FCSTD DOCUMENT  (FreeCAD 0.18R4 (GitTag))
Label: plate
License: All rights reserved
LicenseURL: http://en.wikipedia.org/wiki/All_rights_reserved
objects: Part::Part2DObjectPython×671, App::DocumentObjectGroup×94
note: 671 computed .brp shape members not serialized (recipe doc carries the construction recipe); baked Part::Feature solids carry a one-line shape summary decoded from their .brp

FEATURE [Part::Part2DObjectPython] Arc  # Draft 2D object (typed FeaturePython)
  FirstAngle = 90
  LastAngle = 180
  MakeFace = true
  Placement = pos=(3.275,-3.275,0) rot=(0,0,1;0rad)
  Radius = 0.75
FEATURE [Part::Part2DObjectPython] Arc001  # Draft 2D object (typed FeaturePython)
  FirstAngle = 90
  LastAngle = 180
  MakeFace = true
  Placement = pos=(15.775,-3.275,0) rot=(0,0,-1;1.5708rad)
  Radius = 0.75
FEATURE [Part::Part2DObjectPython] Arc002  # Draft 2D object (typed FeaturePython)
  FirstAngle = 90
  LastAngle = 180
  MakeFace = true
  Placement = pos=(3.275,-15.775,0) rot=(0,0,1;1.5708rad)
  Radius = 0.75
FEATURE [Part::Part2DObjectPython] Arc003  # Draft 2D object (typed FeaturePython)
  FirstAngle = 90
  LastAngle = 180
  MakeFace = true
  Placement = pos=(15.775,-15.775,0) rot=(0,0,1;3.14159rad)
  Radius = 0.75
FEATURE [Part::Part2DObjectPython] Line004  # Draft 2D object (typed FeaturePython)
  ChamferSize = 0
  Closed = false
  End = (16.525,-3.275,0)
  FilletRadius = 0
  Length = 12.5
  MakeFace = true
  Placement = pos=(16.525,-15.775,0) rot=(0,0,1;0rad)
  Points = (2) [(0,0,0),(0,12.5,0)]
  Start = (16.525,-15.775,0)
  Subdivisions = 0
FEATURE [Part::Part2DObjectPython] Line005  # Draft 2D object (typed FeaturePython)
  ChamferSize = 0
  Closed = false
  End = (3.275,-2.525,0)
  FilletRadius = 0
  Length = 12.5
  MakeFace = true
  Placement = pos=(15.775,-2.525,0) rot=(0,0,1;0rad)
  Points = (2) [(0,0,0),(-12.5,2.22045e-15,0)]
  Start = (15.775,-2.525,0)
  Subdivisions = 0
FEATURE [Part::Part2DObjectPython] Line006  # Draft 2D object (typed FeaturePython)
  ChamferSize = 0
  Closed = false
  End = (2.525,-15.775,0)
  FilletRadius = 0
  Length = 12.5
  MakeFace = true
  Placement = pos=(2.525,-3.275,0) rot=(0,0,1;0rad)
  Points = (2) [(0,0,0),(0,-12.5,0)]
  Start = (2.525,-3.275,0)
  Subdivisions = 0
FEATURE [Part::Part2DObjectPython] Line007  # Draft 2D object (typed FeaturePython)
  ChamferSize = 0
  Closed = false
  End = (15.775,-16.525,0)
  FilletRadius = 0
  Length = 12.5
  MakeFace = true
  Placement = pos=(3.275,-16.525,0) rot=(0,0,1;0rad)
  Points = (2) [(0,0,0),(12.5,-3.55271e-15,0)]
  Start = (3.275,-16.525,0)
  Subdivisions = 0
FEATURE [App::DocumentObjectGroup] Group
  Group = -> [Arc,Arc001,Arc002,Arc003,Line004,Line005,Line006,Line007]
FEATURE [Part::Part2DObjectPython] Arc004  # Draft 2D object (typed FeaturePython)
  FirstAngle = 90
  LastAngle = 180
  MakeFace = true
  Placement = pos=(34.7869,-3.275,0) rot=(0,0,-1;1.5708rad)
  Radius = 0.75
FEATURE [Part::Part2DObjectPython] Arc005  # Draft 2D object (typed FeaturePython)
  FirstAngle = 90
  LastAngle = 180
  MakeFace = true
  Placement = pos=(34.7869,-15.775,0) rot=(0,0,1;3.14159rad)
  Radius = 0.75
FEATURE [Part::Part2DObjectPython] Line010  # Draft 2D object (typed FeaturePython)
  ChamferSize = 0
  Closed = false
  End = (22.2869,-2.525,0)
  FilletRadius = 0
  Length = 12.5
  MakeFace = true
  Placement = pos=(34.7869,-2.525,0) rot=(0,0,1;0rad)
  Points = (2) [(0,0,0),(-12.5,2.22045e-15,0)]
  Start = (34.7869,-2.525,0)
  Subdivisions = 0
FEATURE [Part::Part2DObjectPython] Arc006  # Draft 2D object (typed FeaturePython)
  FirstAngle = 90
  LastAngle = 180
  MakeFace = true
  Placement = pos=(22.2869,-15.775,0) rot=(0,0,1;1.5708rad)
  Radius = 0.75
FEATURE [Part::Part2DObjectPython] Arc007  # Draft 2D object (typed FeaturePython)
  FirstAngle = 90
  LastAngle = 180
  MakeFace = true
  Placement = pos=(22.2869,-3.275,0) rot=(0,0,1;0rad)
  Radius = 0.75
FEATURE [Part::Part2DObjectPython] Line014  # Draft 2D object (typed FeaturePython)
  ChamferSize = 0
  Closed = false
  End = (35.5369,-3.275,0)
  FilletRadius = 0
  Length = 12.5
  MakeFace = true
  Placement = pos=(35.5369,-15.775,0) rot=(0,0,1;0rad)
  Points = (2) [(0,0,0),(0,12.5,0)]
  Start = (35.5369,-15.775,0)
  Subdivisions = 0
FEATURE [Part::Part2DObjectPython] Line015  # Draft 2D object (typed FeaturePython)
  ChamferSize = 0
  Closed = false
  End = (34.7869,-16.525,0)
  FilletRadius = 0
  Length = 12.5
  MakeFace = true
  Placement = pos=(22.2869,-16.525,0) rot=(0,0,1;0rad)
  Points = (2) [(0,0,0),(12.5,-3.55271e-15,0)]
  Start = (22.2869,-16.525,0)
  Subdivisions = 0
FEATURE [Part::Part2DObjectPython] Line016  # Draft 2D object (typed FeaturePython)
  ChamferSize = 0
  Closed = false
  End = (21.5369,-15.775,0)
  FilletRadius = 0
  Length = 12.5
  MakeFace = true
  Placement = pos=(21.5369,-3.275,0) rot=(0,0,1;0rad)
  Points = (2) [(0,0,0),(0,-12.5,0)]
  Start = (21.5369,-3.275,0)
  Subdivisions = 0
FEATURE [App::DocumentObjectGroup] Group001
  Group = -> [Arc007,Arc004,Arc006,Arc005,Line014,Line010,Line016,Line015]
FEATURE [Part::Part2DObjectPython] Arc008  # Draft 2D object (typed FeaturePython)
  FirstAngle = 90
  LastAngle = 180
  MakeFace = true
  Placement = pos=(53.7962,-15.775,0) rot=(0,0,1;3.14159rad)
  Radius = 0.75
FEATURE [Part::Part2DObjectPython] Line018  # Draft 2D object (typed FeaturePython)
  ChamferSize = 0
  Closed = false
  End = (40.5462,-15.775,0)
  FilletRadius = 0
  Length = 12.5
  MakeFace = true
  Placement = pos=(40.5462,-3.275,0) rot=(0,0,1;0rad)
  Points = (2) [(0,0,0),(0,-12.5,0)]
  Start = (40.5462,-3.275,0)
  Subdivisions = 0
FEATURE [Part::Part2DObjectPython] Arc009  # Draft 2D object (typed FeaturePython)
  FirstAngle = 90
  LastAngle = 180
  MakeFace = true
  Placement = pos=(41.2962,-15.775,0) rot=(0,0,1;1.5708rad)
  Radius = 0.75
FEATURE [Part::Part2DObjectPython] Line021  # Draft 2D object (typed FeaturePython)
  ChamferSize = 0
  Closed = false
  End = (53.7962,-16.525,0)
  FilletRadius = 0
  Length = 12.5
  MakeFace = true
  Placement = pos=(41.2962,-16.525,0) rot=(0,0,1;0rad)
  Points = (2) [(0,0,0),(12.5,-3.55271e-15,0)]
  Start = (41.2962,-16.525,0)
  Subdivisions = 0
FEATURE [Part::Part2DObjectPython] Arc010  # Draft 2D object (typed FeaturePython)
  FirstAngle = 90
  LastAngle = 180
  MakeFace = true
  Placement = pos=(53.7962,-3.275,0) rot=(0,0,-1;1.5708rad)
  Radius = 0.75
FEATURE [Part::Part2DObjectPython] Arc011  # Draft 2D object (typed FeaturePython)
  FirstAngle = 90
  LastAngle = 180
  MakeFace = true
  Placement = pos=(41.2962,-3.275,0) rot=(0,0,1;0rad)
  Radius = 0.75
FEATURE [Part::Part2DObjectPython] Line022  # Draft 2D object (typed FeaturePython)
  ChamferSize = 0
  Closed = false
  End = (54.5462,-3.275,0)
  FilletRadius = 0
  Length = 12.5
  MakeFace = true
  Placement = pos=(54.5462,-15.775,0) rot=(0,0,1;0rad)
  Points = (2) [(0,0,0),(0,12.5,0)]
  Start = (54.5462,-15.775,0)
  Subdivisions = 0
FEATURE [Part::Part2DObjectPython] Line023  # Draft 2D object (typed FeaturePython)
  ChamferSize = 0
  Closed = false
  End = (41.2962,-2.525,0)
  FilletRadius = 0
  Length = 12.5
  MakeFace = true
  Placement = pos=(53.7962,-2.525,0) rot=(0,0,1;0rad)
  Points = (2) [(0,0,0),(-12.5,2.22045e-15,0)]
  Start = (53.7962,-2.525,0)
  Subdivisions = 0
FEATURE [App::DocumentObjectGroup] Group002
  Group = -> [Arc011,Arc010,Arc009,Arc008,Line022,Line023,Line018,Line021]
FEATURE [Part::Part2DObjectPython] Line026  # Draft 2D object (typed FeaturePython)
  ChamferSize = 0
  Closed = false
  End = (59.5555,-15.775,0)
  FilletRadius = 0
  Length = 12.5
  MakeFace = true
  Placement = pos=(59.5555,-3.275,0) rot=(0,0,1;0rad)
  Points = (2) [(0,0,0),(0,-12.5,0)]
  Start = (59.5555,-3.275,0)
  Subdivisions = 0
FEATURE [Part::Part2DObjectPython] Arc012  # Draft 2D object (typed FeaturePython)
  FirstAngle = 90
  LastAngle = 180
  MakeFace = true
  Placement = pos=(72.8055,-3.275,0) rot=(0,0,-1;1.5708rad)
  Radius = 0.75
FEATURE [Part::Part2DObjectPython] Line027  # Draft 2D object (typed FeaturePython)
  ChamferSize = 0
  Closed = false
  End = (60.3055,-2.525,0)
  FilletRadius = 0
  Length = 12.5
  MakeFace = true
  Placement = pos=(72.8055,-2.525,0) rot=(0,0,1;0rad)
  Points = (2) [(0,0,0),(-12.5,2.22045e-15,0)]
  Start = (72.8055,-2.525,0)
  Subdivisions = 0
FEATURE [Part::Part2DObjectPython] Line029  # Draft 2D object (typed FeaturePython)
  ChamferSize = 0
  Closed = false
  End = (73.5555,-3.275,0)
  FilletRadius = 0
  Length = 12.5
  MakeFace = true
  Placement = pos=(73.5555,-15.775,0) rot=(0,0,1;0rad)
  Points = (2) [(0,0,0),(0,12.5,0)]
  Start = (73.5555,-15.775,0)
  Subdivisions = 0
FEATURE [Part::Part2DObjectPython] Arc013  # Draft 2D object (typed FeaturePython)
  FirstAngle = 90
  LastAngle = 180
  MakeFace = true
  Placement = pos=(60.3055,-15.775,0) rot=(0,0,1;1.5708rad)
  Radius = 0.75
FEATURE [Part::Part2DObjectPython] Line032  # Draft 2D object (typed FeaturePython)
  ChamferSize = 0
  Closed = false
  End = (72.8055,-16.525,0)
  FilletRadius = 0
  Length = 12.5
  MakeFace = true
  Placement = pos=(60.3055,-16.525,0) rot=(0,0,1;0rad)
  Points = (2) [(0,0,0),(12.5,-3.55271e-15,0)]
  Start = (60.3055,-16.525,0)
  Subdivisions = 0
FEATURE [Part::Part2DObjectPython] Arc014  # Draft 2D object (typed FeaturePython)
  FirstAngle = 90
  LastAngle = 180
  MakeFace = true
  Placement = pos=(72.8055,-15.775,0) rot=(0,0,1;3.14159rad)
  Radius = 0.75
FEATURE [Part::Part2DObjectPython] Arc015  # Draft 2D object (typed FeaturePython)
  FirstAngle = 90
  LastAngle = 180
  MakeFace = true
  Placement = pos=(60.3055,-3.275,0) rot=(0,0,1;0rad)
  Radius = 0.75
FEATURE [App::DocumentObjectGroup] Group003
  Group = -> [Arc015,Arc012,Arc013,Arc014,Line029,Line027,Line026,Line032]
FEATURE [Part::Part2DObjectPython] Line033  # Draft 2D object (typed FeaturePython)
  ChamferSize = 0
  Closed = false
  End = (92.5649,-3.275,0)
  FilletRadius = 0
  Length = 12.5
  MakeFace = true
  Placement = pos=(92.5649,-15.775,0) rot=(0,0,1;0rad)
  Points = (2) [(0,0,0),(0,12.5,0)]
  Start = (92.5649,-15.775,0)
  Subdivisions = 0
FEATURE [Part::Part2DObjectPython] Line035  # Draft 2D object (typed FeaturePython)
  ChamferSize = 0
  Closed = false
  End = (78.5649,-15.775,0)
  FilletRadius = 0
  Length = 12.5
  MakeFace = true
  Placement = pos=(78.5649,-3.275,0) rot=(0,0,1;0rad)
  Points = (2) [(0,0,0),(0,-12.5,0)]
  Start = (78.5649,-3.275,0)
  Subdivisions = 0
FEATURE [Part::Part2DObjectPython] Arc016  # Draft 2D object (typed FeaturePython)
  FirstAngle = 90
  LastAngle = 180
  MakeFace = true
  Placement = pos=(91.8149,-3.275,0) rot=(0,0,-1;1.5708rad)
  Radius = 0.75
FEATURE [Part::Part2DObjectPython] Line036  # Draft 2D object (typed FeaturePython)
  ChamferSize = 0
  Closed = false
  End = (79.3149,-2.525,0)
  FilletRadius = 0
  Length = 12.5
  MakeFace = true
  Placement = pos=(91.8149,-2.525,0) rot=(0,0,1;0rad)
  Points = (2) [(0,0,0),(-12.5,2.22045e-15,0)]
  Start = (91.8149,-2.525,0)
  Subdivisions = 0
FEATURE [Part::Part2DObjectPython] Arc017  # Draft 2D object (typed FeaturePython)
  FirstAngle = 90
  LastAngle = 180
  MakeFace = true
  Placement = pos=(79.3149,-15.775,0) rot=(0,0,1;1.5708rad)
  Radius = 0.75
FEATURE [Part::Part2DObjectPython] Line039  # Draft 2D object (typed FeaturePython)
  ChamferSize = 0
  Closed = false
  End = (91.8149,-16.525,0)
  FilletRadius = 0
  Length = 12.5
  MakeFace = true
  Placement = pos=(79.3149,-16.525,0) rot=(0,0,1;0rad)
  Points = (2) [(0,0,0),(12.5,-3.55271e-15,0)]
  Start = (79.3149,-16.525,0)
  Subdivisions = 0
FEATURE [Part::Part2DObjectPython] Arc018  # Draft 2D object (typed FeaturePython)
  FirstAngle = 90
  LastAngle = 180
  MakeFace = true
  Placement = pos=(91.8149,-15.775,0) rot=(0,0,1;3.14159rad)
  Radius = 0.75
FEATURE [Part::Part2DObjectPython] Arc019  # Draft 2D object (typed FeaturePython)
  FirstAngle = 90
  LastAngle = 180
  MakeFace = true
  Placement = pos=(79.3149,-3.275,0) rot=(0,0,1;0rad)
  Radius = 0.75
FEATURE [App::DocumentObjectGroup] Group004
  Group = -> [Arc019,Arc016,Arc017,Arc018,Line033,Line036,Line035,Line039]
FEATURE [Part::Part2DObjectPython] Arc020  # Draft 2D object (typed FeaturePython)
  FirstAngle = 90
  LastAngle = 180
  MakeFace = true
  Placement = pos=(110.827,-3.275,0) rot=(0,0,-1;1.5708rad)
  Radius = 0.75
FEATURE [Part::Part2DObjectPython] Arc021  # Draft 2D object (typed FeaturePython)
  FirstAngle = 90
  LastAngle = 180
  MakeFace = true
  Placement = pos=(98.3268,-3.275,0) rot=(0,0,1;0rad)
  Radius = 0.75
FEATURE [Part::Part2DObjectPython] Line043  # Draft 2D object (typed FeaturePython)
  ChamferSize = 0
  Closed = false
  End = (110.827,-16.525,0)
  FilletRadius = 0
  Length = 12.5
  MakeFace = true
  Placement = pos=(98.3268,-16.525,0) rot=(0,0,1;0rad)
  Points = (2) [(0,0,0),(12.5,-3.55271e-15,0)]
  Start = (98.3268,-16.525,0)
  Subdivisions = 0
FEATURE [Part::Part2DObjectPython] Line045  # Draft 2D object (typed FeaturePython)
  ChamferSize = 0
  Closed = false
  End = (97.5768,-15.775,0)
  FilletRadius = 0
  Length = 12.5
  MakeFace = true
  Placement = pos=(97.5768,-3.275,0) rot=(0,0,1;0rad)
  Points = (2) [(0,0,0),(0,-12.5,0)]
  Start = (97.5768,-3.275,0)
  Subdivisions = 0
FEATURE [Part::Part2DObjectPython] Arc022  # Draft 2D object (typed FeaturePython)
  FirstAngle = 90
  LastAngle = 180
  MakeFace = true
  Placement = pos=(110.827,-15.775,0) rot=(0,0,1;3.14159rad)
  Radius = 0.75
FEATURE [Part::Part2DObjectPython] Line047  # Draft 2D object (typed FeaturePython)
  ChamferSize = 0
  Closed = false
  End = (98.3268,-2.525,0)
  FilletRadius = 0
  Length = 12.5
  MakeFace = true
  Placement = pos=(110.827,-2.525,0) rot=(0,0,1;0rad)
  Points = (2) [(0,0,0),(-12.5,2.22045e-15,0)]
  Start = (110.827,-2.525,0)
  Subdivisions = 0
FEATURE [Part::Part2DObjectPython] Arc023  # Draft 2D object (typed FeaturePython)
  FirstAngle = 90
  LastAngle = 180
  MakeFace = true
  Placement = pos=(98.3268,-15.775,0) rot=(0,0,1;1.5708rad)
  Radius = 0.75
FEATURE [Part::Part2DObjectPython] Line048  # Draft 2D object (typed FeaturePython)
  ChamferSize = 0
  Closed = false
  End = (111.577,-3.275,0)
  FilletRadius = 0
  Length = 12.5
  MakeFace = true
  Placement = pos=(111.577,-15.775,0) rot=(0,0,1;0rad)
  Points = (2) [(0,0,0),(0,12.5,0)]
  Start = (111.577,-15.775,0)
  Subdivisions = 0
FEATURE [App::DocumentObjectGroup] Group005
  Group = -> [Arc021,Arc020,Arc023,Arc022,Line048,Line047,Line045,Line043]
FEATURE [Part::Part2DObjectPython] Line049  # Draft 2D object (typed FeaturePython)
  ChamferSize = 0
  Closed = false
  End = (129.836,-16.525,0)
  FilletRadius = 0
  Length = 12.5
  MakeFace = true
  Placement = pos=(117.336,-16.525,0) rot=(0,0,1;0rad)
  Points = (2) [(0,0,0),(12.5,-3.55271e-15,0)]
  Start = (117.336,-16.525,0)
  Subdivisions = 0
FEATURE [Part::Part2DObjectPython] Arc024  # Draft 2D object (typed FeaturePython)
  FirstAngle = 90
  LastAngle = 180
  MakeFace = true
  Placement = pos=(129.836,-15.775,0) rot=(0,0,1;3.14159rad)
  Radius = 0.75
FEATURE [Part::Part2DObjectPython] Line050  # Draft 2D object (typed FeaturePython)
  ChamferSize = 0
  Closed = false
  End = (116.586,-15.775,0)
  FilletRadius = 0
  Length = 12.5
  MakeFace = true
  Placement = pos=(116.586,-3.275,0) rot=(0,0,1;0rad)
  Points = (2) [(0,0,0),(0,-12.5,0)]
  Start = (116.586,-3.275,0)
  Subdivisions = 0
FEATURE [Part::Part2DObjectPython] Line052  # Draft 2D object (typed FeaturePython)
  ChamferSize = 0
  Closed = false
  End = (117.336,-2.525,0)
  FilletRadius = 0
  Length = 12.5
  MakeFace = true
  Placement = pos=(129.836,-2.525,0) rot=(0,0,1;0rad)
  Points = (2) [(0,0,0),(-12.5,2.22045e-15,0)]
  Start = (129.836,-2.525,0)
  Subdivisions = 0
FEATURE [Part::Part2DObjectPython] Line054  # Draft 2D object (typed FeaturePython)
  ChamferSize = 0
  Closed = false
  End = (130.586,-3.275,0)
  FilletRadius = 0
  Length = 12.5
  MakeFace = true
  Placement = pos=(130.586,-15.775,0) rot=(0,0,1;0rad)
  Points = (2) [(0,0,0),(0,12.5,0)]
  Start = (130.586,-15.775,0)
  Subdivisions = 0
FEATURE [Part::Part2DObjectPython] Arc025  # Draft 2D object (typed FeaturePython)
  FirstAngle = 90
  LastAngle = 180
  MakeFace = true
  Placement = pos=(129.836,-3.275,0) rot=(0,0,-1;1.5708rad)
  Radius = 0.75
FEATURE [Part::Part2DObjectPython] Arc026  # Draft 2D object (typed FeaturePython)
  FirstAngle = 90
  LastAngle = 180
  MakeFace = true
  Placement = pos=(117.336,-3.275,0) rot=(0,0,1;0rad)
  Radius = 0.75
FEATURE [Part::Part2DObjectPython] Arc027  # Draft 2D object (typed FeaturePython)
  FirstAngle = 90
  LastAngle = 180
  MakeFace = true
  Placement = pos=(117.336,-15.775,0) rot=(0,0,1;1.5708rad)
  Radius = 0.75
FEATURE [App::DocumentObjectGroup] Group006
  Group = -> [Arc026,Arc025,Arc027,Arc024,Line054,Line052,Line050,Line049]
FEATURE [Part::Part2DObjectPython] Line057  # Draft 2D object (typed FeaturePython)
  ChamferSize = 0
  Closed = false
  End = (148.845,-16.525,0)
  FilletRadius = 0
  Length = 12.5
  MakeFace = true
  Placement = pos=(136.345,-16.525,0) rot=(0,0,1;0rad)
  Points = (2) [(0,0,0),(12.5,-3.55271e-15,0)]
  Start = (136.345,-16.525,0)
  Subdivisions = 0
FEATURE [Part::Part2DObjectPython] Arc028  # Draft 2D object (typed FeaturePython)
  FirstAngle = 90
  LastAngle = 180
  MakeFace = true
  Placement = pos=(136.345,-15.775,0) rot=(0,0,1;1.5708rad)
  Radius = 0.75
FEATURE [Part::Part2DObjectPython] Line059  # Draft 2D object (typed FeaturePython)
  ChamferSize = 0
  Closed = false
  End = (149.595,-3.275,0)
  FilletRadius = 0
  Length = 12.5
  MakeFace = true
  Placement = pos=(149.595,-15.775,0) rot=(0,0,1;0rad)
  Points = (2) [(0,0,0),(0,12.5,0)]
  Start = (149.595,-15.775,0)
  Subdivisions = 0
FEATURE [Part::Part2DObjectPython] Arc029  # Draft 2D object (typed FeaturePython)
  FirstAngle = 90
  LastAngle = 180
  MakeFace = true
  Placement = pos=(148.845,-15.775,0) rot=(0,0,1;3.14159rad)
  Radius = 0.75
FEATURE [Part::Part2DObjectPython] Line061  # Draft 2D object (typed FeaturePython)
  ChamferSize = 0
  Closed = false
  End = (136.345,-2.525,0)
  FilletRadius = 0
  Length = 12.5
  MakeFace = true
  Placement = pos=(148.845,-2.525,0) rot=(0,0,1;0rad)
  Points = (2) [(0,0,0),(-12.5,2.22045e-15,0)]
  Start = (148.845,-2.525,0)
  Subdivisions = 0
FEATURE [Part::Part2DObjectPython] Arc030  # Draft 2D object (typed FeaturePython)
  FirstAngle = 90
  LastAngle = 180
  MakeFace = true
  Placement = pos=(148.845,-3.275,0) rot=(0,0,-1;1.5708rad)
  Radius = 0.75
FEATURE [Part::Part2DObjectPython] Line064  # Draft 2D object (typed FeaturePython)
  ChamferSize = 0
  Closed = false
  End = (135.595,-15.775,0)
  FilletRadius = 0
  Length = 12.5
  MakeFace = true
  Placement = pos=(135.595,-3.275,0) rot=(0,0,1;0rad)
  Points = (2) [(0,0,0),(0,-12.5,0)]
  Start = (135.595,-3.275,0)
  Subdivisions = 0
FEATURE [Part::Part2DObjectPython] Arc031  # Draft 2D object (typed FeaturePython)
  FirstAngle = 90
  LastAngle = 180
  MakeFace = true
  Placement = pos=(136.345,-3.275,0) rot=(0,0,1;0rad)
  Radius = 0.75
FEATURE [App::DocumentObjectGroup] Group007
  Group = -> [Arc031,Arc030,Arc028,Arc029,Line059,Line061,Line064,Line057]
FEATURE [Part::Part2DObjectPython] Line065  # Draft 2D object (typed FeaturePython)
  ChamferSize = 0
  Closed = false
  End = (168.605,-3.275,0)
  FilletRadius = 0
  Length = 12.5
  MakeFace = true
  Placement = pos=(168.605,-15.775,0) rot=(0,0,1;0rad)
  Points = (2) [(0,0,0),(0,12.5,0)]
  Start = (168.605,-15.775,0)
  Subdivisions = 0
FEATURE [Part::Part2DObjectPython] Arc032  # Draft 2D object (typed FeaturePython)
  FirstAngle = 90
  LastAngle = 180
  MakeFace = true
  Placement = pos=(155.355,-15.775,0) rot=(0,0,1;1.5708rad)
  Radius = 0.75
FEATURE [Part::Part2DObjectPython] Line066  # Draft 2D object (typed FeaturePython)
  ChamferSize = 0
  Closed = false
  End = (167.855,-16.525,0)
  FilletRadius = 0
  Length = 12.5
  MakeFace = true
  Placement = pos=(155.355,-16.525,0) rot=(0,0,1;0rad)
  Points = (2) [(0,0,0),(12.5,-3.55271e-15,0)]
  Start = (155.355,-16.525,0)
  Subdivisions = 0
FEATURE [Part::Part2DObjectPython] Arc033  # Draft 2D object (typed FeaturePython)
  FirstAngle = 90
  LastAngle = 180
  MakeFace = true
  Placement = pos=(167.855,-15.775,0) rot=(0,0,1;3.14159rad)
  Radius = 0.75
FEATURE [Part::Part2DObjectPython] Arc034  # Draft 2D object (typed FeaturePython)
  FirstAngle = 90
  LastAngle = 180
  MakeFace = true
  Placement = pos=(167.855,-3.275,0) rot=(0,0,-1;1.5708rad)
  Radius = 0.75
FEATURE [Part::Part2DObjectPython] Line069  # Draft 2D object (typed FeaturePython)
  ChamferSize = 0
  Closed = false
  End = (155.355,-2.525,0)
  FilletRadius = 0
  Length = 12.5
  MakeFace = true
  Placement = pos=(167.855,-2.525,0) rot=(0,0,1;0rad)
  Points = (2) [(0,0,0),(-12.5,2.22045e-15,0)]
  Start = (167.855,-2.525,0)
  Subdivisions = 0
FEATURE [Part::Part2DObjectPython] Line072  # Draft 2D object (typed FeaturePython)
  ChamferSize = 0
  Closed = false
  End = (154.605,-15.775,0)
  FilletRadius = 0
  Length = 12.5
  MakeFace = true
  Placement = pos=(154.605,-3.275,0) rot=(0,0,1;0rad)
  Points = (2) [(0,0,0),(0,-12.5,0)]
  Start = (154.605,-3.275,0)
  Subdivisions = 0
FEATURE [Part::Part2DObjectPython] Arc035  # Draft 2D object (typed FeaturePython)
  FirstAngle = 90
  LastAngle = 180
  MakeFace = true
  Placement = pos=(155.355,-3.275,0) rot=(0,0,1;0rad)
  Radius = 0.75
FEATURE [App::DocumentObjectGroup] Group008
  Group = -> [Arc035,Arc034,Arc032,Arc033,Line065,Line069,Line072,Line066]
FEATURE [Part::Part2DObjectPython] Line073  # Draft 2D object (typed FeaturePython)
  ChamferSize = 0
  Closed = false
  End = (174.367,-2.525,0)
  FilletRadius = 0
  Length = 12.5
  MakeFace = true
  Placement = pos=(186.867,-2.525,0) rot=(0,0,1;0rad)
  Points = (2) [(0,0,0),(-12.5,2.22045e-15,0)]
  Start = (186.867,-2.525,0)
  Subdivisions = 0
FEATURE [Part::Part2DObjectPython] Line076  # Draft 2D object (typed FeaturePython)
  ChamferSize = 0
  Closed = false
  End = (186.867,-16.525,0)
  FilletRadius = 0
  Length = 12.5
  MakeFace = true
  Placement = pos=(174.367,-16.525,0) rot=(0,0,1;0rad)
  Points = (2) [(0,0,0),(12.5,-3.55271e-15,0)]
  Start = (174.367,-16.525,0)
  Subdivisions = 0
FEATURE [Part::Part2DObjectPython] Arc036  # Draft 2D object (typed FeaturePython)
  FirstAngle = 90
  LastAngle = 180
  MakeFace = true
  Placement = pos=(186.867,-15.775,0) rot=(0,0,1;3.14159rad)
  Radius = 0.75
FEATURE [Part::Part2DObjectPython] Arc037  # Draft 2D object (typed FeaturePython)
  FirstAngle = 90
  LastAngle = 180
  MakeFace = true
  Placement = pos=(186.867,-3.275,0) rot=(0,0,-1;1.5708rad)
  Radius = 0.75
FEATURE [Part::Part2DObjectPython] Arc038  # Draft 2D object (typed FeaturePython)
  FirstAngle = 90
  LastAngle = 180
  MakeFace = true
  Placement = pos=(174.367,-15.775,0) rot=(0,0,1;1.5708rad)
  Radius = 0.75
FEATURE [Part::Part2DObjectPython] Arc039  # Draft 2D object (typed FeaturePython)
  FirstAngle = 90
  LastAngle = 180
  MakeFace = true
  Placement = pos=(174.367,-3.275,0) rot=(0,0,1;0rad)
  Radius = 0.75
FEATURE [Part::Part2DObjectPython] Line078  # Draft 2D object (typed FeaturePython)
  ChamferSize = 0
  Closed = false
  End = (187.617,-3.275,0)
  FilletRadius = 0
  Length = 12.5
  MakeFace = true
  Placement = pos=(187.617,-15.775,0) rot=(0,0,1;0rad)
  Points = (2) [(0,0,0),(0,12.5,0)]
  Start = (187.617,-15.775,0)
  Subdivisions = 0
FEATURE [Part::Part2DObjectPython] Line079  # Draft 2D object (typed FeaturePython)
  ChamferSize = 0
  Closed = false
  End = (173.617,-15.775,0)
  FilletRadius = 0
  Length = 12.5
  MakeFace = true
  Placement = pos=(173.617,-3.275,0) rot=(0,0,1;0rad)
  Points = (2) [(0,0,0),(0,-12.5,0)]
  Start = (173.617,-3.275,0)
  Subdivisions = 0
FEATURE [App::DocumentObjectGroup] Group009
  Group = -> [Arc039,Arc037,Arc038,Arc036,Line078,Line073,Line079,Line076]
FEATURE [Part::Part2DObjectPython] Line081  # Draft 2D object (typed FeaturePython)
  ChamferSize = 0
  Closed = false
  End = (193.376,-2.525,0)
  FilletRadius = 0
  Length = 12.5
  MakeFace = true
  Placement = pos=(205.876,-2.525,0) rot=(0,0,1;0rad)
  Points = (2) [(0,0,0),(-12.5,2.22045e-15,0)]
  Start = (205.876,-2.525,0)
  Subdivisions = 0
FEATURE [Part::Part2DObjectPython] Line083  # Draft 2D object (typed FeaturePython)
  ChamferSize = 0
  Closed = false
  End = (205.876,-16.525,0)
  FilletRadius = 0
  Length = 12.5
  MakeFace = true
  Placement = pos=(193.376,-16.525,0) rot=(0,0,1;0rad)
  Points = (2) [(0,0,0),(12.5,-3.55271e-15,0)]
  Start = (193.376,-16.525,0)
  Subdivisions = 0
FEATURE [Part::Part2DObjectPython] Arc040  # Draft 2D object (typed FeaturePython)
  FirstAngle = 90
  LastAngle = 180
  MakeFace = true
  Placement = pos=(205.876,-3.275,0) rot=(0,0,-1;1.5708rad)
  Radius = 0.75
FEATURE [Part::Part2DObjectPython] Arc041  # Draft 2D object (typed FeaturePython)
  FirstAngle = 90
  LastAngle = 180
  MakeFace = true
  Placement = pos=(205.876,-15.775,0) rot=(0,0,1;3.14159rad)
  Radius = 0.75
FEATURE [Part::Part2DObjectPython] Arc042  # Draft 2D object (typed FeaturePython)
  FirstAngle = 90
  LastAngle = 180
  MakeFace = true
  Placement = pos=(193.376,-15.775,0) rot=(0,0,1;1.5708rad)
  Radius = 0.75
FEATURE [Part::Part2DObjectPython] Arc043  # Draft 2D object (typed FeaturePython)
  FirstAngle = 90
  LastAngle = 180
  MakeFace = true
  Placement = pos=(193.376,-3.275,0) rot=(0,0,1;0rad)
  Radius = 0.75
FEATURE [Part::Part2DObjectPython] Line087  # Draft 2D object (typed FeaturePython)
  ChamferSize = 0
  Closed = false
  End = (206.626,-3.275,0)
  FilletRadius = 0
  Length = 12.5
  MakeFace = true
  Placement = pos=(206.626,-15.775,0) rot=(0,0,1;0rad)
  Points = (2) [(0,0,0),(0,12.5,0)]
  Start = (206.626,-15.775,0)
  Subdivisions = 0
FEATURE [Part::Part2DObjectPython] Line088  # Draft 2D object (typed FeaturePython)
  ChamferSize = 0
  Closed = false
  End = (192.626,-15.775,0)
  FilletRadius = 0
  Length = 12.5
  MakeFace = true
  Placement = pos=(192.626,-3.275,0) rot=(0,0,1;0rad)
  Points = (2) [(0,0,0),(0,-12.5,0)]
  Start = (192.626,-3.275,0)
  Subdivisions = 0
FEATURE [App::DocumentObjectGroup] Group010
  Group = -> [Arc043,Arc040,Arc042,Arc041,Line087,Line081,Line088,Line083]
FEATURE [Part::Part2DObjectPython] Arc044  # Draft 2D object (typed FeaturePython)
  FirstAngle = 90
  LastAngle = 180
  MakeFace = true
  Placement = pos=(212.385,-3.275,0) rot=(0,0,1;0rad)
  Radius = 0.75
FEATURE [Part::Part2DObjectPython] Line090  # Draft 2D object (typed FeaturePython)
  ChamferSize = 0
  Closed = false
  End = (211.635,-15.775,0)
  FilletRadius = 0
  Length = 12.5
  MakeFace = true
  Placement = pos=(211.635,-3.275,0) rot=(0,0,1;0rad)
  Points = (2) [(0,0,0),(0,-12.5,0)]
  Start = (211.635,-3.275,0)
  Subdivisions = 0
FEATURE [Part::Part2DObjectPython] Line091  # Draft 2D object (typed FeaturePython)
  ChamferSize = 0
  Closed = false
  End = (212.385,-2.525,0)
  FilletRadius = 0
  Length = 12.5
  MakeFace = true
  Placement = pos=(224.885,-2.525,0) rot=(0,0,1;0rad)
  Points = (2) [(0,0,0),(-12.5,2.22045e-15,0)]
  Start = (224.885,-2.525,0)
  Subdivisions = 0
FEATURE [Part::Part2DObjectPython] Line093  # Draft 2D object (typed FeaturePython)
  ChamferSize = 0
  Closed = false
  End = (224.885,-16.525,0)
  FilletRadius = 0
  Length = 12.5
  MakeFace = true
  Placement = pos=(212.385,-16.525,0) rot=(0,0,1;0rad)
  Points = (2) [(0,0,0),(12.5,-3.55271e-15,0)]
  Start = (212.385,-16.525,0)
  Subdivisions = 0
FEATURE [Part::Part2DObjectPython] Arc045  # Draft 2D object (typed FeaturePython)
  FirstAngle = 90
  LastAngle = 180
  MakeFace = true
  Placement = pos=(224.885,-15.775,0) rot=(0,0,1;3.14159rad)
  Radius = 0.75
FEATURE [Part::Part2DObjectPython] Arc046  # Draft 2D object (typed FeaturePython)
  FirstAngle = 90
  LastAngle = 180
  MakeFace = true
  Placement = pos=(212.385,-15.775,0) rot=(0,0,1;1.5708rad)
  Radius = 0.75
FEATURE [Part::Part2DObjectPython] Line095  # Draft 2D object (typed FeaturePython)
  ChamferSize = 0
  Closed = false
  End = (225.635,-3.275,0)
  FilletRadius = 0
  Length = 12.5
  MakeFace = true
  Placement = pos=(225.635,-15.775,0) rot=(0,0,1;0rad)
  Points = (2) [(0,0,0),(0,12.5,0)]
  Start = (225.635,-15.775,0)
  Subdivisions = 0
FEATURE [Part::Part2DObjectPython] Arc047  # Draft 2D object (typed FeaturePython)
  FirstAngle = 90
  LastAngle = 180
  MakeFace = true
  Placement = pos=(224.885,-3.275,0) rot=(0,0,-1;1.5708rad)
  Radius = 0.75
FEATURE [App::DocumentObjectGroup] Group011
  Group = -> [Arc044,Arc047,Arc046,Arc045,Line095,Line091,Line090,Line093]
FEATURE [Part::Part2DObjectPython] Line098  # Draft 2D object (typed FeaturePython)
  ChamferSize = 0
  Closed = false
  End = (231.395,-2.525,0)
  FilletRadius = 0
  Length = 12.5
  MakeFace = true
  Placement = pos=(243.895,-2.525,0) rot=(0,0,1;0rad)
  Points = (2) [(0,0,0),(-12.5,2.22045e-15,0)]
  Start = (243.895,-2.525,0)
  Subdivisions = 0
FEATURE [Part::Part2DObjectPython] Arc048  # Draft 2D object (typed FeaturePython)
  FirstAngle = 90
  LastAngle = 180
  MakeFace = true
  Placement = pos=(231.395,-3.275,0) rot=(0,0,1;0rad)
  Radius = 0.75
FEATURE [Part::Part2DObjectPython] Line100  # Draft 2D object (typed FeaturePython)
  ChamferSize = 0
  Closed = false
  End = (243.895,-16.525,0)
  FilletRadius = 0
  Length = 12.5
  MakeFace = true
  Placement = pos=(231.395,-16.525,0) rot=(0,0,1;0rad)
  Points = (2) [(0,0,0),(12.5,-3.55271e-15,0)]
  Start = (231.395,-16.525,0)
  Subdivisions = 0
FEATURE [Part::Part2DObjectPython] Arc049  # Draft 2D object (typed FeaturePython)
  FirstAngle = 90
  LastAngle = 180
  MakeFace = true
  Placement = pos=(231.395,-15.775,0) rot=(0,0,1;1.5708rad)
  Radius = 0.75
FEATURE [Part::Part2DObjectPython] Line102  # Draft 2D object (typed FeaturePython)
  ChamferSize = 0
  Closed = false
  End = (230.645,-15.775,0)
  FilletRadius = 0
  Length = 12.5
  MakeFace = true
  Placement = pos=(230.645,-3.275,0) rot=(0,0,1;0rad)
  Points = (2) [(0,0,0),(0,-12.5,0)]
  Start = (230.645,-3.275,0)
  Subdivisions = 0
FEATURE [Part::Part2DObjectPython] Line103  # Draft 2D object (typed FeaturePython)
  ChamferSize = 0
  Closed = false
  End = (244.645,-3.275,0)
  FilletRadius = 0
  Length = 12.5
  MakeFace = true
  Placement = pos=(244.645,-15.775,0) rot=(0,0,1;0rad)
  Points = (2) [(0,0,0),(0,12.5,0)]
  Start = (244.645,-15.775,0)
  Subdivisions = 0
FEATURE [Part::Part2DObjectPython] Arc050  # Draft 2D object (typed FeaturePython)
  FirstAngle = 90
  LastAngle = 180
  MakeFace = true
  Placement = pos=(243.895,-15.775,0) rot=(0,0,1;3.14159rad)
  Radius = 0.75
FEATURE [Part::Part2DObjectPython] Arc051  # Draft 2D object (typed FeaturePython)
  FirstAngle = 90
  LastAngle = 180
  MakeFace = true
  Placement = pos=(243.895,-3.275,0) rot=(0,0,-1;1.5708rad)
  Radius = 0.75
FEATURE [App::DocumentObjectGroup] Group012
  Group = -> [Arc048,Arc051,Arc049,Arc050,Line103,Line098,Line102,Line100]
FEATURE [Part::Part2DObjectPython] Arc052  # Draft 2D object (typed FeaturePython)
  FirstAngle = 90
  LastAngle = 180
  MakeFace = true
  Placement = pos=(272.411,-3.275,0) rot=(0,0,-1;1.5708rad)
  Radius = 0.75
FEATURE [Part::Part2DObjectPython] Arc053  # Draft 2D object (typed FeaturePython)
  FirstAngle = 90
  LastAngle = 180
  MakeFace = true
  Placement = pos=(272.411,-15.775,0) rot=(0,0,1;3.14159rad)
  Radius = 0.75
FEATURE [Part::Part2DObjectPython] Line105  # Draft 2D object (typed FeaturePython)
  ChamferSize = 0
  Closed = false
  End = (273.161,-3.275,0)
  FilletRadius = 0
  Length = 12.5
  MakeFace = true
  Placement = pos=(273.161,-15.775,0) rot=(0,0,1;0rad)
  Points = (2) [(0,0,0),(0,12.5,0)]
  Start = (273.161,-15.775,0)
  Subdivisions = 0
FEATURE [Part::Part2DObjectPython] Line107  # Draft 2D object (typed FeaturePython)
  ChamferSize = 0
  Closed = false
  End = (259.161,-15.775,0)
  FilletRadius = 0
  Length = 12.5
  MakeFace = true
  Placement = pos=(259.161,-3.275,0) rot=(0,0,1;0rad)
  Points = (2) [(0,0,0),(0,-12.5,0)]
  Start = (259.161,-3.275,0)
  Subdivisions = 0
FEATURE [Part::Part2DObjectPython] Line109  # Draft 2D object (typed FeaturePython)
  ChamferSize = 0
  Closed = false
  End = (259.911,-2.525,0)
  FilletRadius = 0
  Length = 12.5
  MakeFace = true
  Placement = pos=(272.411,-2.525,0) rot=(0,0,1;0rad)
  Points = (2) [(0,0,0),(-12.5,2.22045e-15,0)]
  Start = (272.411,-2.525,0)
  Subdivisions = 0
FEATURE [Part::Part2DObjectPython] Arc054  # Draft 2D object (typed FeaturePython)
  FirstAngle = 90
  LastAngle = 180
  MakeFace = true
  Placement = pos=(259.911,-3.275,0) rot=(0,0,1;0rad)
  Radius = 0.75
FEATURE [Part::Part2DObjectPython] Line111  # Draft 2D object (typed FeaturePython)
  ChamferSize = 0
  Closed = false
  End = (272.411,-16.525,0)
  FilletRadius = 0
  Length = 12.5
  MakeFace = true
  Placement = pos=(259.911,-16.525,0) rot=(0,0,1;0rad)
  Points = (2) [(0,0,0),(12.5,-3.55271e-15,0)]
  Start = (259.911,-16.525,0)
  Subdivisions = 0
FEATURE [Part::Part2DObjectPython] Arc055  # Draft 2D object (typed FeaturePython)
  FirstAngle = 90
  LastAngle = 180
  MakeFace = true
  Placement = pos=(259.911,-15.775,0) rot=(0,0,1;1.5708rad)
  Radius = 0.75
FEATURE [Part::Part2DObjectPython] Line113  # Draft 2D object (typed FeaturePython)
  ChamferSize = 0
  Closed = false
  End = (310.73,-16.525,0)
  FilletRadius = 0
  Length = 12.5
  MakeFace = true
  Placement = pos=(298.23,-16.525,0) rot=(0,0,1;0rad)
  Points = (2) [(0,0,0),(12.5,-3.55271e-15,0)]
  Start = (298.23,-16.525,0)
  Subdivisions = 0
FEATURE [Part::Part2DObjectPython] Line115  # Draft 2D object (typed FeaturePython)
  ChamferSize = 0
  Closed = false
  End = (298.23,-2.525,0)
  FilletRadius = 0
  Length = 12.5
  MakeFace = true
  Placement = pos=(310.73,-2.525,0) rot=(0,0,1;0rad)
  Points = (2) [(0,0,0),(-12.5,2.22045e-15,0)]
  Start = (310.73,-2.525,0)
  Subdivisions = 0
FEATURE [Part::Part2DObjectPython] Line116  # Draft 2D object (typed FeaturePython)
  ChamferSize = 0
  Closed = false
  End = (311.48,-3.275,0)
  FilletRadius = 0
  Length = 12.5
  MakeFace = true
  Placement = pos=(311.48,-15.775,0) rot=(0,0,1;0rad)
  Points = (2) [(0,0,0),(0,12.5,0)]
  Start = (311.48,-15.775,0)
  Subdivisions = 0
FEATURE [Part::Part2DObjectPython] Line118  # Draft 2D object (typed FeaturePython)
  ChamferSize = 0
  Closed = false
  End = (297.48,-15.775,0)
  FilletRadius = 0
  Length = 12.5
  MakeFace = true
  Placement = pos=(297.48,-3.275,0) rot=(0,0,1;0rad)
  Points = (2) [(0,0,0),(0,-12.5,0)]
  Start = (297.48,-3.275,0)
  Subdivisions = 0
FEATURE [Part::Part2DObjectPython] Arc056  # Draft 2D object (typed FeaturePython)
  FirstAngle = 90
  LastAngle = 180
  MakeFace = true
  Placement = pos=(310.73,-15.775,0) rot=(0,0,1;3.14159rad)
  Radius = 0.75
FEATURE [Part::Part2DObjectPython] Arc057  # Draft 2D object (typed FeaturePython)
  FirstAngle = 90
  LastAngle = 180
  MakeFace = true
  Placement = pos=(310.73,-3.275,0) rot=(0,0,-1;1.5708rad)
  Radius = 0.75
FEATURE [Part::Part2DObjectPython] Arc058  # Draft 2D object (typed FeaturePython)
  FirstAngle = 90
  LastAngle = 180
  MakeFace = true
  Placement = pos=(298.23,-3.275,0) rot=(0,0,1;0rad)
  Radius = 0.75
FEATURE [Part::Part2DObjectPython] Arc059  # Draft 2D object (typed FeaturePython)
  FirstAngle = 90
  LastAngle = 180
  MakeFace = true
  Placement = pos=(298.23,-15.775,0) rot=(0,0,1;1.5708rad)
  Radius = 0.75
FEATURE [App::DocumentObjectGroup] Group014
  Group = -> [Arc058,Arc057,Arc059,Arc056,Line116,Line115,Line118,Line113]
FEATURE [Part::Part2DObjectPython] Arc060  # Draft 2D object (typed FeaturePython)
  FirstAngle = 90
  LastAngle = 180
  MakeFace = true
  Placement = pos=(20.5299,-34.7869,0) rot=(0,0,1;3.14159rad)
  Radius = 0.75
FEATURE [Part::Part2DObjectPython] Line122  # Draft 2D object (typed FeaturePython)
  ChamferSize = 0
  Closed = false
  End = (7.27987,-34.7869,0)
  FilletRadius = 0
  Length = 12.5
  MakeFace = true
  Placement = pos=(7.27987,-22.2869,0) rot=(0,0,1;0rad)
  Points = (2) [(0,0,0),(0,-12.5,0)]
  Start = (7.27987,-22.2869,0)
  Subdivisions = 0
FEATURE [Part::Part2DObjectPython] Arc061  # Draft 2D object (typed FeaturePython)
  FirstAngle = 90
  LastAngle = 180
  MakeFace = true
  Placement = pos=(8.02987,-34.7869,0) rot=(0,0,1;1.5708rad)
  Radius = 0.75
FEATURE [Part::Part2DObjectPython] Line125  # Draft 2D object (typed FeaturePython)
  ChamferSize = 0
  Closed = false
  End = (20.5299,-35.5369,0)
  FilletRadius = 0
  Length = 12.5
  MakeFace = true
  Placement = pos=(8.02987,-35.5369,0) rot=(0,0,1;0rad)
  Points = (2) [(0,0,0),(12.5,0,0)]
  Start = (8.02987,-35.5369,0)
  Subdivisions = 0
FEATURE [Part::Part2DObjectPython] Arc062  # Draft 2D object (typed FeaturePython)
  FirstAngle = 90
  LastAngle = 180
  MakeFace = true
  Placement = pos=(20.5299,-22.2869,0) rot=(0,0,-1;1.5708rad)
  Radius = 0.75
FEATURE [Part::Part2DObjectPython] Arc063  # Draft 2D object (typed FeaturePython)
  FirstAngle = 90
  LastAngle = 180
  MakeFace = true
  Placement = pos=(8.02987,-22.2869,0) rot=(0,0,1;0rad)
  Radius = 0.75
FEATURE [Part::Part2DObjectPython] Line126  # Draft 2D object (typed FeaturePython)
  ChamferSize = 0
  Closed = false
  End = (21.2799,-22.2869,0)
  FilletRadius = 0
  Length = 12.5
  MakeFace = true
  Placement = pos=(21.2799,-34.7869,0) rot=(0,0,1;0rad)
  Points = (2) [(0,0,0),(0,12.5,0)]
  Start = (21.2799,-34.7869,0)
  Subdivisions = 0
FEATURE [Part::Part2DObjectPython] Line127  # Draft 2D object (typed FeaturePython)
  ChamferSize = 0
  Closed = false
  End = (8.02987,-21.5369,0)
  FilletRadius = 0
  Length = 12.5
  MakeFace = true
  Placement = pos=(20.5299,-21.5369,0) rot=(0,0,1;0rad)
  Points = (2) [(0,0,0),(-12.5,3.55271e-15,0)]
  Start = (20.5299,-21.5369,0)
  Subdivisions = 0
FEATURE [App::DocumentObjectGroup] Group017
  Group = -> [Arc063,Arc062,Arc061,Arc060,Line126,Line127,Line122,Line125]
FEATURE [Part::Part2DObjectPython] Arc064  # Draft 2D object (typed FeaturePython)
  FirstAngle = 90
  LastAngle = 180
  MakeFace = true
  Placement = pos=(31.7915,-34.7869,0) rot=(0,0,1;1.5708rad)
  Radius = 0.75
FEATURE [Part::Part2DObjectPython] Arc065  # Draft 2D object (typed FeaturePython)
  FirstAngle = 90
  LastAngle = 180
  MakeFace = true
  Placement = pos=(44.2915,-22.2869,0) rot=(0,0,-1;1.5708rad)
  Radius = 0.75
FEATURE [Part::Part2DObjectPython] Line129  # Draft 2D object (typed FeaturePython)
  ChamferSize = 0
  Closed = false
  End = (45.0415,-22.2869,0)
  FilletRadius = 0
  Length = 12.5
  MakeFace = true
  Placement = pos=(45.0415,-34.7869,0) rot=(0,0,1;0rad)
  Points = (2) [(0,0,0),(0,12.5,0)]
  Start = (45.0415,-34.7869,0)
  Subdivisions = 0
FEATURE [Part::Part2DObjectPython] Line130  # Draft 2D object (typed FeaturePython)
  ChamferSize = 0
  Closed = false
  End = (31.7915,-21.5369,0)
  FilletRadius = 0
  Length = 12.5
  MakeFace = true
  Placement = pos=(44.2915,-21.5369,0) rot=(0,0,1;0rad)
  Points = (2) [(0,0,0),(-12.5,3.55271e-15,0)]
  Start = (44.2915,-21.5369,0)
  Subdivisions = 0
FEATURE [Part::Part2DObjectPython] Arc066  # Draft 2D object (typed FeaturePython)
  FirstAngle = 90
  LastAngle = 180
  MakeFace = true
  Placement = pos=(44.2915,-34.7869,0) rot=(0,0,1;3.14159rad)
  Radius = 0.75
FEATURE [Part::Part2DObjectPython] Line132  # Draft 2D object (typed FeaturePython)
  ChamferSize = 0
  Closed = false
  End = (44.2915,-35.5369,0)
  FilletRadius = 0
  Length = 12.5
  MakeFace = true
  Placement = pos=(31.7915,-35.5369,0) rot=(0,0,1;0rad)
  Points = (2) [(0,0,0),(12.5,0,0)]
  Start = (31.7915,-35.5369,0)
  Subdivisions = 0
FEATURE [Part::Part2DObjectPython] Arc067  # Draft 2D object (typed FeaturePython)
  FirstAngle = 90
  LastAngle = 180
  MakeFace = true
  Placement = pos=(31.7915,-22.2869,0) rot=(0,0,1;0rad)
  Radius = 0.75
FEATURE [Part::Part2DObjectPython] Line134  # Draft 2D object (typed FeaturePython)
  ChamferSize = 0
  Closed = false
  End = (31.0415,-34.7869,0)
  FilletRadius = 0
  Length = 12.5
  MakeFace = true
  Placement = pos=(31.0415,-22.2869,0) rot=(0,0,1;0rad)
  Points = (2) [(0,0,0),(0,-12.5,0)]
  Start = (31.0415,-22.2869,0)
  Subdivisions = 0
FEATURE [App::DocumentObjectGroup] Group018
  Group = -> [Arc067,Arc065,Arc064,Arc066,Line129,Line130,Line134,Line132]
FEATURE [Part::Part2DObjectPython] Line137  # Draft 2D object (typed FeaturePython)
  ChamferSize = 0
  Closed = false
  End = (50.0509,-34.7869,0)
  FilletRadius = 0
  Length = 12.5
  MakeFace = true
  Placement = pos=(50.0509,-22.2869,0) rot=(0,0,1;0rad)
  Points = (2) [(0,0,0),(0,-12.5,0)]
  Start = (50.0509,-22.2869,0)
  Subdivisions = 0
FEATURE [Part::Part2DObjectPython] Arc068  # Draft 2D object (typed FeaturePython)
  FirstAngle = 90
  LastAngle = 180
  MakeFace = true
  Placement = pos=(50.8009,-22.2869,0) rot=(0,0,1;0rad)
  Radius = 0.75
FEATURE [Part::Part2DObjectPython] Arc069  # Draft 2D object (typed FeaturePython)
  FirstAngle = 90
  LastAngle = 180
  MakeFace = true
  Placement = pos=(50.8009,-34.7869,0) rot=(0,0,1;1.5708rad)
  Radius = 0.75
FEATURE [Part::Part2DObjectPython] Arc070  # Draft 2D object (typed FeaturePython)
  FirstAngle = 90
  LastAngle = 180
  MakeFace = true
  Placement = pos=(63.3009,-22.2869,0) rot=(0,0,-1;1.5708rad)
  Radius = 0.75
FEATURE [Part::Part2DObjectPython] Line139  # Draft 2D object (typed FeaturePython)
  ChamferSize = 0
  Closed = false
  End = (50.8009,-21.5369,0)
  FilletRadius = 0
  Length = 12.5
  MakeFace = true
  Placement = pos=(63.3009,-21.5369,0) rot=(0,0,1;0rad)
  Points = (2) [(0,0,0),(-12.5,3.55271e-15,0)]
  Start = (63.3009,-21.5369,0)
  Subdivisions = 0
FEATURE [Part::Part2DObjectPython] Line141  # Draft 2D object (typed FeaturePython)
  ChamferSize = 0
  Closed = false
  End = (63.3009,-35.5369,0)
  FilletRadius = 0
  Length = 12.5
  MakeFace = true
  Placement = pos=(50.8009,-35.5369,0) rot=(0,0,1;0rad)
  Points = (2) [(0,0,0),(12.5,0,0)]
  Start = (50.8009,-35.5369,0)
  Subdivisions = 0
FEATURE [Part::Part2DObjectPython] Arc071  # Draft 2D object (typed FeaturePython)
  FirstAngle = 90
  LastAngle = 180
  MakeFace = true
  Placement = pos=(63.3009,-34.7869,0) rot=(0,0,1;3.14159rad)
  Radius = 0.75
FEATURE [Part::Part2DObjectPython] Line142  # Draft 2D object (typed FeaturePython)
  ChamferSize = 0
  Closed = false
  End = (64.0509,-22.2869,0)
  FilletRadius = 0
  Length = 12.5
  MakeFace = true
  Placement = pos=(64.0509,-34.7869,0) rot=(0,0,1;0rad)
  Points = (2) [(0,0,0),(0,12.5,0)]
  Start = (64.0509,-34.7869,0)
  Subdivisions = 0
FEATURE [App::DocumentObjectGroup] Group019
  Group = -> [Arc068,Arc070,Arc069,Arc071,Line142,Line139,Line137,Line141]
FEATURE [Part::Part2DObjectPython] Arc072  # Draft 2D object (typed FeaturePython)
  FirstAngle = 90
  LastAngle = 180
  MakeFace = true
  Placement = pos=(69.8102,-34.7869,0) rot=(0,0,1;1.5708rad)
  Radius = 0.75
FEATURE [Part::Part2DObjectPython] Arc073  # Draft 2D object (typed FeaturePython)
  FirstAngle = 90
  LastAngle = 180
  MakeFace = true
  Placement = pos=(82.3102,-34.7869,0) rot=(0,0,1;3.14159rad)
  Radius = 0.75
FEATURE [Part::Part2DObjectPython] Line148  # Draft 2D object (typed FeaturePython)
  ChamferSize = 0
  Closed = false
  End = (69.0602,-34.7869,0)
  FilletRadius = 0
  Length = 12.5
  MakeFace = true
  Placement = pos=(69.0602,-22.2869,0) rot=(0,0,1;0rad)
  Points = (2) [(0,0,0),(0,-12.5,0)]
  Start = (69.0602,-22.2869,0)
  Subdivisions = 0
FEATURE [Part::Part2DObjectPython] Arc074  # Draft 2D object (typed FeaturePython)
  FirstAngle = 90
  LastAngle = 180
  MakeFace = true
  Placement = pos=(69.8102,-22.2869,0) rot=(0,0,1;0rad)
  Radius = 0.75
FEATURE [Part::Part2DObjectPython] Arc075  # Draft 2D object (typed FeaturePython)
  FirstAngle = 90
  LastAngle = 180
  MakeFace = true
  Placement = pos=(82.3102,-22.2869,0) rot=(0,0,-1;1.5708rad)
  Radius = 0.75
FEATURE [Part::Part2DObjectPython] Line149  # Draft 2D object (typed FeaturePython)
  ChamferSize = 0
  Closed = false
  End = (69.8102,-21.5369,0)
  FilletRadius = 0
  Length = 12.5
  MakeFace = true
  Placement = pos=(82.3102,-21.5369,0) rot=(0,0,1;0rad)
  Points = (2) [(0,0,0),(-12.5,3.55271e-15,0)]
  Start = (82.3102,-21.5369,0)
  Subdivisions = 0
FEATURE [Part::Part2DObjectPython] Line150  # Draft 2D object (typed FeaturePython)
  ChamferSize = 0
  Closed = false
  End = (82.3102,-35.5369,0)
  FilletRadius = 0
  Length = 12.5
  MakeFace = true
  Placement = pos=(69.8102,-35.5369,0) rot=(0,0,1;0rad)
  Points = (2) [(0,0,0),(12.5,0,0)]
  Start = (69.8102,-35.5369,0)
  Subdivisions = 0
FEATURE [Part::Part2DObjectPython] Line151  # Draft 2D object (typed FeaturePython)
  ChamferSize = 0
  Closed = false
  End = (83.0602,-22.2869,0)
  FilletRadius = 0
  Length = 12.5
  MakeFace = true
  Placement = pos=(83.0602,-34.7869,0) rot=(0,0,1;0rad)
  Points = (2) [(0,0,0),(0,12.5,0)]
  Start = (83.0602,-34.7869,0)
  Subdivisions = 0
FEATURE [App::DocumentObjectGroup] Group020
  Group = -> [Arc074,Arc075,Arc072,Arc073,Line151,Line149,Line148,Line150]
FEATURE [Part::Part2DObjectPython] Arc076  # Draft 2D object (typed FeaturePython)
  FirstAngle = 90
  LastAngle = 180
  MakeFace = true
  Placement = pos=(88.8221,-34.7869,0) rot=(0,0,1;1.5708rad)
  Radius = 0.75
FEATURE [Part::Part2DObjectPython] Line153  # Draft 2D object (typed FeaturePython)
  ChamferSize = 0
  Closed = false
  End = (88.0721,-34.7869,0)
  FilletRadius = 0
  Length = 12.5
  MakeFace = true
  Placement = pos=(88.0721,-22.2869,0) rot=(0,0,1;0rad)
  Points = (2) [(0,0,0),(0,-12.5,0)]
  Start = (88.0721,-22.2869,0)
  Subdivisions = 0
FEATURE [Part::Part2DObjectPython] Arc077  # Draft 2D object (typed FeaturePython)
  FirstAngle = 90
  LastAngle = 180
  MakeFace = true
  Placement = pos=(101.322,-34.7869,0) rot=(0,0,1;3.14159rad)
  Radius = 0.75
FEATURE [Part::Part2DObjectPython] Arc078  # Draft 2D object (typed FeaturePython)
  FirstAngle = 90
  LastAngle = 180
  MakeFace = true
  Placement = pos=(101.322,-22.2869,0) rot=(0,0,-1;1.5708rad)
  Radius = 0.75
FEATURE [Part::Part2DObjectPython] Line157  # Draft 2D object (typed FeaturePython)
  ChamferSize = 0
  Closed = false
  End = (101.322,-35.5369,0)
  FilletRadius = 0
  Length = 12.5
  MakeFace = true
  Placement = pos=(88.8221,-35.5369,0) rot=(0,0,1;0rad)
  Points = (2) [(0,0,0),(12.5,0,0)]
  Start = (88.8221,-35.5369,0)
  Subdivisions = 0
FEATURE [Part::Part2DObjectPython] Line159  # Draft 2D object (typed FeaturePython)
  ChamferSize = 0
  Closed = false
  End = (102.072,-22.2869,0)
  FilletRadius = 0
  Length = 12.5
  MakeFace = true
  Placement = pos=(102.072,-34.7869,0) rot=(0,0,1;0rad)
  Points = (2) [(0,0,0),(0,12.5,0)]
  Start = (102.072,-34.7869,0)
  Subdivisions = 0
FEATURE [Part::Part2DObjectPython] Arc079  # Draft 2D object (typed FeaturePython)
  FirstAngle = 90
  LastAngle = 180
  MakeFace = true
  Placement = pos=(88.8221,-22.2869,0) rot=(0,0,1;0rad)
  Radius = 0.75
FEATURE [Part::Part2DObjectPython] Line160  # Draft 2D object (typed FeaturePython)
  ChamferSize = 0
  Closed = false
  End = (88.8221,-21.5369,0)
  FilletRadius = 0
  Length = 12.5
  MakeFace = true
  Placement = pos=(101.322,-21.5369,0) rot=(0,0,1;0rad)
  Points = (2) [(0,0,0),(-12.5,3.55271e-15,0)]
  Start = (101.322,-21.5369,0)
  Subdivisions = 0
FEATURE [App::DocumentObjectGroup] Group021
  Group = -> [Arc079,Arc078,Arc076,Arc077,Line159,Line160,Line153,Line157]
FEATURE [Part::Part2DObjectPython] Arc080  # Draft 2D object (typed FeaturePython)
  FirstAngle = 90
  LastAngle = 180
  MakeFace = true
  Placement = pos=(107.831,-34.7869,0) rot=(0,0,1;1.5708rad)
  Radius = 0.75
FEATURE [Part::Part2DObjectPython] Line161  # Draft 2D object (typed FeaturePython)
  ChamferSize = 0
  Closed = false
  End = (107.081,-34.7869,0)
  FilletRadius = 0
  Length = 12.5
  MakeFace = true
  Placement = pos=(107.081,-22.2869,0) rot=(0,0,1;0rad)
  Points = (2) [(0,0,0),(0,-12.5,0)]
  Start = (107.081,-22.2869,0)
  Subdivisions = 0
FEATURE [Part::Part2DObjectPython] Arc081  # Draft 2D object (typed FeaturePython)
  FirstAngle = 90
  LastAngle = 180
  MakeFace = true
  Placement = pos=(120.331,-34.7869,0) rot=(0,0,1;3.14159rad)
  Radius = 0.75
FEATURE [Part::Part2DObjectPython] Arc082  # Draft 2D object (typed FeaturePython)
  FirstAngle = 90
  LastAngle = 180
  MakeFace = true
  Placement = pos=(107.831,-22.2869,0) rot=(0,0,1;0rad)
  Radius = 0.75
FEATURE [Part::Part2DObjectPython] Arc083  # Draft 2D object (typed FeaturePython)
  FirstAngle = 90
  LastAngle = 180
  MakeFace = true
  Placement = pos=(120.331,-22.2869,0) rot=(0,0,-1;1.5708rad)
  Radius = 0.75
FEATURE [Part::Part2DObjectPython] Line163  # Draft 2D object (typed FeaturePython)
  ChamferSize = 0
  Closed = false
  End = (120.331,-35.5369,0)
  FilletRadius = 0
  Length = 12.5
  MakeFace = true
  Placement = pos=(107.831,-35.5369,0) rot=(0,0,1;0rad)
  Points = (2) [(0,0,0),(12.5,0,0)]
  Start = (107.831,-35.5369,0)
  Subdivisions = 0
FEATURE [Part::Part2DObjectPython] Line164  # Draft 2D object (typed FeaturePython)
  ChamferSize = 0
  Closed = false
  End = (121.081,-22.2869,0)
  FilletRadius = 0
  Length = 12.5
  MakeFace = true
  Placement = pos=(121.081,-34.7869,0) rot=(0,0,1;0rad)
  Points = (2) [(0,0,0),(0,12.5,0)]
  Start = (121.081,-34.7869,0)
  Subdivisions = 0
FEATURE [Part::Part2DObjectPython] Line165  # Draft 2D object (typed FeaturePython)
  ChamferSize = 0
  Closed = false
  End = (107.831,-21.5369,0)
  FilletRadius = 0
  Length = 12.5
  MakeFace = true
  Placement = pos=(120.331,-21.5369,0) rot=(0,0,1;0rad)
  Points = (2) [(0,0,0),(-12.5,3.55271e-15,0)]
  Start = (120.331,-21.5369,0)
  Subdivisions = 0
FEATURE [App::DocumentObjectGroup] Group022
  Group = -> [Arc082,Arc083,Arc080,Arc081,Line164,Line165,Line161,Line163]
FEATURE [Part::Part2DObjectPython] Arc084  # Draft 2D object (typed FeaturePython)
  FirstAngle = 90
  LastAngle = 180
  MakeFace = true
  Placement = pos=(126.841,-34.7869,0) rot=(0,0,1;1.5708rad)
  Radius = 0.75
FEATURE [Part::Part2DObjectPython] Line169  # Draft 2D object (typed FeaturePython)
  ChamferSize = 0
  Closed = false
  End = (126.841,-21.5369,0)
  FilletRadius = 0
  Length = 12.5
  MakeFace = true
  Placement = pos=(139.341,-21.5369,0) rot=(0,0,1;0rad)
  Points = (2) [(0,0,0),(-12.5,3.55271e-15,0)]
  Start = (139.341,-21.5369,0)
  Subdivisions = 0
FEATURE [Part::Part2DObjectPython] Line170  # Draft 2D object (typed FeaturePython)
  ChamferSize = 0
  Closed = false
  End = (126.091,-34.7869,0)
  FilletRadius = 0
  Length = 12.5
  MakeFace = true
  Placement = pos=(126.091,-22.2869,0) rot=(0,0,1;0rad)
  Points = (2) [(0,0,0),(0,-12.5,0)]
  Start = (126.091,-22.2869,0)
  Subdivisions = 0
FEATURE [Part::Part2DObjectPython] Arc085  # Draft 2D object (typed FeaturePython)
  FirstAngle = 90
  LastAngle = 180
  MakeFace = true
  Placement = pos=(139.341,-34.7869,0) rot=(0,0,1;3.14159rad)
  Radius = 0.75
FEATURE [Part::Part2DObjectPython] Line173  # Draft 2D object (typed FeaturePython)
  ChamferSize = 0
  Closed = false
  End = (139.341,-35.5369,0)
  FilletRadius = 0
  Length = 12.5
  MakeFace = true
  Placement = pos=(126.841,-35.5369,0) rot=(0,0,1;0rad)
  Points = (2) [(0,0,0),(12.5,0,0)]
  Start = (126.841,-35.5369,0)
  Subdivisions = 0
FEATURE [Part::Part2DObjectPython] Arc086  # Draft 2D object (typed FeaturePython)
  FirstAngle = 90
  LastAngle = 180
  MakeFace = true
  Placement = pos=(139.341,-22.2869,0) rot=(0,0,-1;1.5708rad)
  Radius = 0.75
FEATURE [Part::Part2DObjectPython] Arc087  # Draft 2D object (typed FeaturePython)
  FirstAngle = 90
  LastAngle = 180
  MakeFace = true
  Placement = pos=(126.841,-22.2869,0) rot=(0,0,1;0rad)
  Radius = 0.75
FEATURE [Part::Part2DObjectPython] Line176  # Draft 2D object (typed FeaturePython)
  ChamferSize = 0
  Closed = false
  End = (140.091,-22.2869,0)
  FilletRadius = 0
  Length = 12.5
  MakeFace = true
  Placement = pos=(140.091,-34.7869,0) rot=(0,0,1;0rad)
  Points = (2) [(0,0,0),(0,12.5,0)]
  Start = (140.091,-34.7869,0)
  Subdivisions = 0
FEATURE [App::DocumentObjectGroup] Group023
  Group = -> [Arc087,Arc086,Arc084,Arc085,Line176,Line169,Line170,Line173]
FEATURE [Part::Part2DObjectPython] Arc088  # Draft 2D object (typed FeaturePython)
  FirstAngle = 90
  LastAngle = 180
  MakeFace = true
  Placement = pos=(145.85,-22.2869,0) rot=(0,0,1;0rad)
  Radius = 0.75
FEATURE [Part::Part2DObjectPython] Line178  # Draft 2D object (typed FeaturePython)
  ChamferSize = 0
  Closed = false
  End = (145.1,-34.7869,0)
  FilletRadius = 0
  Length = 12.5
  MakeFace = true
  Placement = pos=(145.1,-22.2869,0) rot=(0,0,1;0rad)
  Points = (2) [(0,0,0),(0,-12.5,0)]
  Start = (145.1,-22.2869,0)
  Subdivisions = 0
FEATURE [Part::Part2DObjectPython] Arc089  # Draft 2D object (typed FeaturePython)
  FirstAngle = 90
  LastAngle = 180
  MakeFace = true
  Placement = pos=(158.35,-22.2869,0) rot=(0,0,-1;1.5708rad)
  Radius = 0.75
FEATURE [Part::Part2DObjectPython] Arc090  # Draft 2D object (typed FeaturePython)
  FirstAngle = 90
  LastAngle = 180
  MakeFace = true
  Placement = pos=(158.35,-34.7869,0) rot=(0,0,1;3.14159rad)
  Radius = 0.75
FEATURE [Part::Part2DObjectPython] Arc091  # Draft 2D object (typed FeaturePython)
  FirstAngle = 90
  LastAngle = 180
  MakeFace = true
  Placement = pos=(145.85,-34.7869,0) rot=(0,0,1;1.5708rad)
  Radius = 0.75
FEATURE [Part::Part2DObjectPython] Line179  # Draft 2D object (typed FeaturePython)
  ChamferSize = 0
  Closed = false
  End = (145.85,-21.5369,0)
  FilletRadius = 0
  Length = 12.5
  MakeFace = true
  Placement = pos=(158.35,-21.5369,0) rot=(0,0,1;0rad)
  Points = (2) [(0,0,0),(-12.5,3.55271e-15,0)]
  Start = (158.35,-21.5369,0)
  Subdivisions = 0
FEATURE [Part::Part2DObjectPython] Line182  # Draft 2D object (typed FeaturePython)
  ChamferSize = 0
  Closed = false
  End = (158.35,-35.5369,0)
  FilletRadius = 0
  Length = 12.5
  MakeFace = true
  Placement = pos=(145.85,-35.5369,0) rot=(0,0,1;0rad)
  Points = (2) [(0,0,0),(12.5,0,0)]
  Start = (145.85,-35.5369,0)
  Subdivisions = 0
FEATURE [Part::Part2DObjectPython] Line184  # Draft 2D object (typed FeaturePython)
  ChamferSize = 0
  Closed = false
  End = (159.1,-22.2869,0)
  FilletRadius = 0
  Length = 12.5
  MakeFace = true
  Placement = pos=(159.1,-34.7869,0) rot=(0,0,1;0rad)
  Points = (2) [(0,0,0),(0,12.5,0)]
  Start = (159.1,-34.7869,0)
  Subdivisions = 0
FEATURE [App::DocumentObjectGroup] Group024
  Group = -> [Arc088,Arc089,Arc091,Arc090,Line184,Line179,Line178,Line182]
FEATURE [Part::Part2DObjectPython] Arc092  # Draft 2D object (typed FeaturePython)
  FirstAngle = 90
  LastAngle = 180
  MakeFace = true
  Placement = pos=(177.362,-22.2869,0) rot=(0,0,-1;1.5708rad)
  Radius = 0.75
FEATURE [Part::Part2DObjectPython] Arc093  # Draft 2D object (typed FeaturePython)
  FirstAngle = 90
  LastAngle = 180
  MakeFace = true
  Placement = pos=(164.862,-22.2869,0) rot=(0,0,1;0rad)
  Radius = 0.75
FEATURE [Part::Part2DObjectPython] Line186  # Draft 2D object (typed FeaturePython)
  ChamferSize = 0
  Closed = false
  End = (164.112,-34.7869,0)
  FilletRadius = 0
  Length = 12.5
  MakeFace = true
  Placement = pos=(164.112,-22.2869,0) rot=(0,0,1;0rad)
  Points = (2) [(0,0,0),(0,-12.5,0)]
  Start = (164.112,-22.2869,0)
  Subdivisions = 0
FEATURE [Part::Part2DObjectPython] Arc094  # Draft 2D object (typed FeaturePython)
  FirstAngle = 90
  LastAngle = 180
  MakeFace = true
  Placement = pos=(177.362,-34.7869,0) rot=(0,0,1;3.14159rad)
  Radius = 0.75
FEATURE [Part::Part2DObjectPython] Line188  # Draft 2D object (typed FeaturePython)
  ChamferSize = 0
  Closed = false
  End = (178.112,-22.2869,0)
  FilletRadius = 0
  Length = 12.5
  MakeFace = true
  Placement = pos=(178.112,-34.7869,0) rot=(0,0,1;0rad)
  Points = (2) [(0,0,0),(0,12.5,0)]
  Start = (178.112,-34.7869,0)
  Subdivisions = 0
FEATURE [Part::Part2DObjectPython] Line191  # Draft 2D object (typed FeaturePython)
  ChamferSize = 0
  Closed = false
  End = (164.862,-21.5369,0)
  FilletRadius = 0
  Length = 12.5
  MakeFace = true
  Placement = pos=(177.362,-21.5369,0) rot=(0,0,1;0rad)
  Points = (2) [(0,0,0),(-12.5,3.55271e-15,0)]
  Start = (177.362,-21.5369,0)
  Subdivisions = 0
FEATURE [Part::Part2DObjectPython] Line192  # Draft 2D object (typed FeaturePython)
  ChamferSize = 0
  Closed = false
  End = (177.362,-35.5369,0)
  FilletRadius = 0
  Length = 12.5
  MakeFace = true
  Placement = pos=(164.862,-35.5369,0) rot=(0,0,1;0rad)
  Points = (2) [(0,0,0),(12.5,0,0)]
  Start = (164.862,-35.5369,0)
  Subdivisions = 0
FEATURE [Part::Part2DObjectPython] Arc095  # Draft 2D object (typed FeaturePython)
  FirstAngle = 90
  LastAngle = 180
  MakeFace = true
  Placement = pos=(164.862,-34.7869,0) rot=(0,0,1;1.5708rad)
  Radius = 0.75
FEATURE [App::DocumentObjectGroup] Group025
  Group = -> [Arc093,Arc092,Arc095,Arc094,Line188,Line191,Line186,Line192]
FEATURE [Part::Part2DObjectPython] Arc096  # Draft 2D object (typed FeaturePython)
  FirstAngle = 90
  LastAngle = 180
  MakeFace = true
  Placement = pos=(196.371,-34.7869,0) rot=(0,0,1;3.14159rad)
  Radius = 0.75
FEATURE [Part::Part2DObjectPython] Arc097  # Draft 2D object (typed FeaturePython)
  FirstAngle = 90
  LastAngle = 180
  MakeFace = true
  Placement = pos=(183.871,-34.7869,0) rot=(0,0,1;1.5708rad)
  Radius = 0.75
FEATURE [Part::Part2DObjectPython] Line195  # Draft 2D object (typed FeaturePython)
  ChamferSize = 0
  Closed = false
  End = (183.121,-34.7869,0)
  FilletRadius = 0
  Length = 12.5
  MakeFace = true
  Placement = pos=(183.121,-22.2869,0) rot=(0,0,1;0rad)
  Points = (2) [(0,0,0),(0,-12.5,0)]
  Start = (183.121,-22.2869,0)
  Subdivisions = 0
FEATURE [Part::Part2DObjectPython] Line196  # Draft 2D object (typed FeaturePython)
  ChamferSize = 0
  Closed = false
  End = (196.371,-35.5369,0)
  FilletRadius = 0
  Length = 12.5
  MakeFace = true
  Placement = pos=(183.871,-35.5369,0) rot=(0,0,1;0rad)
  Points = (2) [(0,0,0),(12.5,0,0)]
  Start = (183.871,-35.5369,0)
  Subdivisions = 0
FEATURE [Part::Part2DObjectPython] Arc098  # Draft 2D object (typed FeaturePython)
  FirstAngle = 90
  LastAngle = 180
  MakeFace = true
  Placement = pos=(196.371,-22.2869,0) rot=(0,0,-1;1.5708rad)
  Radius = 0.75
FEATURE [Part::Part2DObjectPython] Arc099  # Draft 2D object (typed FeaturePython)
  FirstAngle = 90
  LastAngle = 180
  MakeFace = true
  Placement = pos=(183.871,-22.2869,0) rot=(0,0,1;0rad)
  Radius = 0.75
FEATURE [Part::Part2DObjectPython] Line198  # Draft 2D object (typed FeaturePython)
  ChamferSize = 0
  Closed = false
  End = (197.121,-22.2869,0)
  FilletRadius = 0
  Length = 12.5
  MakeFace = true
  Placement = pos=(197.121,-34.7869,0) rot=(0,0,1;0rad)
  Points = (2) [(0,0,0),(0,12.5,0)]
  Start = (197.121,-34.7869,0)
  Subdivisions = 0
FEATURE [Part::Part2DObjectPython] Line200  # Draft 2D object (typed FeaturePython)
  ChamferSize = 0
  Closed = false
  End = (183.871,-21.5369,0)
  FilletRadius = 0
  Length = 12.5
  MakeFace = true
  Placement = pos=(196.371,-21.5369,0) rot=(0,0,1;0rad)
  Points = (2) [(0,0,0),(-12.5,3.55271e-15,0)]
  Start = (196.371,-21.5369,0)
  Subdivisions = 0
FEATURE [App::DocumentObjectGroup] Group026
  Group = -> [Arc099,Arc098,Arc097,Arc096,Line198,Line200,Line195,Line196]
FEATURE [Part::Part2DObjectPython] Arc100  # Draft 2D object (typed FeaturePython)
  FirstAngle = 90
  LastAngle = 180
  MakeFace = true
  Placement = pos=(202.881,-34.7869,0) rot=(0,0,1;1.5708rad)
  Radius = 0.75
FEATURE [Part::Part2DObjectPython] Arc101  # Draft 2D object (typed FeaturePython)
  FirstAngle = 90
  LastAngle = 180
  MakeFace = true
  Placement = pos=(215.381,-34.7869,0) rot=(0,0,1;3.14159rad)
  Radius = 0.75
FEATURE [Part::Part2DObjectPython] Line204  # Draft 2D object (typed FeaturePython)
  ChamferSize = 0
  Closed = false
  End = (202.131,-34.7869,0)
  FilletRadius = 0
  Length = 12.5
  MakeFace = true
  Placement = pos=(202.131,-22.2869,0) rot=(0,0,1;0rad)
  Points = (2) [(0,0,0),(0,-12.5,0)]
  Start = (202.131,-22.2869,0)
  Subdivisions = 0
FEATURE [Part::Part2DObjectPython] Line205  # Draft 2D object (typed FeaturePython)
  ChamferSize = 0
  Closed = false
  End = (215.381,-35.5369,0)
  FilletRadius = 0
  Length = 12.5
  MakeFace = true
  Placement = pos=(202.881,-35.5369,0) rot=(0,0,1;0rad)
  Points = (2) [(0,0,0),(12.5,0,0)]
  Start = (202.881,-35.5369,0)
  Subdivisions = 0
FEATURE [Part::Part2DObjectPython] Arc102  # Draft 2D object (typed FeaturePython)
  FirstAngle = 90
  LastAngle = 180
  MakeFace = true
  Placement = pos=(215.381,-22.2869,0) rot=(0,0,-1;1.5708rad)
  Radius = 0.75
FEATURE [Part::Part2DObjectPython] Arc103  # Draft 2D object (typed FeaturePython)
  FirstAngle = 90
  LastAngle = 180
  MakeFace = true
  Placement = pos=(202.881,-22.2869,0) rot=(0,0,1;0rad)
  Radius = 0.75
FEATURE [Part::Part2DObjectPython] Line206  # Draft 2D object (typed FeaturePython)
  ChamferSize = 0
  Closed = false
  End = (202.881,-21.5369,0)
  FilletRadius = 0
  Length = 12.5
  MakeFace = true
  Placement = pos=(215.381,-21.5369,0) rot=(0,0,1;0rad)
  Points = (2) [(0,0,0),(-12.5,3.55271e-15,0)]
  Start = (215.381,-21.5369,0)
  Subdivisions = 0
FEATURE [Part::Part2DObjectPython] Line207  # Draft 2D object (typed FeaturePython)
  ChamferSize = 0
  Closed = false
  End = (216.131,-22.2869,0)
  FilletRadius = 0
  Length = 12.5
  MakeFace = true
  Placement = pos=(216.131,-34.7869,0) rot=(0,0,1;0rad)
  Points = (2) [(0,0,0),(0,12.5,0)]
  Start = (216.131,-34.7869,0)
  Subdivisions = 0
FEATURE [App::DocumentObjectGroup] Group027
  Group = -> [Arc103,Arc102,Arc100,Arc101,Line207,Line206,Line204,Line205]
FEATURE [Part::Part2DObjectPython] Line211  # Draft 2D object (typed FeaturePython)
  ChamferSize = 0
  Closed = false
  End = (221.14,-34.7869,0)
  FilletRadius = 0
  Length = 12.5
  MakeFace = true
  Placement = pos=(221.14,-22.2869,0) rot=(0,0,1;0rad)
  Points = (2) [(0,0,0),(0,-12.5,0)]
  Start = (221.14,-22.2869,0)
  Subdivisions = 0
FEATURE [Part::Part2DObjectPython] Line212  # Draft 2D object (typed FeaturePython)
  ChamferSize = 0
  Closed = false
  End = (234.39,-35.5369,0)
  FilletRadius = 0
  Length = 12.5
  MakeFace = true
  Placement = pos=(221.89,-35.5369,0) rot=(0,0,1;0rad)
  Points = (2) [(0,0,0),(12.5,0,0)]
  Start = (221.89,-35.5369,0)
  Subdivisions = 0
FEATURE [Part::Part2DObjectPython] Line213  # Draft 2D object (typed FeaturePython)
  ChamferSize = 0
  Closed = false
  End = (235.14,-22.2869,0)
  FilletRadius = 0
  Length = 12.5
  MakeFace = true
  Placement = pos=(235.14,-34.7869,0) rot=(0,0,1;0rad)
  Points = (2) [(0,0,0),(0,12.5,0)]
  Start = (235.14,-34.7869,0)
  Subdivisions = 0
FEATURE [Part::Part2DObjectPython] Arc104  # Draft 2D object (typed FeaturePython)
  FirstAngle = 90
  LastAngle = 180
  MakeFace = true
  Placement = pos=(234.39,-34.7869,0) rot=(0,0,1;3.14159rad)
  Radius = 0.75
FEATURE [Part::Part2DObjectPython] Line215  # Draft 2D object (typed FeaturePython)
  ChamferSize = 0
  Closed = false
  End = (221.89,-21.5369,0)
  FilletRadius = 0
  Length = 12.5
  MakeFace = true
  Placement = pos=(234.39,-21.5369,0) rot=(0,0,1;0rad)
  Points = (2) [(0,0,0),(-12.5,3.55271e-15,0)]
  Start = (234.39,-21.5369,0)
  Subdivisions = 0
FEATURE [Part::Part2DObjectPython] Arc105  # Draft 2D object (typed FeaturePython)
  FirstAngle = 90
  LastAngle = 180
  MakeFace = true
  Placement = pos=(221.89,-34.7869,0) rot=(0,0,1;1.5708rad)
  Radius = 0.75
FEATURE [Part::Part2DObjectPython] Arc106  # Draft 2D object (typed FeaturePython)
  FirstAngle = 90
  LastAngle = 180
  MakeFace = true
  Placement = pos=(234.39,-22.2869,0) rot=(0,0,-1;1.5708rad)
  Radius = 0.75
FEATURE [Part::Part2DObjectPython] Arc107  # Draft 2D object (typed FeaturePython)
  FirstAngle = 90
  LastAngle = 180
  MakeFace = true
  Placement = pos=(221.89,-22.2869,0) rot=(0,0,1;0rad)
  Radius = 0.75
FEATURE [App::DocumentObjectGroup] Group028
  Group = -> [Arc107,Arc106,Arc105,Arc104,Line213,Line215,Line211,Line212]
FEATURE [Part::Part2DObjectPython] Arc108  # Draft 2D object (typed FeaturePython)
  FirstAngle = 90
  LastAngle = 180
  MakeFace = true
  Placement = pos=(240.902,-34.7869,0) rot=(0,0,1;1.5708rad)
  Radius = 0.75
FEATURE [Part::Part2DObjectPython] Line219  # Draft 2D object (typed FeaturePython)
  ChamferSize = 0
  Closed = false
  End = (240.902,-21.5369,0)
  FilletRadius = 0
  Length = 12.5
  MakeFace = true
  Placement = pos=(253.402,-21.5369,0) rot=(0,0,1;0rad)
  Points = (2) [(0,0,0),(-12.5,3.55271e-15,0)]
  Start = (253.402,-21.5369,0)
  Subdivisions = 0
FEATURE [Part::Part2DObjectPython] Arc109  # Draft 2D object (typed FeaturePython)
  FirstAngle = 90
  LastAngle = 180
  MakeFace = true
  Placement = pos=(240.902,-22.2869,0) rot=(0,0,1;0rad)
  Radius = 0.75
FEATURE [Part::Part2DObjectPython] Line220  # Draft 2D object (typed FeaturePython)
  ChamferSize = 0
  Closed = false
  End = (253.402,-35.5369,0)
  FilletRadius = 0
  Length = 12.5
  MakeFace = true
  Placement = pos=(240.902,-35.5369,0) rot=(0,0,1;0rad)
  Points = (2) [(0,0,0),(12.5,0,0)]
  Start = (240.902,-35.5369,0)
  Subdivisions = 0
FEATURE [Part::Part2DObjectPython] Line221  # Draft 2D object (typed FeaturePython)
  ChamferSize = 0
  Closed = false
  End = (240.152,-34.7869,0)
  FilletRadius = 0
  Length = 12.5
  MakeFace = true
  Placement = pos=(240.152,-22.2869,0) rot=(0,0,1;0rad)
  Points = (2) [(0,0,0),(0,-12.5,0)]
  Start = (240.152,-22.2869,0)
  Subdivisions = 0
FEATURE [Part::Part2DObjectPython] Line222  # Draft 2D object (typed FeaturePython)
  ChamferSize = 0
  Closed = false
  End = (254.152,-22.2869,0)
  FilletRadius = 0
  Length = 12.5
  MakeFace = true
  Placement = pos=(254.152,-34.7869,0) rot=(0,0,1;0rad)
  Points = (2) [(0,0,0),(0,12.5,0)]
  Start = (254.152,-34.7869,0)
  Subdivisions = 0
FEATURE [Part::Part2DObjectPython] Arc110  # Draft 2D object (typed FeaturePython)
  FirstAngle = 90
  LastAngle = 180
  MakeFace = true
  Placement = pos=(253.402,-34.7869,0) rot=(0,0,1;3.14159rad)
  Radius = 0.75
FEATURE [Part::Part2DObjectPython] Arc111  # Draft 2D object (typed FeaturePython)
  FirstAngle = 90
  LastAngle = 180
  MakeFace = true
  Placement = pos=(253.402,-22.2869,0) rot=(0,0,-1;1.5708rad)
  Radius = 0.75
FEATURE [App::DocumentObjectGroup] Group029
  Group = -> [Arc109,Arc111,Arc108,Arc110,Line222,Line219,Line221,Line220]
FEATURE [Part::Part2DObjectPython] Arc112  # Draft 2D object (typed FeaturePython)
  FirstAngle = 90
  LastAngle = 180
  MakeFace = true
  Placement = pos=(264.664,-34.7869,0) rot=(0,0,1;1.5708rad)
  Radius = 0.75
FEATURE [Part::Part2DObjectPython] Arc113  # Draft 2D object (typed FeaturePython)
  FirstAngle = 90
  LastAngle = 180
  MakeFace = true
  Placement = pos=(264.664,-22.2869,0) rot=(0,0,1;0rad)
  Radius = 0.75
FEATURE [Part::Part2DObjectPython] Line226  # Draft 2D object (typed FeaturePython)
  ChamferSize = 0
  Closed = false
  End = (263.914,-34.7869,0)
  FilletRadius = 0
  Length = 12.5
  MakeFace = true
  Placement = pos=(263.914,-22.2869,0) rot=(0,0,1;0rad)
  Points = (2) [(0,0,0),(0,-12.5,0)]
  Start = (263.914,-22.2869,0)
  Subdivisions = 0
FEATURE [Part::Part2DObjectPython] Arc114  # Draft 2D object (typed FeaturePython)
  FirstAngle = 90
  LastAngle = 180
  MakeFace = true
  Placement = pos=(277.164,-34.7869,0) rot=(0,0,1;3.14159rad)
  Radius = 0.75
FEATURE [Part::Part2DObjectPython] Line230  # Draft 2D object (typed FeaturePython)
  ChamferSize = 0
  Closed = false
  End = (264.664,-21.5369,0)
  FilletRadius = 0
  Length = 12.5
  MakeFace = true
  Placement = pos=(277.164,-21.5369,0) rot=(0,0,1;0rad)
  Points = (2) [(0,0,0),(-12.5,3.55271e-15,0)]
  Start = (277.164,-21.5369,0)
  Subdivisions = 0
FEATURE [Part::Part2DObjectPython] Line231  # Draft 2D object (typed FeaturePython)
  ChamferSize = 0
  Closed = false
  End = (277.164,-35.5369,0)
  FilletRadius = 0
  Length = 12.5
  MakeFace = true
  Placement = pos=(264.664,-35.5369,0) rot=(0,0,1;0rad)
  Points = (2) [(0,0,0),(12.5,0,0)]
  Start = (264.664,-35.5369,0)
  Subdivisions = 0
FEATURE [Part::Part2DObjectPython] Line232  # Draft 2D object (typed FeaturePython)
  ChamferSize = 0
  Closed = false
  End = (277.914,-22.2869,0)
  FilletRadius = 0
  Length = 12.5
  MakeFace = true
  Placement = pos=(277.914,-34.7869,0) rot=(0,0,1;0rad)
  Points = (2) [(0,0,0),(0,12.5,0)]
  Start = (277.914,-34.7869,0)
  Subdivisions = 0
FEATURE [Part::Part2DObjectPython] Arc115  # Draft 2D object (typed FeaturePython)
  FirstAngle = 90
  LastAngle = 180
  MakeFace = true
  Placement = pos=(277.164,-22.2869,0) rot=(0,0,-1;1.5708rad)
  Radius = 0.75
FEATURE [App::DocumentObjectGroup] Group030
  Group = -> [Arc113,Arc115,Arc112,Arc114,Line232,Line230,Line226,Line231]
FEATURE [Part::Part2DObjectPython] Line233  # Draft 2D object (typed FeaturePython)
  ChamferSize = 0
  Closed = false
  End = (311.48,-22.2869,0)
  FilletRadius = 0
  Length = 12.5
  MakeFace = true
  Placement = pos=(311.48,-34.7869,0) rot=(0,0,1;0rad)
  Points = (2) [(0,0,0),(0,12.5,0)]
  Start = (311.48,-34.7869,0)
  Subdivisions = 0
FEATURE [Part::Part2DObjectPython] Arc116  # Draft 2D object (typed FeaturePython)
  FirstAngle = 90
  LastAngle = 180
  MakeFace = true
  Placement = pos=(310.73,-22.2869,0) rot=(0,0,-1;1.5708rad)
  Radius = 0.75
FEATURE [Part::Part2DObjectPython] Line234  # Draft 2D object (typed FeaturePython)
  ChamferSize = 0
  Closed = false
  End = (310.73,-35.5369,0)
  FilletRadius = 0
  Length = 12.5
  MakeFace = true
  Placement = pos=(298.23,-35.5369,0) rot=(0,0,1;0rad)
  Points = (2) [(0,0,0),(12.5,0,0)]
  Start = (298.23,-35.5369,0)
  Subdivisions = 0
FEATURE [Part::Part2DObjectPython] Line235  # Draft 2D object (typed FeaturePython)
  ChamferSize = 0
  Closed = false
  End = (298.23,-21.5369,0)
  FilletRadius = 0
  Length = 12.5
  MakeFace = true
  Placement = pos=(310.73,-21.5369,0) rot=(0,0,1;0rad)
  Points = (2) [(0,0,0),(-12.5,3.55271e-15,0)]
  Start = (310.73,-21.5369,0)
  Subdivisions = 0
FEATURE [Part::Part2DObjectPython] Arc117  # Draft 2D object (typed FeaturePython)
  FirstAngle = 90
  LastAngle = 180
  MakeFace = true
  Placement = pos=(310.73,-34.7869,0) rot=(0,0,1;3.14159rad)
  Radius = 0.75
FEATURE [Part::Part2DObjectPython] Arc118  # Draft 2D object (typed FeaturePython)
  FirstAngle = 90
  LastAngle = 180
  MakeFace = true
  Placement = pos=(298.23,-34.7869,0) rot=(0,0,1;1.5708rad)
  Radius = 0.75
FEATURE [Part::Part2DObjectPython] Arc119  # Draft 2D object (typed FeaturePython)
  FirstAngle = 90
  LastAngle = 180
  MakeFace = true
  Placement = pos=(298.23,-22.2869,0) rot=(0,0,1;0rad)
  Radius = 0.75
FEATURE [Part::Part2DObjectPython] Line239  # Draft 2D object (typed FeaturePython)
  ChamferSize = 0
  Closed = false
  End = (297.48,-34.7869,0)
  FilletRadius = 0
  Length = 12.5
  MakeFace = true
  Placement = pos=(297.48,-22.2869,0) rot=(0,0,1;0rad)
  Points = (2) [(0,0,0),(0,-12.5,0)]
  Start = (297.48,-22.2869,0)
  Subdivisions = 0
FEATURE [App::DocumentObjectGroup] Group031
  Group = -> [Arc119,Arc116,Arc118,Arc117,Line233,Line235,Line239,Line234]
FEATURE [App::DocumentObjectGroup] Group016  label="Row 2"
  Group = -> [Group017,Group018,Group019,Group020,Group021,Group022,Group023,Group024,Group025,Group026,Group027,Group028,Group029,Group031]
FEATURE [Part::Part2DObjectPython] Arc120  # Draft 2D object (typed FeaturePython)
  FirstAngle = 90
  LastAngle = 180
  MakeFace = true
  Placement = pos=(10.4048,-53.7963,0) rot=(0,0,1;1.5708rad)
  Radius = 0.75
FEATURE [Part::Part2DObjectPython] Arc121  # Draft 2D object (typed FeaturePython)
  FirstAngle = 90
  LastAngle = 180
  MakeFace = true
  Placement = pos=(22.9048,-41.2963,0) rot=(0,0,-1;1.5708rad)
  Radius = 0.75
FEATURE [Part::Part2DObjectPython] Line241  # Draft 2D object (typed FeaturePython)
  ChamferSize = 0
  Closed = false
  End = (23.6548,-41.2963,0)
  FilletRadius = 0
  Length = 12.5
  MakeFace = true
  Placement = pos=(23.6548,-53.7963,0) rot=(0,0,1;0rad)
  Points = (2) [(0,0,0),(0,12.5,0)]
  Start = (23.6548,-53.7963,0)
  Subdivisions = 0
FEATURE [Part::Part2DObjectPython] Line242  # Draft 2D object (typed FeaturePython)
  ChamferSize = 0
  Closed = false
  End = (10.4048,-40.5463,0)
  FilletRadius = 0
  Length = 12.5
  MakeFace = true
  Placement = pos=(22.9048,-40.5463,0) rot=(0,0,1;0rad)
  Points = (2) [(0,0,0),(-12.5,0,0)]
  Start = (22.9048,-40.5463,0)
  Subdivisions = 0
FEATURE [Part::Part2DObjectPython] Arc122  # Draft 2D object (typed FeaturePython)
  FirstAngle = 90
  LastAngle = 180
  MakeFace = true
  Placement = pos=(22.9048,-53.7963,0) rot=(0,0,1;3.14159rad)
  Radius = 0.75
FEATURE [Part::Part2DObjectPython] Line244  # Draft 2D object (typed FeaturePython)
  ChamferSize = 0
  Closed = false
  End = (22.9048,-54.5463,0)
  FilletRadius = 0
  Length = 12.5
  MakeFace = true
  Placement = pos=(10.4048,-54.5463,0) rot=(0,0,1;0rad)
  Points = (2) [(0,0,0),(12.5,0,0)]
  Start = (10.4048,-54.5463,0)
  Subdivisions = 0
FEATURE [Part::Part2DObjectPython] Arc123  # Draft 2D object (typed FeaturePython)
  FirstAngle = 90
  LastAngle = 180
  MakeFace = true
  Placement = pos=(10.4048,-41.2963,0) rot=(0,0,1;0rad)
  Radius = 0.75
FEATURE [Part::Part2DObjectPython] Line246  # Draft 2D object (typed FeaturePython)
  ChamferSize = 0
  Closed = false
  End = (9.65477,-53.7963,0)
  FilletRadius = 0
  Length = 12.5
  MakeFace = true
  Placement = pos=(9.65477,-41.2963,0) rot=(0,0,1;0rad)
  Points = (2) [(0,0,0),(0,-12.5,0)]
  Start = (9.65477,-41.2963,0)
  Subdivisions = 0
FEATURE [App::DocumentObjectGroup] Group033
  Group = -> [Arc123,Arc121,Arc120,Arc122,Line241,Line242,Line246,Line244]
FEATURE [Part::Part2DObjectPython] Line249  # Draft 2D object (typed FeaturePython)
  ChamferSize = 0
  Closed = false
  End = (49.7939,-41.2963,0)
  FilletRadius = 0
  Length = 12.5
  MakeFace = true
  Placement = pos=(49.7939,-53.7963,0) rot=(0,0,1;0rad)
  Points = (2) [(0,0,0),(0,12.5,0)]
  Start = (49.7939,-53.7963,0)
  Subdivisions = 0
FEATURE [Part::Part2DObjectPython] Arc124  # Draft 2D object (typed FeaturePython)
  FirstAngle = 90
  LastAngle = 180
  MakeFace = true
  Placement = pos=(36.5439,-41.2963,0) rot=(0,0,1;0rad)
  Radius = 0.75
FEATURE [Part::Part2DObjectPython] Line251  # Draft 2D object (typed FeaturePython)
  ChamferSize = 0
  Closed = false
  End = (36.5439,-40.5463,0)
  FilletRadius = 0
  Length = 12.5
  MakeFace = true
  Placement = pos=(49.0439,-40.5463,0) rot=(0,0,1;0rad)
  Points = (2) [(0,0,0),(-12.5,0,0)]
  Start = (49.0439,-40.5463,0)
  Subdivisions = 0
FEATURE [Part::Part2DObjectPython] Line253  # Draft 2D object (typed FeaturePython)
  ChamferSize = 0
  Closed = false
  End = (35.7939,-53.7963,0)
  FilletRadius = 0
  Length = 12.5
  MakeFace = true
  Placement = pos=(35.7939,-41.2963,0) rot=(0,0,1;0rad)
  Points = (2) [(0,0,0),(0,-12.5,0)]
  Start = (35.7939,-41.2963,0)
  Subdivisions = 0
FEATURE [Part::Part2DObjectPython] Arc125  # Draft 2D object (typed FeaturePython)
  FirstAngle = 90
  LastAngle = 180
  MakeFace = true
  Placement = pos=(49.0439,-41.2963,0) rot=(0,0,-1;1.5708rad)
  Radius = 0.75
FEATURE [Part::Part2DObjectPython] Arc126  # Draft 2D object (typed FeaturePython)
  FirstAngle = 90
  LastAngle = 180
  MakeFace = true
  Placement = pos=(49.0439,-53.7963,0) rot=(0,0,1;3.14159rad)
  Radius = 0.75
FEATURE [Part::Part2DObjectPython] Arc127  # Draft 2D object (typed FeaturePython)
  FirstAngle = 90
  LastAngle = 180
  MakeFace = true
  Placement = pos=(36.5439,-53.7963,0) rot=(0,0,1;1.5708rad)
  Radius = 0.75
FEATURE [Part::Part2DObjectPython] Line255  # Draft 2D object (typed FeaturePython)
  ChamferSize = 0
  Closed = false
  End = (49.0439,-54.5463,0)
  FilletRadius = 0
  Length = 12.5
  MakeFace = true
  Placement = pos=(36.5439,-54.5463,0) rot=(0,0,1;0rad)
  Points = (2) [(0,0,0),(12.5,0,0)]
  Start = (36.5439,-54.5463,0)
  Subdivisions = 0
FEATURE [App::DocumentObjectGroup] Group034
  Group = -> [Arc124,Arc125,Arc127,Arc126,Line249,Line251,Line253,Line255]
FEATURE [Part::Part2DObjectPython] Arc128  # Draft 2D object (typed FeaturePython)
  FirstAngle = 90
  LastAngle = 180
  MakeFace = true
  Placement = pos=(55.5532,-41.2963,0) rot=(0,0,1;0rad)
  Radius = 0.75
FEATURE [Part::Part2DObjectPython] Arc129  # Draft 2D object (typed FeaturePython)
  FirstAngle = 90
  LastAngle = 180
  MakeFace = true
  Placement = pos=(55.5532,-53.7963,0) rot=(0,0,1;1.5708rad)
  Radius = 0.75
FEATURE [Part::Part2DObjectPython] Arc130  # Draft 2D object (typed FeaturePython)
  FirstAngle = 90
  LastAngle = 180
  MakeFace = true
  Placement = pos=(68.0532,-41.2963,0) rot=(0,0,-1;1.5708rad)
  Radius = 0.75
FEATURE [Part::Part2DObjectPython] Line257  # Draft 2D object (typed FeaturePython)
  ChamferSize = 0
  Closed = false
  End = (55.5532,-40.5463,0)
  FilletRadius = 0
  Length = 12.5
  MakeFace = true
  Placement = pos=(68.0532,-40.5463,0) rot=(0,0,1;0rad)
  Points = (2) [(0,0,0),(-12.5,0,0)]
  Start = (68.0532,-40.5463,0)
  Subdivisions = 0
FEATURE [Part::Part2DObjectPython] Line259  # Draft 2D object (typed FeaturePython)
  ChamferSize = 0
  Closed = false
  End = (68.8032,-41.2963,0)
  FilletRadius = 0
  Length = 12.5
  MakeFace = true
  Placement = pos=(68.8032,-53.7963,0) rot=(0,0,1;0rad)
  Points = (2) [(0,0,0),(0,12.5,0)]
  Start = (68.8032,-53.7963,0)
  Subdivisions = 0
FEATURE [Part::Part2DObjectPython] Line261  # Draft 2D object (typed FeaturePython)
  ChamferSize = 0
  Closed = false
  End = (54.8032,-53.7963,0)
  FilletRadius = 0
  Length = 12.5
  MakeFace = true
  Placement = pos=(54.8032,-41.2963,0) rot=(0,0,1;0rad)
  Points = (2) [(0,0,0),(0,-12.5,0)]
  Start = (54.8032,-41.2963,0)
  Subdivisions = 0
FEATURE [Part::Part2DObjectPython] Arc131  # Draft 2D object (typed FeaturePython)
  FirstAngle = 90
  LastAngle = 180
  MakeFace = true
  Placement = pos=(68.0532,-53.7963,0) rot=(0,0,1;3.14159rad)
  Radius = 0.75
FEATURE [Part::Part2DObjectPython] Line263  # Draft 2D object (typed FeaturePython)
  ChamferSize = 0
  Closed = false
  End = (68.0532,-54.5463,0)
  FilletRadius = 0
  Length = 12.5
  MakeFace = true
  Placement = pos=(55.5532,-54.5463,0) rot=(0,0,1;0rad)
  Points = (2) [(0,0,0),(12.5,0,0)]
  Start = (55.5532,-54.5463,0)
  Subdivisions = 0
FEATURE [App::DocumentObjectGroup] Group035
  Group = -> [Arc128,Arc130,Arc129,Arc131,Line259,Line257,Line261,Line263]
FEATURE [Part::Part2DObjectPython] Arc132  # Draft 2D object (typed FeaturePython)
  FirstAngle = 90
  LastAngle = 180
  MakeFace = true
  Placement = pos=(74.5625,-53.7963,0) rot=(0,0,1;1.5708rad)
  Radius = 0.75
FEATURE [Part::Part2DObjectPython] Arc133  # Draft 2D object (typed FeaturePython)
  FirstAngle = 90
  LastAngle = 180
  MakeFace = true
  Placement = pos=(87.0625,-41.2963,0) rot=(0,0,-1;1.5708rad)
  Radius = 0.75
FEATURE [Part::Part2DObjectPython] Line267  # Draft 2D object (typed FeaturePython)
  ChamferSize = 0
  Closed = false
  End = (74.5625,-40.5463,0)
  FilletRadius = 0
  Length = 12.5
  MakeFace = true
  Placement = pos=(87.0625,-40.5463,0) rot=(0,0,1;0rad)
  Points = (2) [(0,0,0),(-12.5,0,0)]
  Start = (87.0625,-40.5463,0)
  Subdivisions = 0
FEATURE [Part::Part2DObjectPython] Arc134  # Draft 2D object (typed FeaturePython)
  FirstAngle = 90
  LastAngle = 180
  MakeFace = true
  Placement = pos=(74.5625,-41.2963,0) rot=(0,0,1;0rad)
  Radius = 0.75
FEATURE [Part::Part2DObjectPython] Arc135  # Draft 2D object (typed FeaturePython)
  FirstAngle = 90
  LastAngle = 180
  MakeFace = true
  Placement = pos=(87.0625,-53.7963,0) rot=(0,0,1;3.14159rad)
  Radius = 0.75
FEATURE [Part::Part2DObjectPython] Line270  # Draft 2D object (typed FeaturePython)
  ChamferSize = 0
  Closed = false
  End = (87.8125,-41.2963,0)
  FilletRadius = 0
  Length = 12.5
  MakeFace = true
  Placement = pos=(87.8125,-53.7963,0) rot=(0,0,1;0rad)
  Points = (2) [(0,0,0),(0,12.5,0)]
  Start = (87.8125,-53.7963,0)
  Subdivisions = 0
FEATURE [Part::Part2DObjectPython] Line271  # Draft 2D object (typed FeaturePython)
  ChamferSize = 0
  Closed = false
  End = (73.8125,-53.7963,0)
  FilletRadius = 0
  Length = 12.5
  MakeFace = true
  Placement = pos=(73.8125,-41.2963,0) rot=(0,0,1;0rad)
  Points = (2) [(0,0,0),(0,-12.5,0)]
  Start = (73.8125,-41.2963,0)
  Subdivisions = 0
FEATURE [Part::Part2DObjectPython] Line272  # Draft 2D object (typed FeaturePython)
  ChamferSize = 0
  Closed = false
  End = (87.0625,-54.5463,0)
  FilletRadius = 0
  Length = 12.5
  MakeFace = true
  Placement = pos=(74.5625,-54.5463,0) rot=(0,0,1;0rad)
  Points = (2) [(0,0,0),(12.5,0,0)]
  Start = (74.5625,-54.5463,0)
  Subdivisions = 0
FEATURE [App::DocumentObjectGroup] Group036
  Group = -> [Arc134,Arc133,Arc132,Arc135,Line270,Line267,Line271,Line272]
FEATURE [Part::Part2DObjectPython] Line273  # Draft 2D object (typed FeaturePython)
  ChamferSize = 0
  Closed = false
  End = (106.074,-54.5463,0)
  FilletRadius = 0
  Length = 12.5
  MakeFace = true
  Placement = pos=(93.5744,-54.5463,0) rot=(0,0,1;0rad)
  Points = (2) [(0,0,0),(12.5,0,0)]
  Start = (93.5744,-54.5463,0)
  Subdivisions = 0
FEATURE [Part::Part2DObjectPython] Arc136  # Draft 2D object (typed FeaturePython)
  FirstAngle = 90
  LastAngle = 180
  MakeFace = true
  Placement = pos=(93.5744,-53.7963,0) rot=(0,0,1;1.5708rad)
  Radius = 0.75
FEATURE [Part::Part2DObjectPython] Line276  # Draft 2D object (typed FeaturePython)
  ChamferSize = 0
  Closed = false
  End = (92.8244,-53.7963,0)
  FilletRadius = 0
  Length = 12.5
  MakeFace = true
  Placement = pos=(92.8244,-41.2963,0) rot=(0,0,1;0rad)
  Points = (2) [(0,0,0),(0,-12.5,0)]
  Start = (92.8244,-41.2963,0)
  Subdivisions = 0
FEATURE [Part::Part2DObjectPython] Arc137  # Draft 2D object (typed FeaturePython)
  FirstAngle = 90
  LastAngle = 180
  MakeFace = true
  Placement = pos=(106.074,-41.2963,0) rot=(0,0,-1;1.5708rad)
  Radius = 0.75
FEATURE [Part::Part2DObjectPython] Line277  # Draft 2D object (typed FeaturePython)
  ChamferSize = 0
  Closed = false
  End = (93.5744,-40.5463,0)
  FilletRadius = 0
  Length = 12.5
  MakeFace = true
  Placement = pos=(106.074,-40.5463,0) rot=(0,0,1;0rad)
  Points = (2) [(0,0,0),(-12.5,0,0)]
  Start = (106.074,-40.5463,0)
  Subdivisions = 0
FEATURE [Part::Part2DObjectPython] Arc138  # Draft 2D object (typed FeaturePython)
  FirstAngle = 90
  LastAngle = 180
  MakeFace = true
  Placement = pos=(106.074,-53.7963,0) rot=(0,0,1;3.14159rad)
  Radius = 0.75
FEATURE [Part::Part2DObjectPython] Line279  # Draft 2D object (typed FeaturePython)
  ChamferSize = 0
  Closed = false
  End = (106.824,-41.2963,0)
  FilletRadius = 0
  Length = 12.5
  MakeFace = true
  Placement = pos=(106.824,-53.7963,0) rot=(0,0,1;0rad)
  Points = (2) [(0,0,0),(0,12.5,0)]
  Start = (106.824,-53.7963,0)
  Subdivisions = 0
FEATURE [Part::Part2DObjectPython] Arc139  # Draft 2D object (typed FeaturePython)
  FirstAngle = 90
  LastAngle = 180
  MakeFace = true
  Placement = pos=(93.5744,-41.2963,0) rot=(0,0,1;0rad)
  Radius = 0.75
FEATURE [App::DocumentObjectGroup] Group037
  Group = -> [Arc139,Arc137,Arc136,Arc138,Line279,Line277,Line276,Line273]
FEATURE [Part::Part2DObjectPython] Line281  # Draft 2D object (typed FeaturePython)
  ChamferSize = 0
  Closed = false
  End = (111.834,-53.7963,0)
  FilletRadius = 0
  Length = 12.5
  MakeFace = true
  Placement = pos=(111.834,-41.2963,0) rot=(0,0,1;0rad)
  Points = (2) [(0,0,0),(0,-12.5,0)]
  Start = (111.834,-41.2963,0)
  Subdivisions = 0
FEATURE [Part::Part2DObjectPython] Arc140  # Draft 2D object (typed FeaturePython)
  FirstAngle = 90
  LastAngle = 180
  MakeFace = true
  Placement = pos=(125.084,-41.2963,0) rot=(0,0,-1;1.5708rad)
  Radius = 0.75
FEATURE [Part::Part2DObjectPython] Line282  # Draft 2D object (typed FeaturePython)
  ChamferSize = 0
  Closed = false
  End = (112.584,-40.5463,0)
  FilletRadius = 0
  Length = 12.5
  MakeFace = true
  Placement = pos=(125.084,-40.5463,0) rot=(0,0,1;0rad)
  Points = (2) [(0,0,0),(-12.5,0,0)]
  Start = (125.084,-40.5463,0)
  Subdivisions = 0
FEATURE [Part::Part2DObjectPython] Line284  # Draft 2D object (typed FeaturePython)
  ChamferSize = 0
  Closed = false
  End = (125.084,-54.5463,0)
  FilletRadius = 0
  Length = 12.5
  MakeFace = true
  Placement = pos=(112.584,-54.5463,0) rot=(0,0,1;0rad)
  Points = (2) [(0,0,0),(12.5,0,0)]
  Start = (112.584,-54.5463,0)
  Subdivisions = 0
FEATURE [Part::Part2DObjectPython] Arc141  # Draft 2D object (typed FeaturePython)
  FirstAngle = 90
  LastAngle = 180
  MakeFace = true
  Placement = pos=(112.584,-53.7963,0) rot=(0,0,1;1.5708rad)
  Radius = 0.75
FEATURE [Part::Part2DObjectPython] Arc142  # Draft 2D object (typed FeaturePython)
  FirstAngle = 90
  LastAngle = 180
  MakeFace = true
  Placement = pos=(125.084,-53.7963,0) rot=(0,0,1;3.14159rad)
  Radius = 0.75
FEATURE [Part::Part2DObjectPython] Line287  # Draft 2D object (typed FeaturePython)
  ChamferSize = 0
  Closed = false
  End = (125.834,-41.2963,0)
  FilletRadius = 0
  Length = 12.5
  MakeFace = true
  Placement = pos=(125.834,-53.7963,0) rot=(0,0,1;0rad)
  Points = (2) [(0,0,0),(0,12.5,0)]
  Start = (125.834,-53.7963,0)
  Subdivisions = 0
FEATURE [Part::Part2DObjectPython] Arc143  # Draft 2D object (typed FeaturePython)
  FirstAngle = 90
  LastAngle = 180
  MakeFace = true
  Placement = pos=(112.584,-41.2963,0) rot=(0,0,1;0rad)
  Radius = 0.75
FEATURE [App::DocumentObjectGroup] Group038
  Group = -> [Arc143,Arc140,Arc141,Arc142,Line287,Line282,Line281,Line284]
FEATURE [Part::Part2DObjectPython] Arc144  # Draft 2D object (typed FeaturePython)
  FirstAngle = 90
  LastAngle = 180
  MakeFace = true
  Placement = pos=(144.093,-53.7963,0) rot=(0,0,1;3.14159rad)
  Radius = 0.75
FEATURE [Part::Part2DObjectPython] Arc145  # Draft 2D object (typed FeaturePython)
  FirstAngle = 90
  LastAngle = 180
  MakeFace = true
  Placement = pos=(131.593,-41.2963,0) rot=(0,0,1;0rad)
  Radius = 0.75
FEATURE [Part::Part2DObjectPython] Line289  # Draft 2D object (typed FeaturePython)
  ChamferSize = 0
  Closed = false
  End = (144.843,-41.2963,0)
  FilletRadius = 0
  Length = 12.5
  MakeFace = true
  Placement = pos=(144.843,-53.7963,0) rot=(0,0,1;0rad)
  Points = (2) [(0,0,0),(0,12.5,0)]
  Start = (144.843,-53.7963,0)
  Subdivisions = 0
FEATURE [Part::Part2DObjectPython] Arc146  # Draft 2D object (typed FeaturePython)
  FirstAngle = 90
  LastAngle = 180
  MakeFace = true
  Placement = pos=(131.593,-53.7963,0) rot=(0,0,1;1.5708rad)
  Radius = 0.75
FEATURE [Part::Part2DObjectPython] Arc147  # Draft 2D object (typed FeaturePython)
  FirstAngle = 90
  LastAngle = 180
  MakeFace = true
  Placement = pos=(144.093,-41.2963,0) rot=(0,0,-1;1.5708rad)
  Radius = 0.75
FEATURE [Part::Part2DObjectPython] Line293  # Draft 2D object (typed FeaturePython)
  ChamferSize = 0
  Closed = false
  End = (130.843,-53.7963,0)
  FilletRadius = 0
  Length = 12.5
  MakeFace = true
  Placement = pos=(130.843,-41.2963,0) rot=(0,0,1;0rad)
  Points = (2) [(0,0,0),(0,-12.5,0)]
  Start = (130.843,-41.2963,0)
  Subdivisions = 0
FEATURE [Part::Part2DObjectPython] Line294  # Draft 2D object (typed FeaturePython)
  ChamferSize = 0
  Closed = false
  End = (131.593,-40.5463,0)
  FilletRadius = 0
  Length = 12.5
  MakeFace = true
  Placement = pos=(144.093,-40.5463,0) rot=(0,0,1;0rad)
  Points = (2) [(0,0,0),(-12.5,0,0)]
  Start = (144.093,-40.5463,0)
  Subdivisions = 0
FEATURE [Part::Part2DObjectPython] Line296  # Draft 2D object (typed FeaturePython)
  ChamferSize = 0
  Closed = false
  End = (144.093,-54.5463,0)
  FilletRadius = 0
  Length = 12.5
  MakeFace = true
  Placement = pos=(131.593,-54.5463,0) rot=(0,0,1;0rad)
  Points = (2) [(0,0,0),(12.5,0,0)]
  Start = (131.593,-54.5463,0)
  Subdivisions = 0
FEATURE [App::DocumentObjectGroup] Group039
  Group = -> [Arc145,Arc147,Arc146,Arc144,Line289,Line294,Line293,Line296]
FEATURE [Part::Part2DObjectPython] Arc148  # Draft 2D object (typed FeaturePython)
  FirstAngle = 90
  LastAngle = 180
  MakeFace = true
  Placement = pos=(163.102,-41.2963,0) rot=(0,0,-1;1.5708rad)
  Radius = 0.75
FEATURE [Part::Part2DObjectPython] Line298  # Draft 2D object (typed FeaturePython)
  ChamferSize = 0
  Closed = false
  End = (163.852,-41.2963,0)
  FilletRadius = 0
  Length = 12.5
  MakeFace = true
  Placement = pos=(163.852,-53.7963,0) rot=(0,0,1;0rad)
  Points = (2) [(0,0,0),(0,12.5,0)]
  Start = (163.852,-53.7963,0)
  Subdivisions = 0
FEATURE [Part::Part2DObjectPython] Line299  # Draft 2D object (typed FeaturePython)
  ChamferSize = 0
  Closed = false
  End = (150.602,-40.5463,0)
  FilletRadius = 0
  Length = 12.5
  MakeFace = true
  Placement = pos=(163.102,-40.5463,0) rot=(0,0,1;0rad)
  Points = (2) [(0,0,0),(-12.5,0,0)]
  Start = (163.102,-40.5463,0)
  Subdivisions = 0
FEATURE [Part::Part2DObjectPython] Arc149  # Draft 2D object (typed FeaturePython)
  FirstAngle = 90
  LastAngle = 180
  MakeFace = true
  Placement = pos=(150.602,-53.7963,0) rot=(0,0,1;1.5708rad)
  Radius = 0.75
FEATURE [Part::Part2DObjectPython] Line301  # Draft 2D object (typed FeaturePython)
  ChamferSize = 0
  Closed = false
  End = (149.852,-53.7963,0)
  FilletRadius = 0
  Length = 12.5
  MakeFace = true
  Placement = pos=(149.852,-41.2963,0) rot=(0,0,1;0rad)
  Points = (2) [(0,0,0),(0,-12.5,0)]
  Start = (149.852,-41.2963,0)
  Subdivisions = 0
FEATURE [Part::Part2DObjectPython] Arc150  # Draft 2D object (typed FeaturePython)
  FirstAngle = 90
  LastAngle = 180
  MakeFace = true
  Placement = pos=(150.602,-41.2963,0) rot=(0,0,1;0rad)
  Radius = 0.75
FEATURE [Part::Part2DObjectPython] Line303  # Draft 2D object (typed FeaturePython)
  ChamferSize = 0
  Closed = false
  End = (163.102,-54.5463,0)
  FilletRadius = 0
  Length = 12.5
  MakeFace = true
  Placement = pos=(150.602,-54.5463,0) rot=(0,0,1;0rad)
  Points = (2) [(0,0,0),(12.5,0,0)]
  Start = (150.602,-54.5463,0)
  Subdivisions = 0
FEATURE [Part::Part2DObjectPython] Arc151  # Draft 2D object (typed FeaturePython)
  FirstAngle = 90
  LastAngle = 180
  MakeFace = true
  Placement = pos=(163.102,-53.7963,0) rot=(0,0,1;3.14159rad)
  Radius = 0.75
FEATURE [App::DocumentObjectGroup] Group040
  Group = -> [Arc150,Arc148,Arc149,Arc151,Line298,Line299,Line301,Line303]
FEATURE [Part::Part2DObjectPython] Line305  # Draft 2D object (typed FeaturePython)
  ChamferSize = 0
  Closed = false
  End = (169.614,-40.5463,0)
  FilletRadius = 0
  Length = 12.5
  MakeFace = true
  Placement = pos=(182.114,-40.5463,0) rot=(0,0,1;0rad)
  Points = (2) [(0,0,0),(-12.5,0,0)]
  Start = (182.114,-40.5463,0)
  Subdivisions = 0
FEATURE [Part::Part2DObjectPython] Line306  # Draft 2D object (typed FeaturePython)
  ChamferSize = 0
  Closed = false
  End = (182.864,-41.2963,0)
  FilletRadius = 0
  Length = 12.5
  MakeFace = true
  Placement = pos=(182.864,-53.7963,0) rot=(0,0,1;0rad)
  Points = (2) [(0,0,0),(0,12.5,0)]
  Start = (182.864,-53.7963,0)
  Subdivisions = 0
FEATURE [Part::Part2DObjectPython] Arc152  # Draft 2D object (typed FeaturePython)
  FirstAngle = 90
  LastAngle = 180
  MakeFace = true
  Placement = pos=(169.614,-53.7963,0) rot=(0,0,1;1.5708rad)
  Radius = 0.75
FEATURE [Part::Part2DObjectPython] Arc153  # Draft 2D object (typed FeaturePython)
  FirstAngle = 90
  LastAngle = 180
  MakeFace = true
  Placement = pos=(182.114,-41.2963,0) rot=(0,0,-1;1.5708rad)
  Radius = 0.75
FEATURE [Part::Part2DObjectPython] Line309  # Draft 2D object (typed FeaturePython)
  ChamferSize = 0
  Closed = false
  End = (168.864,-53.7963,0)
  FilletRadius = 0
  Length = 12.5
  MakeFace = true
  Placement = pos=(168.864,-41.2963,0) rot=(0,0,1;0rad)
  Points = (2) [(0,0,0),(0,-12.5,0)]
  Start = (168.864,-41.2963,0)
  Subdivisions = 0
FEATURE [Part::Part2DObjectPython] Arc154  # Draft 2D object (typed FeaturePython)
  FirstAngle = 90
  LastAngle = 180
  MakeFace = true
  Placement = pos=(169.614,-41.2963,0) rot=(0,0,1;0rad)
  Radius = 0.75
FEATURE [Part::Part2DObjectPython] Line311  # Draft 2D object (typed FeaturePython)
  ChamferSize = 0
  Closed = false
  End = (182.114,-54.5463,0)
  FilletRadius = 0
  Length = 12.5
  MakeFace = true
  Placement = pos=(169.614,-54.5463,0) rot=(0,0,1;0rad)
  Points = (2) [(0,0,0),(12.5,0,0)]
  Start = (169.614,-54.5463,0)
  Subdivisions = 0
FEATURE [Part::Part2DObjectPython] Arc155  # Draft 2D object (typed FeaturePython)
  FirstAngle = 90
  LastAngle = 180
  MakeFace = true
  Placement = pos=(182.114,-53.7963,0) rot=(0,0,1;3.14159rad)
  Radius = 0.75
FEATURE [App::DocumentObjectGroup] Group041
  Group = -> [Arc154,Arc153,Arc152,Arc155,Line306,Line305,Line309,Line311]
FEATURE [Part::Part2DObjectPython] Line314  # Draft 2D object (typed FeaturePython)
  ChamferSize = 0
  Closed = false
  End = (201.874,-41.2963,0)
  FilletRadius = 0
  Length = 12.5
  MakeFace = true
  Placement = pos=(201.874,-53.7963,0) rot=(0,0,1;0rad)
  Points = (2) [(0,0,0),(0,12.5,0)]
  Start = (201.874,-53.7963,0)
  Subdivisions = 0
FEATURE [Part::Part2DObjectPython] Arc156  # Draft 2D object (typed FeaturePython)
  FirstAngle = 90
  LastAngle = 180
  MakeFace = true
  Placement = pos=(201.124,-53.7963,0) rot=(0,0,1;3.14159rad)
  Radius = 0.75
FEATURE [Part::Part2DObjectPython] Arc157  # Draft 2D object (typed FeaturePython)
  FirstAngle = 90
  LastAngle = 180
  MakeFace = true
  Placement = pos=(201.124,-41.2963,0) rot=(0,0,-1;1.5708rad)
  Radius = 0.75
FEATURE [Part::Part2DObjectPython] Line316  # Draft 2D object (typed FeaturePython)
  ChamferSize = 0
  Closed = false
  End = (201.124,-54.5463,0)
  FilletRadius = 0
  Length = 12.5
  MakeFace = true
  Placement = pos=(188.624,-54.5463,0) rot=(0,0,1;0rad)
  Points = (2) [(0,0,0),(12.5,0,0)]
  Start = (188.624,-54.5463,0)
  Subdivisions = 0
FEATURE [Part::Part2DObjectPython] Line317  # Draft 2D object (typed FeaturePython)
  ChamferSize = 0
  Closed = false
  End = (187.874,-53.7963,0)
  FilletRadius = 0
  Length = 12.5
  MakeFace = true
  Placement = pos=(187.874,-41.2963,0) rot=(0,0,1;0rad)
  Points = (2) [(0,0,0),(0,-12.5,0)]
  Start = (187.874,-41.2963,0)
  Subdivisions = 0
FEATURE [Part::Part2DObjectPython] Line319  # Draft 2D object (typed FeaturePython)
  ChamferSize = 0
  Closed = false
  End = (188.624,-40.5463,0)
  FilletRadius = 0
  Length = 12.5
  MakeFace = true
  Placement = pos=(201.124,-40.5463,0) rot=(0,0,1;0rad)
  Points = (2) [(0,0,0),(-12.5,0,0)]
  Start = (201.124,-40.5463,0)
  Subdivisions = 0
FEATURE [Part::Part2DObjectPython] Arc158  # Draft 2D object (typed FeaturePython)
  FirstAngle = 90
  LastAngle = 180
  MakeFace = true
  Placement = pos=(188.624,-41.2963,0) rot=(0,0,1;0rad)
  Radius = 0.75
FEATURE [Part::Part2DObjectPython] Arc159  # Draft 2D object (typed FeaturePython)
  FirstAngle = 90
  LastAngle = 180
  MakeFace = true
  Placement = pos=(188.624,-53.7963,0) rot=(0,0,1;1.5708rad)
  Radius = 0.75
FEATURE [App::DocumentObjectGroup] Group042
  Group = -> [Arc158,Arc157,Arc159,Arc156,Line314,Line319,Line317,Line316]
FEATURE [Part::Part2DObjectPython] Arc160  # Draft 2D object (typed FeaturePython)
  FirstAngle = 90
  LastAngle = 180
  MakeFace = true
  Placement = pos=(220.133,-53.7963,0) rot=(0,0,1;3.14159rad)
  Radius = 0.75
FEATURE [Part::Part2DObjectPython] Line322  # Draft 2D object (typed FeaturePython)
  ChamferSize = 0
  Closed = false
  End = (206.883,-53.7963,0)
  FilletRadius = 0
  Length = 12.5
  MakeFace = true
  Placement = pos=(206.883,-41.2963,0) rot=(0,0,1;0rad)
  Points = (2) [(0,0,0),(0,-12.5,0)]
  Start = (206.883,-41.2963,0)
  Subdivisions = 0
FEATURE [Part::Part2DObjectPython] Arc161  # Draft 2D object (typed FeaturePython)
  FirstAngle = 90
  LastAngle = 180
  MakeFace = true
  Placement = pos=(207.633,-41.2963,0) rot=(0,0,1;0rad)
  Radius = 0.75
FEATURE [Part::Part2DObjectPython] Line324  # Draft 2D object (typed FeaturePython)
  ChamferSize = 0
  Closed = false
  End = (220.883,-41.2963,0)
  FilletRadius = 0
  Length = 12.5
  MakeFace = true
  Placement = pos=(220.883,-53.7963,0) rot=(0,0,1;0rad)
  Points = (2) [(0,0,0),(0,12.5,0)]
  Start = (220.883,-53.7963,0)
  Subdivisions = 0
FEATURE [Part::Part2DObjectPython] Line326  # Draft 2D object (typed FeaturePython)
  ChamferSize = 0
  Closed = false
  End = (220.133,-54.5463,0)
  FilletRadius = 0
  Length = 12.5
  MakeFace = true
  Placement = pos=(207.633,-54.5463,0) rot=(0,0,1;0rad)
  Points = (2) [(0,0,0),(12.5,0,0)]
  Start = (207.633,-54.5463,0)
  Subdivisions = 0
FEATURE [Part::Part2DObjectPython] Line327  # Draft 2D object (typed FeaturePython)
  ChamferSize = 0
  Closed = false
  End = (207.633,-40.5463,0)
  FilletRadius = 0
  Length = 12.5
  MakeFace = true
  Placement = pos=(220.133,-40.5463,0) rot=(0,0,1;0rad)
  Points = (2) [(0,0,0),(-12.5,0,0)]
  Start = (220.133,-40.5463,0)
  Subdivisions = 0
FEATURE [Part::Part2DObjectPython] Arc162  # Draft 2D object (typed FeaturePython)
  FirstAngle = 90
  LastAngle = 180
  MakeFace = true
  Placement = pos=(207.633,-53.7963,0) rot=(0,0,1;1.5708rad)
  Radius = 0.75
FEATURE [Part::Part2DObjectPython] Arc163  # Draft 2D object (typed FeaturePython)
  FirstAngle = 90
  LastAngle = 180
  MakeFace = true
  Placement = pos=(220.133,-41.2963,0) rot=(0,0,-1;1.5708rad)
  Radius = 0.75
FEATURE [App::DocumentObjectGroup] Group043
  Group = -> [Arc161,Arc163,Arc162,Arc160,Line324,Line327,Line322,Line326]
FEATURE [Part::Part2DObjectPython] Arc164  # Draft 2D object (typed FeaturePython)
  FirstAngle = 90
  LastAngle = 180
  MakeFace = true
  Placement = pos=(239.142,-53.7963,0) rot=(0,0,1;3.14159rad)
  Radius = 0.75
FEATURE [Part::Part2DObjectPython] Line330  # Draft 2D object (typed FeaturePython)
  ChamferSize = 0
  Closed = false
  End = (225.892,-53.7963,0)
  FilletRadius = 0
  Length = 12.5
  MakeFace = true
  Placement = pos=(225.892,-41.2963,0) rot=(0,0,1;0rad)
  Points = (2) [(0,0,0),(0,-12.5,0)]
  Start = (225.892,-41.2963,0)
  Subdivisions = 0
FEATURE [Part::Part2DObjectPython] Line332  # Draft 2D object (typed FeaturePython)
  ChamferSize = 0
  Closed = false
  End = (239.142,-54.5463,0)
  FilletRadius = 0
  Length = 12.5
  MakeFace = true
  Placement = pos=(226.642,-54.5463,0) rot=(0,0,1;0rad)
  Points = (2) [(0,0,0),(12.5,0,0)]
  Start = (226.642,-54.5463,0)
  Subdivisions = 0
FEATURE [Part::Part2DObjectPython] Line333  # Draft 2D object (typed FeaturePython)
  ChamferSize = 0
  Closed = false
  End = (239.892,-41.2963,0)
  FilletRadius = 0
  Length = 12.5
  MakeFace = true
  Placement = pos=(239.892,-53.7963,0) rot=(0,0,1;0rad)
  Points = (2) [(0,0,0),(0,12.5,0)]
  Start = (239.892,-53.7963,0)
  Subdivisions = 0
FEATURE [Part::Part2DObjectPython] Line334  # Draft 2D object (typed FeaturePython)
  ChamferSize = 0
  Closed = false
  End = (226.642,-40.5463,0)
  FilletRadius = 0
  Length = 12.5
  MakeFace = true
  Placement = pos=(239.142,-40.5463,0) rot=(0,0,1;0rad)
  Points = (2) [(0,0,0),(-12.5,0,0)]
  Start = (239.142,-40.5463,0)
  Subdivisions = 0
FEATURE [Part::Part2DObjectPython] Arc165  # Draft 2D object (typed FeaturePython)
  FirstAngle = 90
  LastAngle = 180
  MakeFace = true
  Placement = pos=(226.642,-41.2963,0) rot=(0,0,1;0rad)
  Radius = 0.75
FEATURE [Part::Part2DObjectPython] Arc166  # Draft 2D object (typed FeaturePython)
  FirstAngle = 90
  LastAngle = 180
  MakeFace = true
  Placement = pos=(239.142,-41.2963,0) rot=(0,0,-1;1.5708rad)
  Radius = 0.75
FEATURE [Part::Part2DObjectPython] Arc167  # Draft 2D object (typed FeaturePython)
  FirstAngle = 90
  LastAngle = 180
  MakeFace = true
  Placement = pos=(226.642,-53.7963,0) rot=(0,0,1;1.5708rad)
  Radius = 0.75
FEATURE [App::DocumentObjectGroup] Group044
  Group = -> [Arc165,Arc166,Arc167,Arc164,Line333,Line334,Line330,Line332]
FEATURE [App::DocumentObjectGroup] Group032  label="Row 3"
  Group = -> [Group033,Group034,Group035,Group036,Group037,Group038,Group039,Group040,Group041,Group042,Group043,Group044]
FEATURE [Part::Part2DObjectPython] Line337  # Draft 2D object (typed FeaturePython)
  ChamferSize = 0
  Closed = false
  End = (270.034,-54.5463,0)
  FilletRadius = 0
  Length = 12.5
  MakeFace = true
  Placement = pos=(257.534,-54.5463,0) rot=(0,0,1;0rad)
  Points = (2) [(0,0,0),(12.5,0,0)]
  Start = (257.534,-54.5463,0)
  Subdivisions = 0
FEATURE [Part::Part2DObjectPython] Line338  # Draft 2D object (typed FeaturePython)
  ChamferSize = 0
  Closed = false
  End = (256.784,-53.7963,0)
  FilletRadius = 0
  Length = 12.5
  MakeFace = true
  Placement = pos=(256.784,-41.2963,0) rot=(0,0,1;0rad)
  Points = (2) [(0,0,0),(0,-12.5,0)]
  Start = (256.784,-41.2963,0)
  Subdivisions = 0
FEATURE [Part::Part2DObjectPython] Line339  # Draft 2D object (typed FeaturePython)
  ChamferSize = 0
  Closed = false
  End = (257.534,-40.5463,0)
  FilletRadius = 0
  Length = 12.5
  MakeFace = true
  Placement = pos=(270.034,-40.5463,0) rot=(0,0,1;0rad)
  Points = (2) [(0,0,0),(-12.5,0,0)]
  Start = (270.034,-40.5463,0)
  Subdivisions = 0
FEATURE [Part::Part2DObjectPython] Line340  # Draft 2D object (typed FeaturePython)
  ChamferSize = 0
  Closed = false
  End = (270.784,-41.2963,0)
  FilletRadius = 0
  Length = 12.5
  MakeFace = true
  Placement = pos=(270.784,-53.7963,0) rot=(0,0,1;0rad)
  Points = (2) [(0,0,0),(0,12.5,0)]
  Start = (270.784,-53.7963,0)
  Subdivisions = 0
FEATURE [Part::Part2DObjectPython] Arc168  # Draft 2D object (typed FeaturePython)
  FirstAngle = 90
  LastAngle = 180
  MakeFace = true
  Placement = pos=(270.034,-41.2963,0) rot=(0,0,-1;1.5708rad)
  Radius = 0.75
FEATURE [Part::Part2DObjectPython] Arc169  # Draft 2D object (typed FeaturePython)
  FirstAngle = 90
  LastAngle = 180
  MakeFace = true
  Placement = pos=(270.034,-53.7963,0) rot=(0,0,1;3.14159rad)
  Radius = 0.75
FEATURE [Part::Part2DObjectPython] Arc170  # Draft 2D object (typed FeaturePython)
  FirstAngle = 90
  LastAngle = 180
  MakeFace = true
  Placement = pos=(257.534,-53.7963,0) rot=(0,0,1;1.5708rad)
  Radius = 0.75
FEATURE [Part::Part2DObjectPython] Arc171  # Draft 2D object (typed FeaturePython)
  FirstAngle = 90
  LastAngle = 180
  MakeFace = true
  Placement = pos=(257.534,-41.2963,0) rot=(0,0,1;0rad)
  Radius = 0.75
FEATURE [Part::Part2DObjectPython] Arc172  # Draft 2D object (typed FeaturePython)
  FirstAngle = 90
  LastAngle = 180
  MakeFace = true
  Placement = pos=(258.154,-41.2963,0) rot=(0,0,-1;1.5708rad)
  Radius = 0.75
FEATURE [Part::Part2DObjectPython] Line345  # Draft 2D object (typed FeaturePython)
  ChamferSize = 0
  Closed = false
  End = (258.904,-41.2963,0)
  FilletRadius = 0
  Length = 12.5
  MakeFace = true
  Placement = pos=(258.904,-53.7963,0) rot=(0,0,1;0rad)
  Points = (2) [(0,0,0),(0,12.5,0)]
  Start = (258.904,-53.7963,0)
  Subdivisions = 0
FEATURE [Part::Part2DObjectPython] Line346  # Draft 2D object (typed FeaturePython)
  ChamferSize = 0
  Closed = false
  End = (244.904,-53.7963,0)
  FilletRadius = 0
  Length = 12.5
  MakeFace = true
  Placement = pos=(244.904,-41.2963,0) rot=(0,0,1;0rad)
  Points = (2) [(0,0,0),(0,-12.5,0)]
  Start = (244.904,-41.2963,0)
  Subdivisions = 0
FEATURE [Part::Part2DObjectPython] Line347  # Draft 2D object (typed FeaturePython)
  ChamferSize = 0
  Closed = false
  End = (245.654,-40.5463,0)
  FilletRadius = 0
  Length = 12.5
  MakeFace = true
  Placement = pos=(258.154,-40.5463,0) rot=(0,0,1;0rad)
  Points = (2) [(0,0,0),(-12.5,0,0)]
  Start = (258.154,-40.5463,0)
  Subdivisions = 0
FEATURE [Part::Part2DObjectPython] Arc173  # Draft 2D object (typed FeaturePython)
  FirstAngle = 90
  LastAngle = 180
  MakeFace = true
  Placement = pos=(258.154,-53.7963,0) rot=(0,0,1;3.14159rad)
  Radius = 0.75
FEATURE [Part::Part2DObjectPython] Line348  # Draft 2D object (typed FeaturePython)
  ChamferSize = 0
  Closed = false
  End = (258.154,-54.5463,0)
  FilletRadius = 0
  Length = 12.5
  MakeFace = true
  Placement = pos=(245.654,-54.5463,0) rot=(0,0,1;0rad)
  Points = (2) [(0,0,0),(12.5,0,0)]
  Start = (245.654,-54.5463,0)
  Subdivisions = 0
FEATURE [Part::Part2DObjectPython] Arc174  # Draft 2D object (typed FeaturePython)
  FirstAngle = 90
  LastAngle = 180
  MakeFace = true
  Placement = pos=(245.654,-41.2963,0) rot=(0,0,1;0rad)
  Radius = 0.75
FEATURE [Part::Part2DObjectPython] Arc175  # Draft 2D object (typed FeaturePython)
  FirstAngle = 90
  LastAngle = 180
  MakeFace = true
  Placement = pos=(245.654,-53.7963,0) rot=(0,0,1;1.5708rad)
  Radius = 0.75
FEATURE [App::DocumentObjectGroup] Group046
  Group = -> [Arc174,Arc172,Arc175,Arc173,Line345,Line347,Line346,Line348]
FEATURE [Part::Part2DObjectPython] Arc176  # Draft 2D object (typed FeaturePython)
  FirstAngle = 90
  LastAngle = 180
  MakeFace = true
  Placement = pos=(279.538,-31.7916,0) rot=(0,0,-1;1.5708rad)
  Radius = 0.75
FEATURE [Part::Part2DObjectPython] Line355  # Draft 2D object (typed FeaturePython)
  ChamferSize = 0
  Closed = false
  End = (267.038,-31.0416,0)
  FilletRadius = 0
  Length = 12.5
  MakeFace = true
  Placement = pos=(279.538,-31.0416,0) rot=(0,0,1;0rad)
  Points = (2) [(0,0,0),(-12.5,0,0)]
  Start = (279.538,-31.0416,0)
  Subdivisions = 0
FEATURE [Part::Part2DObjectPython] Line356  # Draft 2D object (typed FeaturePython)
  ChamferSize = 0
  Closed = false
  End = (279.538,-45.0416,0)
  FilletRadius = 0
  Length = 12.5
  MakeFace = true
  Placement = pos=(267.038,-45.0416,0) rot=(0,0,1;0rad)
  Points = (2) [(0,0,0),(12.5,0,0)]
  Start = (267.038,-45.0416,0)
  Subdivisions = 0
FEATURE [Part::Part2DObjectPython] Line359  # Draft 2D object (typed FeaturePython)
  ChamferSize = 0
  Closed = false
  End = (266.288,-44.2916,0)
  FilletRadius = 0
  Length = 12.5
  MakeFace = true
  Placement = pos=(266.288,-31.7916,0) rot=(0,0,1;0rad)
  Points = (2) [(0,0,0),(0,-12.5,0)]
  Start = (266.288,-31.7916,0)
  Subdivisions = 0
FEATURE [Part::Part2DObjectPython] Arc177  # Draft 2D object (typed FeaturePython)
  FirstAngle = 90
  LastAngle = 180
  MakeFace = true
  Placement = pos=(267.038,-31.7916,0) rot=(0,0,1;0rad)
  Radius = 0.75
FEATURE [Part::Part2DObjectPython] Arc178  # Draft 2D object (typed FeaturePython)
  FirstAngle = 90
  LastAngle = 180
  MakeFace = true
  Placement = pos=(279.538,-44.2916,0) rot=(0,0,1;3.14159rad)
  Radius = 0.75
FEATURE [Part::Part2DObjectPython] Arc179  # Draft 2D object (typed FeaturePython)
  FirstAngle = 90
  LastAngle = 180
  MakeFace = true
  Placement = pos=(267.038,-44.2916,0) rot=(0,0,1;1.5708rad)
  Radius = 0.75
FEATURE [Part::Part2DObjectPython] Line360  # Draft 2D object (typed FeaturePython)
  ChamferSize = 0
  Closed = false
  End = (280.288,-31.7916,0)
  FilletRadius = 0
  Length = 12.5
  MakeFace = true
  Placement = pos=(280.288,-44.2916,0) rot=(0,0,1;0rad)
  Points = (2) [(0,0,0),(0,12.5,0)]
  Start = (280.288,-44.2916,0)
  Subdivisions = 0
FEATURE [Part::Part2DObjectPython] Line361  # Draft 2D object (typed FeaturePython)
  ChamferSize = 0
  Closed = false
  End = (28.4071,-60.3056,0)
  FilletRadius = 0
  Length = 12.5
  MakeFace = true
  Placement = pos=(28.4071,-72.8056,0) rot=(0,0,1;0rad)
  Points = (2) [(0,0,0),(0,12.5,0)]
  Start = (28.4071,-72.8056,0)
  Subdivisions = 0
FEATURE [Part::Part2DObjectPython] Arc180  # Draft 2D object (typed FeaturePython)
  FirstAngle = 90
  LastAngle = 180
  MakeFace = true
  Placement = pos=(15.1571,-60.3056,0) rot=(0,0,1;0rad)
  Radius = 0.75
FEATURE [Part::Part2DObjectPython] Line363  # Draft 2D object (typed FeaturePython)
  ChamferSize = 0
  Closed = false
  End = (15.1571,-59.5556,0)
  FilletRadius = 0
  Length = 12.5
  MakeFace = true
  Placement = pos=(27.6571,-59.5556,0) rot=(0,0,1;0rad)
  Points = (2) [(0,0,0),(-12.5,0,0)]
  Start = (27.6571,-59.5556,0)
  Subdivisions = 0
FEATURE [Part::Part2DObjectPython] Line365  # Draft 2D object (typed FeaturePython)
  ChamferSize = 0
  Closed = false
  End = (14.4071,-72.8056,0)
  FilletRadius = 0
  Length = 12.5
  MakeFace = true
  Placement = pos=(14.4071,-60.3056,0) rot=(0,0,1;0rad)
  Points = (2) [(0,0,0),(0,-12.5,0)]
  Start = (14.4071,-60.3056,0)
  Subdivisions = 0
FEATURE [Part::Part2DObjectPython] Arc181  # Draft 2D object (typed FeaturePython)
  FirstAngle = 90
  LastAngle = 180
  MakeFace = true
  Placement = pos=(27.6571,-60.3056,0) rot=(0,0,-1;1.5708rad)
  Radius = 0.75
FEATURE [Part::Part2DObjectPython] Arc182  # Draft 2D object (typed FeaturePython)
  FirstAngle = 90
  LastAngle = 180
  MakeFace = true
  Placement = pos=(27.6571,-72.8056,0) rot=(0,0,1;3.14159rad)
  Radius = 0.75
FEATURE [Part::Part2DObjectPython] Arc183  # Draft 2D object (typed FeaturePython)
  FirstAngle = 90
  LastAngle = 180
  MakeFace = true
  Placement = pos=(15.1571,-72.8056,0) rot=(0,0,1;1.5708rad)
  Radius = 0.75
FEATURE [Part::Part2DObjectPython] Line367  # Draft 2D object (typed FeaturePython)
  ChamferSize = 0
  Closed = false
  End = (27.6571,-73.5556,0)
  FilletRadius = 0
  Length = 12.5
  MakeFace = true
  Placement = pos=(15.1571,-73.5556,0) rot=(0,0,1;0rad)
  Points = (2) [(0,0,0),(12.5,0,0)]
  Start = (15.1571,-73.5556,0)
  Subdivisions = 0
FEATURE [Part::Part2DObjectPython] Arc184  # Draft 2D object (typed FeaturePython)
  FirstAngle = 90
  LastAngle = 180
  MakeFace = true
  Placement = pos=(5.65244,-60.3056,0) rot=(0,0,1;0rad)
  Radius = 0.75
FEATURE [Part::Part2DObjectPython] Line370  # Draft 2D object (typed FeaturePython)
  ChamferSize = 0
  Closed = false
  End = (18.9024,-60.3056,0)
  FilletRadius = 0
  Length = 12.5
  MakeFace = true
  Placement = pos=(18.9024,-72.8056,0) rot=(0,0,1;0rad)
  Points = (2) [(0,0,0),(0,12.5,0)]
  Start = (18.9024,-72.8056,0)
  Subdivisions = 0
FEATURE [Part::Part2DObjectPython] Arc185  # Draft 2D object (typed FeaturePython)
  FirstAngle = 90
  LastAngle = 180
  MakeFace = true
  Placement = pos=(18.1524,-60.3056,0) rot=(0,0,-1;1.5708rad)
  Radius = 0.75
FEATURE [Part::Part2DObjectPython] Line373  # Draft 2D object (typed FeaturePython)
  ChamferSize = 0
  Closed = false
  End = (4.90244,-72.8056,0)
  FilletRadius = 0
  Length = 12.5
  MakeFace = true
  Placement = pos=(4.90244,-60.3056,0) rot=(0,0,1;0rad)
  Points = (2) [(0,0,0),(0,-12.5,0)]
  Start = (4.90244,-60.3056,0)
  Subdivisions = 0
FEATURE [Part::Part2DObjectPython] Arc186  # Draft 2D object (typed FeaturePython)
  FirstAngle = 90
  LastAngle = 180
  MakeFace = true
  Placement = pos=(5.65244,-72.8056,0) rot=(0,0,1;1.5708rad)
  Radius = 0.75
FEATURE [Part::Part2DObjectPython] Line374  # Draft 2D object (typed FeaturePython)
  ChamferSize = 0
  Closed = false
  End = (18.1524,-73.5556,0)
  FilletRadius = 0
  Length = 12.5
  MakeFace = true
  Placement = pos=(5.65244,-73.5556,0) rot=(0,0,1;0rad)
  Points = (2) [(0,0,0),(12.5,0,0)]
  Start = (5.65244,-73.5556,0)
  Subdivisions = 0
FEATURE [Part::Part2DObjectPython] Arc187  # Draft 2D object (typed FeaturePython)
  FirstAngle = 90
  LastAngle = 180
  MakeFace = true
  Placement = pos=(18.1524,-72.8056,0) rot=(0,0,1;3.14159rad)
  Radius = 0.75
FEATURE [Part::Part2DObjectPython] Line376  # Draft 2D object (typed FeaturePython)
  ChamferSize = 0
  Closed = false
  End = (5.65244,-59.5556,0)
  FilletRadius = 0
  Length = 12.5
  MakeFace = true
  Placement = pos=(18.1524,-59.5556,0) rot=(0,0,1;0rad)
  Points = (2) [(0,0,0),(-12.5,0,0)]
  Start = (18.1524,-59.5556,0)
  Subdivisions = 0
FEATURE [App::DocumentObjectGroup] Group050
  Group = -> [Arc184,Arc185,Arc186,Arc187,Line370,Line376,Line373,Line374]
FEATURE [Part::Part2DObjectPython] Arc188  # Draft 2D object (typed FeaturePython)
  FirstAngle = 90
  LastAngle = 180
  MakeFace = true
  Placement = pos=(39.5392,-72.8056,0) rot=(0,0,1;3.14159rad)
  Radius = 0.75
FEATURE [Part::Part2DObjectPython] Line378  # Draft 2D object (typed FeaturePython)
  ChamferSize = 0
  Closed = false
  End = (26.2892,-72.8056,0)
  FilletRadius = 0
  Length = 12.5
  MakeFace = true
  Placement = pos=(26.2892,-60.3056,0) rot=(0,0,1;0rad)
  Points = (2) [(0,0,0),(0,-12.5,0)]
  Start = (26.2892,-60.3056,0)
  Subdivisions = 0
FEATURE [Part::Part2DObjectPython] Arc189  # Draft 2D object (typed FeaturePython)
  FirstAngle = 90
  LastAngle = 180
  MakeFace = true
  Placement = pos=(27.0392,-60.3056,0) rot=(0,0,1;0rad)
  Radius = 0.75
FEATURE [Part::Part2DObjectPython] Line380  # Draft 2D object (typed FeaturePython)
  ChamferSize = 0
  Closed = false
  End = (40.2892,-60.3056,0)
  FilletRadius = 0
  Length = 12.5
  MakeFace = true
  Placement = pos=(40.2892,-72.8056,0) rot=(0,0,1;0rad)
  Points = (2) [(0,0,0),(0,12.5,0)]
  Start = (40.2892,-72.8056,0)
  Subdivisions = 0
FEATURE [Part::Part2DObjectPython] Arc190  # Draft 2D object (typed FeaturePython)
  FirstAngle = 90
  LastAngle = 180
  MakeFace = true
  Placement = pos=(39.5392,-60.3056,0) rot=(0,0,-1;1.5708rad)
  Radius = 0.75
FEATURE [Part::Part2DObjectPython] Arc191  # Draft 2D object (typed FeaturePython)
  FirstAngle = 90
  LastAngle = 180
  MakeFace = true
  Placement = pos=(27.0392,-72.8056,0) rot=(0,0,1;1.5708rad)
  Radius = 0.75
FEATURE [Part::Part2DObjectPython] Line382  # Draft 2D object (typed FeaturePython)
  ChamferSize = 0
  Closed = false
  End = (27.0392,-59.5556,0)
  FilletRadius = 0
  Length = 12.5
  MakeFace = true
  Placement = pos=(39.5392,-59.5556,0) rot=(0,0,1;0rad)
  Points = (2) [(0,0,0),(-12.5,0,0)]
  Start = (39.5392,-59.5556,0)
  Subdivisions = 0
FEATURE [Part::Part2DObjectPython] Line383  # Draft 2D object (typed FeaturePython)
  ChamferSize = 0
  Closed = false
  End = (39.5392,-73.5556,0)
  FilletRadius = 0
  Length = 12.5
  MakeFace = true
  Placement = pos=(27.0392,-73.5556,0) rot=(0,0,1;0rad)
  Points = (2) [(0,0,0),(12.5,0,0)]
  Start = (27.0392,-73.5556,0)
  Subdivisions = 0
FEATURE [App::DocumentObjectGroup] Group051
  Group = -> [Arc189,Arc190,Arc191,Arc188,Line380,Line382,Line378,Line383]
FEATURE [Part::Part2DObjectPython] Arc192  # Draft 2D object (typed FeaturePython)
  FirstAngle = 90
  LastAngle = 180
  MakeFace = true
  Placement = pos=(46.0485,-60.3056,0) rot=(0,0,1;0rad)
  Radius = 0.75
FEATURE [Part::Part2DObjectPython] Line386  # Draft 2D object (typed FeaturePython)
  ChamferSize = 0
  Closed = false
  End = (59.2985,-60.3056,0)
  FilletRadius = 0
  Length = 12.5
  MakeFace = true
  Placement = pos=(59.2985,-72.8056,0) rot=(0,0,1;0rad)
  Points = (2) [(0,0,0),(0,12.5,0)]
  Start = (59.2985,-72.8056,0)
  Subdivisions = 0
FEATURE [Part::Part2DObjectPython] Arc193  # Draft 2D object (typed FeaturePython)
  FirstAngle = 90
  LastAngle = 180
  MakeFace = true
  Placement = pos=(58.5485,-60.3056,0) rot=(0,0,-1;1.5708rad)
  Radius = 0.75
FEATURE [Part::Part2DObjectPython] Line389  # Draft 2D object (typed FeaturePython)
  ChamferSize = 0
  Closed = false
  End = (45.2985,-72.8056,0)
  FilletRadius = 0
  Length = 12.5
  MakeFace = true
  Placement = pos=(45.2985,-60.3056,0) rot=(0,0,1;0rad)
  Points = (2) [(0,0,0),(0,-12.5,0)]
  Start = (45.2985,-60.3056,0)
  Subdivisions = 0
FEATURE [Part::Part2DObjectPython] Arc194  # Draft 2D object (typed FeaturePython)
  FirstAngle = 90
  LastAngle = 180
  MakeFace = true
  Placement = pos=(46.0485,-72.8056,0) rot=(0,0,1;1.5708rad)
  Radius = 0.75
FEATURE [Part::Part2DObjectPython] Line390  # Draft 2D object (typed FeaturePython)
  ChamferSize = 0
  Closed = false
  End = (58.5485,-73.5556,0)
  FilletRadius = 0
  Length = 12.5
  MakeFace = true
  Placement = pos=(46.0485,-73.5556,0) rot=(0,0,1;0rad)
  Points = (2) [(0,0,0),(12.5,0,0)]
  Start = (46.0485,-73.5556,0)
  Subdivisions = 0
FEATURE [Part::Part2DObjectPython] Arc195  # Draft 2D object (typed FeaturePython)
  FirstAngle = 90
  LastAngle = 180
  MakeFace = true
  Placement = pos=(58.5485,-72.8056,0) rot=(0,0,1;3.14159rad)
  Radius = 0.75
FEATURE [Part::Part2DObjectPython] Line392  # Draft 2D object (typed FeaturePython)
  ChamferSize = 0
  Closed = false
  End = (46.0485,-59.5556,0)
  FilletRadius = 0
  Length = 12.5
  MakeFace = true
  Placement = pos=(58.5485,-59.5556,0) rot=(0,0,1;0rad)
  Points = (2) [(0,0,0),(-12.5,0,0)]
  Start = (58.5485,-59.5556,0)
  Subdivisions = 0
FEATURE [App::DocumentObjectGroup] Group052
  Group = -> [Arc192,Arc193,Arc194,Arc195,Line386,Line392,Line389,Line390]
FEATURE [Part::Part2DObjectPython] Line393  # Draft 2D object (typed FeaturePython)
  ChamferSize = 0
  Closed = false
  End = (78.3079,-60.3056,0)
  FilletRadius = 0
  Length = 12.5
  MakeFace = true
  Placement = pos=(78.3079,-72.8056,0) rot=(0,0,1;0rad)
  Points = (2) [(0,0,0),(0,12.5,0)]
  Start = (78.3079,-72.8056,0)
  Subdivisions = 0
FEATURE [Part::Part2DObjectPython] Arc196  # Draft 2D object (typed FeaturePython)
  FirstAngle = 90
  LastAngle = 180
  MakeFace = true
  Placement = pos=(65.0579,-60.3056,0) rot=(0,0,1;0rad)
  Radius = 0.75
FEATURE [Part::Part2DObjectPython] Arc197  # Draft 2D object (typed FeaturePython)
  FirstAngle = 90
  LastAngle = 180
  MakeFace = true
  Placement = pos=(65.0579,-72.8056,0) rot=(0,0,1;1.5708rad)
  Radius = 0.75
FEATURE [Part::Part2DObjectPython] Arc198  # Draft 2D object (typed FeaturePython)
  FirstAngle = 90
  LastAngle = 180
  MakeFace = true
  Placement = pos=(77.5579,-60.3056,0) rot=(0,0,-1;1.5708rad)
  Radius = 0.75
FEATURE [Part::Part2DObjectPython] Line397  # Draft 2D object (typed FeaturePython)
  ChamferSize = 0
  Closed = false
  End = (64.3079,-72.8056,0)
  FilletRadius = 0
  Length = 12.5
  MakeFace = true
  Placement = pos=(64.3079,-60.3056,0) rot=(0,0,1;0rad)
  Points = (2) [(0,0,0),(0,-12.5,0)]
  Start = (64.3079,-60.3056,0)
  Subdivisions = 0
FEATURE [Part::Part2DObjectPython] Line398  # Draft 2D object (typed FeaturePython)
  ChamferSize = 0
  Closed = false
  End = (65.0579,-59.5556,0)
  FilletRadius = 0
  Length = 12.5
  MakeFace = true
  Placement = pos=(77.5579,-59.5556,0) rot=(0,0,1;0rad)
  Points = (2) [(0,0,0),(-12.5,0,0)]
  Start = (77.5579,-59.5556,0)
  Subdivisions = 0
FEATURE [Part::Part2DObjectPython] Arc199  # Draft 2D object (typed FeaturePython)
  FirstAngle = 90
  LastAngle = 180
  MakeFace = true
  Placement = pos=(77.5579,-72.8056,0) rot=(0,0,1;3.14159rad)
  Radius = 0.75
FEATURE [Part::Part2DObjectPython] Line399  # Draft 2D object (typed FeaturePython)
  ChamferSize = 0
  Closed = false
  End = (77.5579,-73.5556,0)
  FilletRadius = 0
  Length = 12.5
  MakeFace = true
  Placement = pos=(65.0579,-73.5556,0) rot=(0,0,1;0rad)
  Points = (2) [(0,0,0),(12.5,0,0)]
  Start = (65.0579,-73.5556,0)
  Subdivisions = 0
FEATURE [App::DocumentObjectGroup] Group053
  Group = -> [Arc196,Arc198,Arc197,Arc199,Line393,Line398,Line397,Line399]
FEATURE [Part::Part2DObjectPython] Line402  # Draft 2D object (typed FeaturePython)
  ChamferSize = 0
  Closed = false
  End = (97.3198,-60.3056,0)
  FilletRadius = 0
  Length = 12.5
  MakeFace = true
  Placement = pos=(97.3198,-72.8056,0) rot=(0,0,1;0rad)
  Points = (2) [(0,0,0),(0,12.5,0)]
  Start = (97.3198,-72.8056,0)
  Subdivisions = 0
FEATURE [Part::Part2DObjectPython] Arc200  # Draft 2D object (typed FeaturePython)
  FirstAngle = 90
  LastAngle = 180
  MakeFace = true
  Placement = pos=(96.5698,-60.3056,0) rot=(0,0,-1;1.5708rad)
  Radius = 0.75
FEATURE [Part::Part2DObjectPython] Line405  # Draft 2D object (typed FeaturePython)
  ChamferSize = 0
  Closed = false
  End = (83.3198,-72.8056,0)
  FilletRadius = 0
  Length = 12.5
  MakeFace = true
  Placement = pos=(83.3198,-60.3056,0) rot=(0,0,1;0rad)
  Points = (2) [(0,0,0),(0,-12.5,0)]
  Start = (83.3198,-60.3056,0)
  Subdivisions = 0
FEATURE [Part::Part2DObjectPython] Line406  # Draft 2D object (typed FeaturePython)
  ChamferSize = 0
  Closed = false
  End = (84.0698,-59.5556,0)
  FilletRadius = 0
  Length = 12.5
  MakeFace = true
  Placement = pos=(96.5698,-59.5556,0) rot=(0,0,1;0rad)
  Points = (2) [(0,0,0),(-12.5,0,0)]
  Start = (96.5698,-59.5556,0)
  Subdivisions = 0
FEATURE [Part::Part2DObjectPython] Arc201  # Draft 2D object (typed FeaturePython)
  FirstAngle = 90
  LastAngle = 180
  MakeFace = true
  Placement = pos=(96.5698,-72.8056,0) rot=(0,0,1;3.14159rad)
  Radius = 0.75
FEATURE [Part::Part2DObjectPython] Arc202  # Draft 2D object (typed FeaturePython)
  FirstAngle = 90
  LastAngle = 180
  MakeFace = true
  Placement = pos=(84.0698,-72.8056,0) rot=(0,0,1;1.5708rad)
  Radius = 0.75
FEATURE [Part::Part2DObjectPython] Arc203  # Draft 2D object (typed FeaturePython)
  FirstAngle = 90
  LastAngle = 180
  MakeFace = true
  Placement = pos=(84.0698,-60.3056,0) rot=(0,0,1;0rad)
  Radius = 0.75
FEATURE [Part::Part2DObjectPython] Line408  # Draft 2D object (typed FeaturePython)
  ChamferSize = 0
  Closed = false
  End = (96.5698,-73.5556,0)
  FilletRadius = 0
  Length = 12.5
  MakeFace = true
  Placement = pos=(84.0698,-73.5556,0) rot=(0,0,1;0rad)
  Points = (2) [(0,0,0),(12.5,0,0)]
  Start = (84.0698,-73.5556,0)
  Subdivisions = 0
FEATURE [App::DocumentObjectGroup] Group054
  Group = -> [Arc203,Arc200,Arc202,Arc201,Line402,Line406,Line405,Line408]
FEATURE [Part::Part2DObjectPython] Arc204  # Draft 2D object (typed FeaturePython)
  FirstAngle = 90
  LastAngle = 180
  MakeFace = true
  Placement = pos=(115.579,-60.3056,0) rot=(0,0,-1;1.5708rad)
  Radius = 0.75
FEATURE [Part::Part2DObjectPython] Line411  # Draft 2D object (typed FeaturePython)
  ChamferSize = 0
  Closed = false
  End = (102.329,-72.8056,0)
  FilletRadius = 0
  Length = 12.5
  MakeFace = true
  Placement = pos=(102.329,-60.3056,0) rot=(0,0,1;0rad)
  Points = (2) [(0,0,0),(0,-12.5,0)]
  Start = (102.329,-60.3056,0)
  Subdivisions = 0
FEATURE [Part::Part2DObjectPython] Line412  # Draft 2D object (typed FeaturePython)
  ChamferSize = 0
  Closed = false
  End = (116.329,-60.3056,0)
  FilletRadius = 0
  Length = 12.5
  MakeFace = true
  Placement = pos=(116.329,-72.8056,0) rot=(0,0,1;0rad)
  Points = (2) [(0,0,0),(0,12.5,0)]
  Start = (116.329,-72.8056,0)
  Subdivisions = 0
FEATURE [Part::Part2DObjectPython] Line414  # Draft 2D object (typed FeaturePython)
  ChamferSize = 0
  Closed = false
  End = (103.079,-59.5556,0)
  FilletRadius = 0
  Length = 12.5
  MakeFace = true
  Placement = pos=(115.579,-59.5556,0) rot=(0,0,1;0rad)
  Points = (2) [(0,0,0),(-12.5,0,0)]
  Start = (115.579,-59.5556,0)
  Subdivisions = 0
FEATURE [Part::Part2DObjectPython] Arc205  # Draft 2D object (typed FeaturePython)
  FirstAngle = 90
  LastAngle = 180
  MakeFace = true
  Placement = pos=(103.079,-60.3056,0) rot=(0,0,1;0rad)
  Radius = 0.75
FEATURE [Part::Part2DObjectPython] Arc206  # Draft 2D object (typed FeaturePython)
  FirstAngle = 90
  LastAngle = 180
  MakeFace = true
  Placement = pos=(115.579,-72.8056,0) rot=(0,0,1;3.14159rad)
  Radius = 0.75
FEATURE [Part::Part2DObjectPython] Arc207  # Draft 2D object (typed FeaturePython)
  FirstAngle = 90
  LastAngle = 180
  MakeFace = true
  Placement = pos=(103.079,-72.8056,0) rot=(0,0,1;1.5708rad)
  Radius = 0.75
FEATURE [Part::Part2DObjectPython] Line415  # Draft 2D object (typed FeaturePython)
  ChamferSize = 0
  Closed = false
  End = (115.579,-73.5556,0)
  FilletRadius = 0
  Length = 12.5
  MakeFace = true
  Placement = pos=(103.079,-73.5556,0) rot=(0,0,1;0rad)
  Points = (2) [(0,0,0),(12.5,0,0)]
  Start = (103.079,-73.5556,0)
  Subdivisions = 0
FEATURE [App::DocumentObjectGroup] Group055
  Group = -> [Arc205,Arc204,Arc207,Arc206,Line412,Line414,Line411,Line415]
FEATURE [Part::Part2DObjectPython] Line420  # Draft 2D object (typed FeaturePython)
  ChamferSize = 0
  Closed = false
  End = (135.338,-60.3056,0)
  FilletRadius = 0
  Length = 12.5
  MakeFace = true
  Placement = pos=(135.338,-72.8056,0) rot=(0,0,1;0rad)
  Points = (2) [(0,0,0),(0,12.5,0)]
  Start = (135.338,-72.8056,0)
  Subdivisions = 0
FEATURE [Part::Part2DObjectPython] Arc208  # Draft 2D object (typed FeaturePython)
  FirstAngle = 90
  LastAngle = 180
  MakeFace = true
  Placement = pos=(122.088,-72.8056,0) rot=(0,0,1;1.5708rad)
  Radius = 0.75
FEATURE [Part::Part2DObjectPython] Arc209  # Draft 2D object (typed FeaturePython)
  FirstAngle = 90
  LastAngle = 180
  MakeFace = true
  Placement = pos=(134.588,-72.8056,0) rot=(0,0,1;3.14159rad)
  Radius = 0.75
FEATURE [Part::Part2DObjectPython] Line422  # Draft 2D object (typed FeaturePython)
  ChamferSize = 0
  Closed = false
  End = (134.588,-73.5556,0)
  FilletRadius = 0
  Length = 12.5
  MakeFace = true
  Placement = pos=(122.088,-73.5556,0) rot=(0,0,1;0rad)
  Points = (2) [(0,0,0),(12.5,0,0)]
  Start = (122.088,-73.5556,0)
  Subdivisions = 0
FEATURE [Part::Part2DObjectPython] Line423  # Draft 2D object (typed FeaturePython)
  ChamferSize = 0
  Closed = false
  End = (122.088,-59.5556,0)
  FilletRadius = 0
  Length = 12.5
  MakeFace = true
  Placement = pos=(134.588,-59.5556,0) rot=(0,0,1;0rad)
  Points = (2) [(0,0,0),(-12.5,0,0)]
  Start = (134.588,-59.5556,0)
  Subdivisions = 0
FEATURE [Part::Part2DObjectPython] Line424  # Draft 2D object (typed FeaturePython)
  ChamferSize = 0
  Closed = false
  End = (121.338,-72.8056,0)
  FilletRadius = 0
  Length = 12.5
  MakeFace = true
  Placement = pos=(121.338,-60.3056,0) rot=(0,0,1;0rad)
  Points = (2) [(0,0,0),(0,-12.5,0)]
  Start = (121.338,-60.3056,0)
  Subdivisions = 0
FEATURE [Part::Part2DObjectPython] Arc210  # Draft 2D object (typed FeaturePython)
  FirstAngle = 90
  LastAngle = 180
  MakeFace = true
  Placement = pos=(134.588,-60.3056,0) rot=(0,0,-1;1.5708rad)
  Radius = 0.75
FEATURE [Part::Part2DObjectPython] Arc211  # Draft 2D object (typed FeaturePython)
  FirstAngle = 90
  LastAngle = 180
  MakeFace = true
  Placement = pos=(122.088,-60.3056,0) rot=(0,0,1;0rad)
  Radius = 0.75
FEATURE [App::DocumentObjectGroup] Group056
  Group = -> [Arc211,Arc210,Arc208,Arc209,Line420,Line423,Line424,Line422]
FEATURE [Part::Part2DObjectPython] Line425  # Draft 2D object (typed FeaturePython)
  ChamferSize = 0
  Closed = false
  End = (141.098,-59.5556,0)
  FilletRadius = 0
  Length = 12.5
  MakeFace = true
  Placement = pos=(153.598,-59.5556,0) rot=(0,0,1;0rad)
  Points = (2) [(0,0,0),(-12.5,0,0)]
  Start = (153.598,-59.5556,0)
  Subdivisions = 0
FEATURE [Part::Part2DObjectPython] Line426  # Draft 2D object (typed FeaturePython)
  ChamferSize = 0
  Closed = false
  End = (154.348,-60.3056,0)
  FilletRadius = 0
  Length = 12.5
  MakeFace = true
  Placement = pos=(154.348,-72.8056,0) rot=(0,0,1;0rad)
  Points = (2) [(0,0,0),(0,12.5,0)]
  Start = (154.348,-72.8056,0)
  Subdivisions = 0
FEATURE [Part::Part2DObjectPython] Arc212  # Draft 2D object (typed FeaturePython)
  FirstAngle = 90
  LastAngle = 180
  MakeFace = true
  Placement = pos=(141.098,-72.8056,0) rot=(0,0,1;1.5708rad)
  Radius = 0.75
FEATURE [Part::Part2DObjectPython] Arc213  # Draft 2D object (typed FeaturePython)
  FirstAngle = 90
  LastAngle = 180
  MakeFace = true
  Placement = pos=(153.598,-72.8056,0) rot=(0,0,1;3.14159rad)
  Radius = 0.75
FEATURE [Part::Part2DObjectPython] Line431  # Draft 2D object (typed FeaturePython)
  ChamferSize = 0
  Closed = false
  End = (153.598,-73.5556,0)
  FilletRadius = 0
  Length = 12.5
  MakeFace = true
  Placement = pos=(141.098,-73.5556,0) rot=(0,0,1;0rad)
  Points = (2) [(0,0,0),(12.5,0,0)]
  Start = (141.098,-73.5556,0)
  Subdivisions = 0
FEATURE [Part::Part2DObjectPython] Line432  # Draft 2D object (typed FeaturePython)
  ChamferSize = 0
  Closed = false
  End = (140.348,-72.8056,0)
  FilletRadius = 0
  Length = 12.5
  MakeFace = true
  Placement = pos=(140.348,-60.3056,0) rot=(0,0,1;0rad)
  Points = (2) [(0,0,0),(0,-12.5,0)]
  Start = (140.348,-60.3056,0)
  Subdivisions = 0
FEATURE [Part::Part2DObjectPython] Arc214  # Draft 2D object (typed FeaturePython)
  FirstAngle = 90
  LastAngle = 180
  MakeFace = true
  Placement = pos=(153.598,-60.3056,0) rot=(0,0,-1;1.5708rad)
  Radius = 0.75
FEATURE [Part::Part2DObjectPython] Arc215  # Draft 2D object (typed FeaturePython)
  FirstAngle = 90
  LastAngle = 180
  MakeFace = true
  Placement = pos=(141.098,-60.3056,0) rot=(0,0,1;0rad)
  Radius = 0.75
FEATURE [App::DocumentObjectGroup] Group057
  Group = -> [Arc215,Arc214,Arc212,Arc213,Line426,Line425,Line432,Line431]
FEATURE [Part::Part2DObjectPython] Line434  # Draft 2D object (typed FeaturePython)
  ChamferSize = 0
  Closed = false
  End = (172.61,-73.5556,0)
  FilletRadius = 0
  Length = 12.5
  MakeFace = true
  Placement = pos=(160.11,-73.5556,0) rot=(0,0,1;0rad)
  Points = (2) [(0,0,0),(12.5,0,0)]
  Start = (160.11,-73.5556,0)
  Subdivisions = 0
FEATURE [Part::Part2DObjectPython] Arc216  # Draft 2D object (typed FeaturePython)
  FirstAngle = 90
  LastAngle = 180
  MakeFace = true
  Placement = pos=(172.61,-72.8056,0) rot=(0,0,1;3.14159rad)
  Radius = 0.75
FEATURE [Part::Part2DObjectPython] Line436  # Draft 2D object (typed FeaturePython)
  ChamferSize = 0
  Closed = false
  End = (159.36,-72.8056,0)
  FilletRadius = 0
  Length = 12.5
  MakeFace = true
  Placement = pos=(159.36,-60.3056,0) rot=(0,0,1;0rad)
  Points = (2) [(0,0,0),(0,-12.5,0)]
  Start = (159.36,-60.3056,0)
  Subdivisions = 0
FEATURE [Part::Part2DObjectPython] Arc217  # Draft 2D object (typed FeaturePython)
  FirstAngle = 90
  LastAngle = 180
  MakeFace = true
  Placement = pos=(172.61,-60.3056,0) rot=(0,0,-1;1.5708rad)
  Radius = 0.75
FEATURE [Part::Part2DObjectPython] Arc218  # Draft 2D object (typed FeaturePython)
  FirstAngle = 90
  LastAngle = 180
  MakeFace = true
  Placement = pos=(160.11,-60.3056,0) rot=(0,0,1;0rad)
  Radius = 0.75
FEATURE [Part::Part2DObjectPython] Line437  # Draft 2D object (typed FeaturePython)
  ChamferSize = 0
  Closed = false
  End = (160.11,-59.5556,0)
  FilletRadius = 0
  Length = 12.5
  MakeFace = true
  Placement = pos=(172.61,-59.5556,0) rot=(0,0,1;0rad)
  Points = (2) [(0,0,0),(-12.5,0,0)]
  Start = (172.61,-59.5556,0)
  Subdivisions = 0
FEATURE [Part::Part2DObjectPython] Arc219  # Draft 2D object (typed FeaturePython)
  FirstAngle = 90
  LastAngle = 180
  MakeFace = true
  Placement = pos=(160.11,-72.8056,0) rot=(0,0,1;1.5708rad)
  Radius = 0.75
FEATURE [Part::Part2DObjectPython] Line439  # Draft 2D object (typed FeaturePython)
  ChamferSize = 0
  Closed = false
  End = (173.36,-60.3056,0)
  FilletRadius = 0
  Length = 12.5
  MakeFace = true
  Placement = pos=(173.36,-72.8056,0) rot=(0,0,1;0rad)
  Points = (2) [(0,0,0),(0,12.5,0)]
  Start = (173.36,-72.8056,0)
  Subdivisions = 0
FEATURE [App::DocumentObjectGroup] Group058
  Group = -> [Arc218,Arc217,Arc219,Arc216,Line439,Line437,Line436,Line434]
FEATURE [Part::Part2DObjectPython] Arc220  # Draft 2D object (typed FeaturePython)
  FirstAngle = 90
  LastAngle = 180
  MakeFace = true
  Placement = pos=(179.119,-72.8056,0) rot=(0,0,1;1.5708rad)
  Radius = 0.75
FEATURE [Part::Part2DObjectPython] Arc221  # Draft 2D object (typed FeaturePython)
  FirstAngle = 90
  LastAngle = 180
  MakeFace = true
  Placement = pos=(191.619,-60.3056,0) rot=(0,0,-1;1.5708rad)
  Radius = 0.75
FEATURE [Part::Part2DObjectPython] Arc222  # Draft 2D object (typed FeaturePython)
  FirstAngle = 90
  LastAngle = 180
  MakeFace = true
  Placement = pos=(179.119,-60.3056,0) rot=(0,0,1;0rad)
  Radius = 0.75
FEATURE [Part::Part2DObjectPython] Line442  # Draft 2D object (typed FeaturePython)
  ChamferSize = 0
  Closed = false
  End = (179.119,-59.5556,0)
  FilletRadius = 0
  Length = 12.5
  MakeFace = true
  Placement = pos=(191.619,-59.5556,0) rot=(0,0,1;0rad)
  Points = (2) [(0,0,0),(-12.5,0,0)]
  Start = (191.619,-59.5556,0)
  Subdivisions = 0
FEATURE [Part::Part2DObjectPython] Line444  # Draft 2D object (typed FeaturePython)
  ChamferSize = 0
  Closed = false
  End = (178.369,-72.8056,0)
  FilletRadius = 0
  Length = 12.5
  MakeFace = true
  Placement = pos=(178.369,-60.3056,0) rot=(0,0,1;0rad)
  Points = (2) [(0,0,0),(0,-12.5,0)]
  Start = (178.369,-60.3056,0)
  Subdivisions = 0
FEATURE [Part::Part2DObjectPython] Line446  # Draft 2D object (typed FeaturePython)
  ChamferSize = 0
  Closed = false
  End = (191.619,-73.5556,0)
  FilletRadius = 0
  Length = 12.5
  MakeFace = true
  Placement = pos=(179.119,-73.5556,0) rot=(0,0,1;0rad)
  Points = (2) [(0,0,0),(12.5,0,0)]
  Start = (179.119,-73.5556,0)
  Subdivisions = 0
FEATURE [Part::Part2DObjectPython] Arc223  # Draft 2D object (typed FeaturePython)
  FirstAngle = 90
  LastAngle = 180
  MakeFace = true
  Placement = pos=(191.619,-72.8056,0) rot=(0,0,1;3.14159rad)
  Radius = 0.75
FEATURE [Part::Part2DObjectPython] Line448  # Draft 2D object (typed FeaturePython)
  ChamferSize = 0
  Closed = false
  End = (192.369,-60.3056,0)
  FilletRadius = 0
  Length = 12.5
  MakeFace = true
  Placement = pos=(192.369,-72.8056,0) rot=(0,0,1;0rad)
  Points = (2) [(0,0,0),(0,12.5,0)]
  Start = (192.369,-72.8056,0)
  Subdivisions = 0
FEATURE [App::DocumentObjectGroup] Group059
  Group = -> [Arc222,Arc221,Arc220,Arc223,Line448,Line442,Line444,Line446]
FEATURE [Part::Part2DObjectPython] Line450  # Draft 2D object (typed FeaturePython)
  ChamferSize = 0
  Closed = false
  End = (197.378,-72.8056,0)
  FilletRadius = 0
  Length = 12.5
  MakeFace = true
  Placement = pos=(197.378,-60.3056,0) rot=(0,0,1;0rad)
  Points = (2) [(0,0,0),(0,-12.5,0)]
  Start = (197.378,-60.3056,0)
  Subdivisions = 0
FEATURE [Part::Part2DObjectPython] Arc224  # Draft 2D object (typed FeaturePython)
  FirstAngle = 90
  LastAngle = 180
  MakeFace = true
  Placement = pos=(210.628,-72.8056,0) rot=(0,0,1;3.14159rad)
  Radius = 0.75
FEATURE [Part::Part2DObjectPython] Line453  # Draft 2D object (typed FeaturePython)
  ChamferSize = 0
  Closed = false
  End = (198.128,-59.5556,0)
  FilletRadius = 0
  Length = 12.5
  MakeFace = true
  Placement = pos=(210.628,-59.5556,0) rot=(0,0,1;0rad)
  Points = (2) [(0,0,0),(-12.5,0,0)]
  Start = (210.628,-59.5556,0)
  Subdivisions = 0
FEATURE [Part::Part2DObjectPython] Arc225  # Draft 2D object (typed FeaturePython)
  FirstAngle = 90
  LastAngle = 180
  MakeFace = true
  Placement = pos=(210.628,-60.3056,0) rot=(0,0,-1;1.5708rad)
  Radius = 0.75
FEATURE [Part::Part2DObjectPython] Arc226  # Draft 2D object (typed FeaturePython)
  FirstAngle = 90
  LastAngle = 180
  MakeFace = true
  Placement = pos=(198.128,-60.3056,0) rot=(0,0,1;0rad)
  Radius = 0.75
FEATURE [Part::Part2DObjectPython] Line455  # Draft 2D object (typed FeaturePython)
  ChamferSize = 0
  Closed = false
  End = (210.628,-73.5556,0)
  FilletRadius = 0
  Length = 12.5
  MakeFace = true
  Placement = pos=(198.128,-73.5556,0) rot=(0,0,1;0rad)
  Points = (2) [(0,0,0),(12.5,0,0)]
  Start = (198.128,-73.5556,0)
  Subdivisions = 0
FEATURE [Part::Part2DObjectPython] Line456  # Draft 2D object (typed FeaturePython)
  ChamferSize = 0
  Closed = false
  End = (211.378,-60.3056,0)
  FilletRadius = 0
  Length = 12.5
  MakeFace = true
  Placement = pos=(211.378,-72.8056,0) rot=(0,0,1;0rad)
  Points = (2) [(0,0,0),(0,12.5,0)]
  Start = (211.378,-72.8056,0)
  Subdivisions = 0
FEATURE [Part::Part2DObjectPython] Arc227  # Draft 2D object (typed FeaturePython)
  FirstAngle = 90
  LastAngle = 180
  MakeFace = true
  Placement = pos=(198.128,-72.8056,0) rot=(0,0,1;1.5708rad)
  Radius = 0.75
FEATURE [App::DocumentObjectGroup] Group060
  Group = -> [Arc226,Arc225,Arc227,Arc224,Line456,Line453,Line450,Line455]
FEATURE [Part::Part2DObjectPython] Line457  # Draft 2D object (typed FeaturePython)
  ChamferSize = 0
  Closed = false
  End = (216.388,-72.8056,0)
  FilletRadius = 0
  Length = 12.5
  MakeFace = true
  Placement = pos=(216.388,-60.3056,0) rot=(0,0,1;0rad)
  Points = (2) [(0,0,0),(0,-12.5,0)]
  Start = (216.388,-60.3056,0)
  Subdivisions = 0
FEATURE [Part::Part2DObjectPython] Arc228  # Draft 2D object (typed FeaturePython)
  FirstAngle = 90
  LastAngle = 180
  MakeFace = true
  Placement = pos=(229.638,-72.8056,0) rot=(0,0,1;3.14159rad)
  Radius = 0.75
FEATURE [Part::Part2DObjectPython] Arc229  # Draft 2D object (typed FeaturePython)
  FirstAngle = 90
  LastAngle = 180
  MakeFace = true
  Placement = pos=(217.138,-72.8056,0) rot=(0,0,1;1.5708rad)
  Radius = 0.75
FEATURE [Part::Part2DObjectPython] Line458  # Draft 2D object (typed FeaturePython)
  ChamferSize = 0
  Closed = false
  End = (229.638,-73.5556,0)
  FilletRadius = 0
  Length = 12.5
  MakeFace = true
  Placement = pos=(217.138,-73.5556,0) rot=(0,0,1;0rad)
  Points = (2) [(0,0,0),(12.5,0,0)]
  Start = (217.138,-73.5556,0)
  Subdivisions = 0
FEATURE [Part::Part2DObjectPython] Arc230  # Draft 2D object (typed FeaturePython)
  FirstAngle = 90
  LastAngle = 180
  MakeFace = true
  Placement = pos=(229.638,-60.3056,0) rot=(0,0,-1;1.5708rad)
  Radius = 0.75
FEATURE [Part::Part2DObjectPython] Line461  # Draft 2D object (typed FeaturePython)
  ChamferSize = 0
  Closed = false
  End = (217.138,-59.5556,0)
  FilletRadius = 0
  Length = 12.5
  MakeFace = true
  Placement = pos=(229.638,-59.5556,0) rot=(0,0,1;0rad)
  Points = (2) [(0,0,0),(-12.5,0,0)]
  Start = (229.638,-59.5556,0)
  Subdivisions = 0
FEATURE [Part::Part2DObjectPython] Line464  # Draft 2D object (typed FeaturePython)
  ChamferSize = 0
  Closed = false
  End = (230.388,-60.3056,0)
  FilletRadius = 0
  Length = 12.5
  MakeFace = true
  Placement = pos=(230.388,-72.8056,0) rot=(0,0,1;0rad)
  Points = (2) [(0,0,0),(0,12.5,0)]
  Start = (230.388,-72.8056,0)
  Subdivisions = 0
FEATURE [Part::Part2DObjectPython] Arc231  # Draft 2D object (typed FeaturePython)
  FirstAngle = 90
  LastAngle = 180
  MakeFace = true
  Placement = pos=(217.138,-60.3056,0) rot=(0,0,1;0rad)
  Radius = 0.75
FEATURE [App::DocumentObjectGroup] Group061
  Group = -> [Arc231,Arc230,Arc229,Arc228,Line464,Line461,Line457,Line458]
FEATURE [Part::Part2DObjectPython] Line466  # Draft 2D object (typed FeaturePython)
  ChamferSize = 0
  Closed = false
  End = (260.529,-73.5556,0)
  FilletRadius = 0
  Length = 12.5
  MakeFace = true
  Placement = pos=(248.029,-73.5556,0) rot=(0,0,1;0rad)
  Points = (2) [(0,0,0),(12.5,0,0)]
  Start = (248.029,-73.5556,0)
  Subdivisions = 0
FEATURE [Part::Part2DObjectPython] Line468  # Draft 2D object (typed FeaturePython)
  ChamferSize = 0
  Closed = false
  End = (247.279,-72.8056,0)
  FilletRadius = 0
  Length = 12.5
  MakeFace = true
  Placement = pos=(247.279,-60.3056,0) rot=(0,0,1;0rad)
  Points = (2) [(0,0,0),(0,-12.5,0)]
  Start = (247.279,-60.3056,0)
  Subdivisions = 0
FEATURE [Part::Part2DObjectPython] Arc232  # Draft 2D object (typed FeaturePython)
  FirstAngle = 90
  LastAngle = 180
  MakeFace = true
  Placement = pos=(260.529,-72.8056,0) rot=(0,0,1;3.14159rad)
  Radius = 0.75
FEATURE [Part::Part2DObjectPython] Arc233  # Draft 2D object (typed FeaturePython)
  FirstAngle = 90
  LastAngle = 180
  MakeFace = true
  Placement = pos=(248.029,-72.8056,0) rot=(0,0,1;1.5708rad)
  Radius = 0.75
FEATURE [Part::Part2DObjectPython] Arc234  # Draft 2D object (typed FeaturePython)
  FirstAngle = 90
  LastAngle = 180
  MakeFace = true
  Placement = pos=(260.529,-60.3056,0) rot=(0,0,-1;1.5708rad)
  Radius = 0.75
FEATURE [Part::Part2DObjectPython] Line469  # Draft 2D object (typed FeaturePython)
  ChamferSize = 0
  Closed = false
  End = (248.029,-59.5556,0)
  FilletRadius = 0
  Length = 12.5
  MakeFace = true
  Placement = pos=(260.529,-59.5556,0) rot=(0,0,1;0rad)
  Points = (2) [(0,0,0),(-12.5,0,0)]
  Start = (260.529,-59.5556,0)
  Subdivisions = 0
FEATURE [Part::Part2DObjectPython] Line472  # Draft 2D object (typed FeaturePython)
  ChamferSize = 0
  Closed = false
  End = (261.279,-60.3056,0)
  FilletRadius = 0
  Length = 12.5
  MakeFace = true
  Placement = pos=(261.279,-72.8056,0) rot=(0,0,1;0rad)
  Points = (2) [(0,0,0),(0,12.5,0)]
  Start = (261.279,-72.8056,0)
  Subdivisions = 0
FEATURE [Part::Part2DObjectPython] Arc235  # Draft 2D object (typed FeaturePython)
  FirstAngle = 90
  LastAngle = 180
  MakeFace = true
  Placement = pos=(248.029,-60.3056,0) rot=(0,0,1;0rad)
  Radius = 0.75
FEATURE [Part::Part2DObjectPython] Line474  # Draft 2D object (typed FeaturePython)
  ChamferSize = 0
  Closed = false
  End = (278.422,-72.8056,0)
  FilletRadius = 0
  Length = 12.5
  MakeFace = true
  Placement = pos=(278.422,-60.3056,0) rot=(0,0,1;0rad)
  Points = (2) [(0,0,0),(0,-12.5,0)]
  Start = (278.422,-60.3056,0)
  Subdivisions = 0
FEATURE [Part::Part2DObjectPython] Arc236  # Draft 2D object (typed FeaturePython)
  FirstAngle = 90
  LastAngle = 180
  MakeFace = true
  Placement = pos=(291.672,-60.3056,0) rot=(0,0,-1;1.5708rad)
  Radius = 0.75
FEATURE [Part::Part2DObjectPython] Line476  # Draft 2D object (typed FeaturePython)
  ChamferSize = 0
  Closed = false
  End = (291.672,-73.5556,0)
  FilletRadius = 0
  Length = 12.5
  MakeFace = true
  Placement = pos=(279.172,-73.5556,0) rot=(0,0,1;0rad)
  Points = (2) [(0,0,0),(12.5,0,0)]
  Start = (279.172,-73.5556,0)
  Subdivisions = 0
FEATURE [Part::Part2DObjectPython] Arc237  # Draft 2D object (typed FeaturePython)
  FirstAngle = 90
  LastAngle = 180
  MakeFace = true
  Placement = pos=(291.672,-72.8056,0) rot=(0,0,1;3.14159rad)
  Radius = 0.75
FEATURE [Part::Part2DObjectPython] Arc238  # Draft 2D object (typed FeaturePython)
  FirstAngle = 90
  LastAngle = 180
  MakeFace = true
  Placement = pos=(279.172,-72.8056,0) rot=(0,0,1;1.5708rad)
  Radius = 0.75
FEATURE [Part::Part2DObjectPython] Line478  # Draft 2D object (typed FeaturePython)
  ChamferSize = 0
  Closed = false
  End = (279.172,-59.5556,0)
  FilletRadius = 0
  Length = 12.5
  MakeFace = true
  Placement = pos=(291.672,-59.5556,0) rot=(0,0,1;0rad)
  Points = (2) [(0,0,0),(-12.5,0,0)]
  Start = (291.672,-59.5556,0)
  Subdivisions = 0
FEATURE [Part::Part2DObjectPython] Line480  # Draft 2D object (typed FeaturePython)
  ChamferSize = 0
  Closed = false
  End = (292.422,-60.3056,0)
  FilletRadius = 0
  Length = 12.5
  MakeFace = true
  Placement = pos=(292.422,-72.8056,0) rot=(0,0,1;0rad)
  Points = (2) [(0,0,0),(0,12.5,0)]
  Start = (292.422,-72.8056,0)
  Subdivisions = 0
FEATURE [Part::Part2DObjectPython] Arc239  # Draft 2D object (typed FeaturePython)
  FirstAngle = 90
  LastAngle = 180
  MakeFace = true
  Placement = pos=(279.172,-60.3056,0) rot=(0,0,1;0rad)
  Radius = 0.75
FEATURE [App::DocumentObjectGroup] Group063
  Group = -> [Arc239,Arc236,Arc238,Arc237,Line480,Line478,Line474,Line476]
FEATURE [Part::Part2DObjectPython] Arc240  # Draft 2D object (typed FeaturePython)
  FirstAngle = 90
  LastAngle = 180
  MakeFace = true
  Placement = pos=(5.65244,-79.315,0) rot=(0,0,1;0rad)
  Radius = 0.75
FEATURE [Part::Part2DObjectPython] Line482  # Draft 2D object (typed FeaturePython)
  ChamferSize = 0
  Closed = false
  End = (18.9024,-79.315,0)
  FilletRadius = 0
  Length = 12.5
  MakeFace = true
  Placement = pos=(18.9024,-91.815,0) rot=(0,0,1;0rad)
  Points = (2) [(0,0,0),(0,12.5,0)]
  Start = (18.9024,-91.815,0)
  Subdivisions = 0
FEATURE [Part::Part2DObjectPython] Arc241  # Draft 2D object (typed FeaturePython)
  FirstAngle = 90
  LastAngle = 180
  MakeFace = true
  Placement = pos=(18.1524,-79.315,0) rot=(0,0,-1;1.5708rad)
  Radius = 0.75
FEATURE [Part::Part2DObjectPython] Line485  # Draft 2D object (typed FeaturePython)
  ChamferSize = 0
  Closed = false
  End = (4.90244,-91.815,0)
  FilletRadius = 0
  Length = 12.5
  MakeFace = true
  Placement = pos=(4.90244,-79.315,0) rot=(0,0,1;0rad)
  Points = (2) [(0,0,0),(0,-12.5,0)]
  Start = (4.90244,-79.315,0)
  Subdivisions = 0
FEATURE [Part::Part2DObjectPython] Arc242  # Draft 2D object (typed FeaturePython)
  FirstAngle = 90
  LastAngle = 180
  MakeFace = true
  Placement = pos=(5.65244,-91.815,0) rot=(0,0,1;1.5708rad)
  Radius = 0.75
FEATURE [Part::Part2DObjectPython] Line486  # Draft 2D object (typed FeaturePython)
  ChamferSize = 0
  Closed = false
  End = (18.1524,-92.565,0)
  FilletRadius = 0
  Length = 12.5
  MakeFace = true
  Placement = pos=(5.65244,-92.565,0) rot=(0,0,1;0rad)
  Points = (2) [(0,0,0),(12.5,0,0)]
  Start = (5.65244,-92.565,0)
  Subdivisions = 0
FEATURE [Part::Part2DObjectPython] Arc243  # Draft 2D object (typed FeaturePython)
  FirstAngle = 90
  LastAngle = 180
  MakeFace = true
  Placement = pos=(18.1524,-91.815,0) rot=(0,0,1;3.14159rad)
  Radius = 0.75
FEATURE [Part::Part2DObjectPython] Line488  # Draft 2D object (typed FeaturePython)
  ChamferSize = 0
  Closed = false
  End = (5.65244,-78.565,0)
  FilletRadius = 0
  Length = 12.5
  MakeFace = true
  Placement = pos=(18.1524,-78.565,0) rot=(0,0,1;0rad)
  Points = (2) [(0,0,0),(-12.5,0,0)]
  Start = (18.1524,-78.565,0)
  Subdivisions = 0
FEATURE [App::DocumentObjectGroup] Group065
  Group = -> [Arc240,Arc241,Arc242,Arc243,Line482,Line488,Line485,Line486]
FEATURE [Part::Part2DObjectPython] Line489  # Draft 2D object (typed FeaturePython)
  ChamferSize = 0
  Closed = false
  End = (40.2892,-79.315,0)
  FilletRadius = 0
  Length = 12.5
  MakeFace = true
  Placement = pos=(40.2892,-91.815,0) rot=(0,0,1;0rad)
  Points = (2) [(0,0,0),(0,12.5,0)]
  Start = (40.2892,-91.815,0)
  Subdivisions = 0
FEATURE [Part::Part2DObjectPython] Line490  # Draft 2D object (typed FeaturePython)
  ChamferSize = 0
  Closed = false
  End = (39.5392,-92.565,0)
  FilletRadius = 0
  Length = 12.5
  MakeFace = true
  Placement = pos=(27.0392,-92.565,0) rot=(0,0,1;0rad)
  Points = (2) [(0,0,0),(12.5,0,0)]
  Start = (27.0392,-92.565,0)
  Subdivisions = 0
FEATURE [Part::Part2DObjectPython] Arc244  # Draft 2D object (typed FeaturePython)
  FirstAngle = 90
  LastAngle = 180
  MakeFace = true
  Placement = pos=(27.0392,-79.315,0) rot=(0,0,1;0rad)
  Radius = 0.75
FEATURE [Part::Part2DObjectPython] Line492  # Draft 2D object (typed FeaturePython)
  ChamferSize = 0
  Closed = false
  End = (26.2892,-91.815,0)
  FilletRadius = 0
  Length = 12.5
  MakeFace = true
  Placement = pos=(26.2892,-79.315,0) rot=(0,0,1;0rad)
  Points = (2) [(0,0,0),(0,-12.5,0)]
  Start = (26.2892,-79.315,0)
  Subdivisions = 0
FEATURE [Part::Part2DObjectPython] Arc245  # Draft 2D object (typed FeaturePython)
  FirstAngle = 90
  LastAngle = 180
  MakeFace = true
  Placement = pos=(27.0392,-91.815,0) rot=(0,0,1;1.5708rad)
  Radius = 0.75
FEATURE [Part::Part2DObjectPython] Line495  # Draft 2D object (typed FeaturePython)
  ChamferSize = 0
  Closed = false
  End = (27.0392,-78.565,0)
  FilletRadius = 0
  Length = 12.5
  MakeFace = true
  Placement = pos=(39.5392,-78.565,0) rot=(0,0,1;0rad)
  Points = (2) [(0,0,0),(-12.5,0,0)]
  Start = (39.5392,-78.565,0)
  Subdivisions = 0
FEATURE [Part::Part2DObjectPython] Arc246  # Draft 2D object (typed FeaturePython)
  FirstAngle = 90
  LastAngle = 180
  MakeFace = true
  Placement = pos=(39.5392,-79.315,0) rot=(0,0,-1;1.5708rad)
  Radius = 0.75
FEATURE [Part::Part2DObjectPython] Arc247  # Draft 2D object (typed FeaturePython)
  FirstAngle = 90
  LastAngle = 180
  MakeFace = true
  Placement = pos=(39.5392,-91.815,0) rot=(0,0,1;3.14159rad)
  Radius = 0.75
FEATURE [App::DocumentObjectGroup] Group066
  Group = -> [Arc244,Arc246,Arc245,Arc247,Line489,Line495,Line492,Line490]
FEATURE [Part::Part2DObjectPython] Line497  # Draft 2D object (typed FeaturePython)
  ChamferSize = 0
  Closed = false
  End = (61.676,-79.315,0)
  FilletRadius = 0
  Length = 12.5
  MakeFace = true
  Placement = pos=(61.676,-91.815,0) rot=(0,0,1;0rad)
  Points = (2) [(0,0,0),(0,12.5,0)]
  Start = (61.676,-91.815,0)
  Subdivisions = 0
FEATURE [Part::Part2DObjectPython] Arc248  # Draft 2D object (typed FeaturePython)
  FirstAngle = 90
  LastAngle = 180
  MakeFace = true
  Placement = pos=(48.426,-79.315,0) rot=(0,0,1;0rad)
  Radius = 0.75
FEATURE [Part::Part2DObjectPython] Line501  # Draft 2D object (typed FeaturePython)
  ChamferSize = 0
  Closed = false
  End = (47.676,-91.815,0)
  FilletRadius = 0
  Length = 12.5
  MakeFace = true
  Placement = pos=(47.676,-79.315,0) rot=(0,0,1;0rad)
  Points = (2) [(0,0,0),(0,-12.5,0)]
  Start = (47.676,-79.315,0)
  Subdivisions = 0
FEATURE [Part::Part2DObjectPython] Arc249  # Draft 2D object (typed FeaturePython)
  FirstAngle = 90
  LastAngle = 180
  MakeFace = true
  Placement = pos=(48.426,-91.815,0) rot=(0,0,1;1.5708rad)
  Radius = 0.75
FEATURE [Part::Part2DObjectPython] Line503  # Draft 2D object (typed FeaturePython)
  ChamferSize = 0
  Closed = false
  End = (60.926,-92.565,0)
  FilletRadius = 0
  Length = 12.5
  MakeFace = true
  Placement = pos=(48.426,-92.565,0) rot=(0,0,1;0rad)
  Points = (2) [(0,0,0),(12.5,0,0)]
  Start = (48.426,-92.565,0)
  Subdivisions = 0
FEATURE [Part::Part2DObjectPython] Line504  # Draft 2D object (typed FeaturePython)
  ChamferSize = 0
  Closed = false
  End = (48.426,-78.565,0)
  FilletRadius = 0
  Length = 12.5
  MakeFace = true
  Placement = pos=(60.926,-78.565,0) rot=(0,0,1;0rad)
  Points = (2) [(0,0,0),(-12.5,0,0)]
  Start = (60.926,-78.565,0)
  Subdivisions = 0
FEATURE [Part::Part2DObjectPython] Arc250  # Draft 2D object (typed FeaturePython)
  FirstAngle = 90
  LastAngle = 180
  MakeFace = true
  Placement = pos=(60.926,-79.315,0) rot=(0,0,-1;1.5708rad)
  Radius = 0.75
FEATURE [Part::Part2DObjectPython] Arc251  # Draft 2D object (typed FeaturePython)
  FirstAngle = 90
  LastAngle = 180
  MakeFace = true
  Placement = pos=(60.926,-91.815,0) rot=(0,0,1;3.14159rad)
  Radius = 0.75
FEATURE [App::DocumentObjectGroup] Group067
  Group = -> [Arc248,Arc250,Arc249,Arc251,Line497,Line504,Line501,Line503]
FEATURE [Part::Part2DObjectPython] Arc252  # Draft 2D object (typed FeaturePython)
  FirstAngle = 90
  LastAngle = 180
  MakeFace = true
  Placement = pos=(132.211,-79.315,0) rot=(0,0,-1;1.5708rad)
  Radius = 0.75
FEATURE [Part::Part2DObjectPython] Line508  # Draft 2D object (typed FeaturePython)
  ChamferSize = 0
  Closed = false
  End = (132.961,-79.315,0)
  FilletRadius = 0
  Length = 12.5
  MakeFace = true
  Placement = pos=(132.961,-91.815,0) rot=(0,0,1;0rad)
  Points = (2) [(0,0,0),(0,12.5,0)]
  Start = (132.961,-91.815,0)
  Subdivisions = 0
FEATURE [Part::Part2DObjectPython] Arc253  # Draft 2D object (typed FeaturePython)
  FirstAngle = 90
  LastAngle = 180
  MakeFace = true
  Placement = pos=(119.711,-79.315,0) rot=(0,0,1;0rad)
  Radius = 0.75
FEATURE [Part::Part2DObjectPython] Line510  # Draft 2D object (typed FeaturePython)
  ChamferSize = 0
  Closed = false
  End = (118.961,-91.815,0)
  FilletRadius = 0
  Length = 12.5
  MakeFace = true
  Placement = pos=(118.961,-79.315,0) rot=(0,0,1;0rad)
  Points = (2) [(0,0,0),(0,-12.5,0)]
  Start = (118.961,-79.315,0)
  Subdivisions = 0
FEATURE [Part::Part2DObjectPython] Line511  # Draft 2D object (typed FeaturePython)
  ChamferSize = 0
  Closed = false
  End = (132.211,-92.565,0)
  FilletRadius = 0
  Length = 12.5
  MakeFace = true
  Placement = pos=(119.711,-92.565,0) rot=(0,0,1;0rad)
  Points = (2) [(0,0,0),(12.5,0,0)]
  Start = (119.711,-92.565,0)
  Subdivisions = 0
FEATURE [Part::Part2DObjectPython] Arc254  # Draft 2D object (typed FeaturePython)
  FirstAngle = 90
  LastAngle = 180
  MakeFace = true
  Placement = pos=(119.711,-91.815,0) rot=(0,0,1;1.5708rad)
  Radius = 0.75
FEATURE [Part::Part2DObjectPython] Line512  # Draft 2D object (typed FeaturePython)
  ChamferSize = 0
  Closed = false
  End = (119.711,-78.565,0)
  FilletRadius = 0
  Length = 12.5
  MakeFace = true
  Placement = pos=(132.211,-78.565,0) rot=(0,0,1;0rad)
  Points = (2) [(0,0,0),(-12.5,0,0)]
  Start = (132.211,-78.565,0)
  Subdivisions = 0
FEATURE [Part::Part2DObjectPython] Arc255  # Draft 2D object (typed FeaturePython)
  FirstAngle = 90
  LastAngle = 180
  MakeFace = true
  Placement = pos=(132.211,-91.815,0) rot=(0,0,1;3.14159rad)
  Radius = 0.75
FEATURE [Part::Part2DObjectPython] Line513  # Draft 2D object (typed FeaturePython)
  ChamferSize = 0
  Closed = false
  End = (190.299,-91.815,0)
  FilletRadius = 0
  Length = 12.5
  MakeFace = true
  Placement = pos=(190.299,-79.315,0) rot=(0,0,1;0rad)
  Points = (2) [(0,0,0),(0,-12.5,0)]
  Start = (190.299,-79.315,0)
  Subdivisions = 0
FEATURE [Part::Part2DObjectPython] Arc256  # Draft 2D object (typed FeaturePython)
  FirstAngle = 90
  LastAngle = 180
  MakeFace = true
  Placement = pos=(203.549,-91.815,0) rot=(0,0,1;3.14159rad)
  Radius = 0.75
FEATURE [Part::Part2DObjectPython] Line517  # Draft 2D object (typed FeaturePython)
  ChamferSize = 0
  Closed = false
  End = (204.299,-79.315,0)
  FilletRadius = 0
  Length = 12.5
  MakeFace = true
  Placement = pos=(204.299,-91.815,0) rot=(0,0,1;0rad)
  Points = (2) [(0,0,0),(0,12.5,0)]
  Start = (204.299,-91.815,0)
  Subdivisions = 0
FEATURE [Part::Part2DObjectPython] Line518  # Draft 2D object (typed FeaturePython)
  ChamferSize = 0
  Closed = false
  End = (203.549,-92.565,0)
  FilletRadius = 0
  Length = 12.5
  MakeFace = true
  Placement = pos=(191.049,-92.565,0) rot=(0,0,1;0rad)
  Points = (2) [(0,0,0),(12.5,0,0)]
  Start = (191.049,-92.565,0)
  Subdivisions = 0
FEATURE [Part::Part2DObjectPython] Arc257  # Draft 2D object (typed FeaturePython)
  FirstAngle = 90
  LastAngle = 180
  MakeFace = true
  Placement = pos=(191.049,-79.315,0) rot=(0,0,1;0rad)
  Radius = 0.75
FEATURE [Part::Part2DObjectPython] Line519  # Draft 2D object (typed FeaturePython)
  ChamferSize = 0
  Closed = false
  End = (191.049,-78.565,0)
  FilletRadius = 0
  Length = 12.5
  MakeFace = true
  Placement = pos=(203.549,-78.565,0) rot=(0,0,1;0rad)
  Points = (2) [(0,0,0),(-12.5,0,0)]
  Start = (203.549,-78.565,0)
  Subdivisions = 0
FEATURE [Part::Part2DObjectPython] Arc258  # Draft 2D object (typed FeaturePython)
  FirstAngle = 90
  LastAngle = 180
  MakeFace = true
  Placement = pos=(203.549,-79.315,0) rot=(0,0,-1;1.5708rad)
  Radius = 0.75
FEATURE [Part::Part2DObjectPython] Arc259  # Draft 2D object (typed FeaturePython)
  FirstAngle = 90
  LastAngle = 180
  MakeFace = true
  Placement = pos=(191.049,-91.815,0) rot=(0,0,1;1.5708rad)
  Radius = 0.75
FEATURE [App::DocumentObjectGroup] Group069
  Group = -> [Arc257,Arc258,Arc259,Arc256,Line517,Line519,Line513,Line518]
FEATURE [Part::Part2DObjectPython] Line521  # Draft 2D object (typed FeaturePython)
  ChamferSize = 0
  Closed = false
  End = (228.112,-79.315,0)
  FilletRadius = 0
  Length = 12.5
  MakeFace = true
  Placement = pos=(228.112,-91.815,0) rot=(0,0,1;0rad)
  Points = (2) [(0,0,0),(0,12.5,0)]
  Start = (228.112,-91.815,0)
  Subdivisions = 0
FEATURE [Part::Part2DObjectPython] Arc260  # Draft 2D object (typed FeaturePython)
  FirstAngle = 90
  LastAngle = 180
  MakeFace = true
  Placement = pos=(214.862,-79.315,0) rot=(0,0,1;0rad)
  Radius = 0.75
FEATURE [Part::Part2DObjectPython] Line523  # Draft 2D object (typed FeaturePython)
  ChamferSize = 0
  Closed = false
  End = (227.362,-92.565,0)
  FilletRadius = 0
  Length = 12.5
  MakeFace = true
  Placement = pos=(214.862,-92.565,0) rot=(0,0,1;0rad)
  Points = (2) [(0,0,0),(12.5,0,0)]
  Start = (214.862,-92.565,0)
  Subdivisions = 0
FEATURE [Part::Part2DObjectPython] Line524  # Draft 2D object (typed FeaturePython)
  ChamferSize = 0
  Closed = false
  End = (214.862,-78.565,0)
  FilletRadius = 0
  Length = 12.5
  MakeFace = true
  Placement = pos=(227.362,-78.565,0) rot=(0,0,1;0rad)
  Points = (2) [(0,0,0),(-12.5,0,0)]
  Start = (227.362,-78.565,0)
  Subdivisions = 0
FEATURE [Part::Part2DObjectPython] Line525  # Draft 2D object (typed FeaturePython)
  ChamferSize = 0
  Closed = false
  End = (214.112,-91.815,0)
  FilletRadius = 0
  Length = 12.5
  MakeFace = true
  Placement = pos=(214.112,-79.315,0) rot=(0,0,1;0rad)
  Points = (2) [(0,0,0),(0,-12.5,0)]
  Start = (214.112,-79.315,0)
  Subdivisions = 0
FEATURE [Part::Part2DObjectPython] Arc261  # Draft 2D object (typed FeaturePython)
  FirstAngle = 90
  LastAngle = 180
  MakeFace = true
  Placement = pos=(227.362,-91.815,0) rot=(0,0,1;3.14159rad)
  Radius = 0.75
FEATURE [Part::Part2DObjectPython] Arc262  # Draft 2D object (typed FeaturePython)
  FirstAngle = 90
  LastAngle = 180
  MakeFace = true
  Placement = pos=(227.362,-79.315,0) rot=(0,0,-1;1.5708rad)
  Radius = 0.75
FEATURE [Part::Part2DObjectPython] Arc263  # Draft 2D object (typed FeaturePython)
  FirstAngle = 90
  LastAngle = 180
  MakeFace = true
  Placement = pos=(214.862,-91.815,0) rot=(0,0,1;1.5708rad)
  Radius = 0.75
FEATURE [App::DocumentObjectGroup] Group070
  Group = -> [Arc260,Arc262,Arc263,Arc261,Line521,Line524,Line525,Line523]
FEATURE [Part::Part2DObjectPython] Line529  # Draft 2D object (typed FeaturePython)
  ChamferSize = 0
  Closed = false
  End = (251.924,-79.315,0)
  FilletRadius = 0
  Length = 12.5
  MakeFace = true
  Placement = pos=(251.924,-91.815,0) rot=(0,0,1;0rad)
  Points = (2) [(0,0,0),(0,12.5,0)]
  Start = (251.924,-91.815,0)
  Subdivisions = 0
FEATURE [Part::Part2DObjectPython] Arc264  # Draft 2D object (typed FeaturePython)
  FirstAngle = 90
  LastAngle = 180
  MakeFace = true
  Placement = pos=(251.174,-79.315,0) rot=(0,0,-1;1.5708rad)
  Radius = 0.75
FEATURE [Part::Part2DObjectPython] Arc265  # Draft 2D object (typed FeaturePython)
  FirstAngle = 90
  LastAngle = 180
  MakeFace = true
  Placement = pos=(238.674,-79.315,0) rot=(0,0,1;0rad)
  Radius = 0.75
FEATURE [Part::Part2DObjectPython] Arc266  # Draft 2D object (typed FeaturePython)
  FirstAngle = 90
  LastAngle = 180
  MakeFace = true
  Placement = pos=(251.174,-91.815,0) rot=(0,0,1;3.14159rad)
  Radius = 0.75
FEATURE [Part::Part2DObjectPython] Arc267  # Draft 2D object (typed FeaturePython)
  FirstAngle = 90
  LastAngle = 180
  MakeFace = true
  Placement = pos=(238.674,-91.815,0) rot=(0,0,1;1.5708rad)
  Radius = 0.75
FEATURE [Part::Part2DObjectPython] Line533  # Draft 2D object (typed FeaturePython)
  ChamferSize = 0
  Closed = false
  End = (237.924,-91.815,0)
  FilletRadius = 0
  Length = 12.5
  MakeFace = true
  Placement = pos=(237.924,-79.315,0) rot=(0,0,1;0rad)
  Points = (2) [(0,0,0),(0,-12.5,0)]
  Start = (237.924,-79.315,0)
  Subdivisions = 0
FEATURE [Part::Part2DObjectPython] Line535  # Draft 2D object (typed FeaturePython)
  ChamferSize = 0
  Closed = false
  End = (238.674,-78.565,0)
  FilletRadius = 0
  Length = 12.5
  MakeFace = true
  Placement = pos=(251.174,-78.565,0) rot=(0,0,1;0rad)
  Points = (2) [(0,0,0),(-12.5,0,0)]
  Start = (251.174,-78.565,0)
  Subdivisions = 0
FEATURE [Part::Part2DObjectPython] Line536  # Draft 2D object (typed FeaturePython)
  ChamferSize = 0
  Closed = false
  End = (251.174,-92.565,0)
  FilletRadius = 0
  Length = 12.5
  MakeFace = true
  Placement = pos=(238.674,-92.565,0) rot=(0,0,1;0rad)
  Points = (2) [(0,0,0),(12.5,0,0)]
  Start = (238.674,-92.565,0)
  Subdivisions = 0
FEATURE [App::DocumentObjectGroup] Group071
  Group = -> [Arc265,Arc264,Arc267,Arc266,Line529,Line535,Line533,Line536]
FEATURE [Part::Part2DObjectPython] Arc268  # Draft 2D object (typed FeaturePython)
  FirstAngle = 90
  LastAngle = 180
  MakeFace = true
  Placement = pos=(260.112,-91.815,0) rot=(0,0,1;1.5708rad)
  Radius = 0.75
FEATURE [Part::Part2DObjectPython] Line540  # Draft 2D object (typed FeaturePython)
  ChamferSize = 0
  Closed = false
  End = (259.362,-91.815,0)
  FilletRadius = 0
  Length = 12.5
  MakeFace = true
  Placement = pos=(259.362,-79.315,0) rot=(0,0,1;0rad)
  Points = (2) [(0,0,0),(0,-12.5,0)]
  Start = (259.362,-79.315,0)
  Subdivisions = 0
FEATURE [Part::Part2DObjectPython] Arc269  # Draft 2D object (typed FeaturePython)
  FirstAngle = 90
  LastAngle = 180
  MakeFace = true
  Placement = pos=(272.612,-91.815,0) rot=(0,0,1;3.14159rad)
  Radius = 0.75
FEATURE [Part::Part2DObjectPython] Line541  # Draft 2D object (typed FeaturePython)
  ChamferSize = 0
  Closed = false
  End = (273.362,-79.315,0)
  FilletRadius = 0
  Length = 12.5
  MakeFace = true
  Placement = pos=(273.362,-91.815,0) rot=(0,0,1;0rad)
  Points = (2) [(0,0,0),(0,12.5,0)]
  Start = (273.362,-91.815,0)
  Subdivisions = 0
FEATURE [Part::Part2DObjectPython] Arc270  # Draft 2D object (typed FeaturePython)
  FirstAngle = 90
  LastAngle = 180
  MakeFace = true
  Placement = pos=(260.112,-79.315,0) rot=(0,0,1;0rad)
  Radius = 0.75
FEATURE [Part::Part2DObjectPython] Line543  # Draft 2D object (typed FeaturePython)
  ChamferSize = 0
  Closed = false
  End = (260.112,-78.565,0)
  FilletRadius = 0
  Length = 12.5
  MakeFace = true
  Placement = pos=(272.612,-78.565,0) rot=(0,0,1;0rad)
  Points = (2) [(0,0,0),(-12.5,0,0)]
  Start = (272.612,-78.565,0)
  Subdivisions = 0
FEATURE [Part::Part2DObjectPython] Arc271  # Draft 2D object (typed FeaturePython)
  FirstAngle = 90
  LastAngle = 180
  MakeFace = true
  Placement = pos=(272.612,-79.315,0) rot=(0,0,-1;1.5708rad)
  Radius = 0.75
FEATURE [Part::Part2DObjectPython] Line544  # Draft 2D object (typed FeaturePython)
  ChamferSize = 0
  Closed = false
  End = (272.612,-92.565,0)
  FilletRadius = 0
  Length = 12.5
  MakeFace = true
  Placement = pos=(260.112,-92.565,0) rot=(0,0,1;0rad)
  Points = (2) [(0,0,0),(12.5,0,0)]
  Start = (260.112,-92.565,0)
  Subdivisions = 0
FEATURE [App::DocumentObjectGroup] Group072
  Group = -> [Arc270,Arc271,Arc268,Arc269,Line541,Line543,Line540,Line544]
FEATURE [Part::Part2DObjectPython] Line545  # Draft 2D object (typed FeaturePython)
  ChamferSize = 0
  Closed = false
  End = (278.422,-91.815,0)
  FilletRadius = 0
  Length = 12.5
  MakeFace = true
  Placement = pos=(278.422,-79.315,0) rot=(0,0,1;0rad)
  Points = (2) [(0,0,0),(0,-12.5,0)]
  Start = (278.422,-79.315,0)
  Subdivisions = 0
FEATURE [Part::Part2DObjectPython] Line546  # Draft 2D object (typed FeaturePython)
  ChamferSize = 0
  Closed = false
  End = (292.422,-79.315,0)
  FilletRadius = 0
  Length = 12.5
  MakeFace = true
  Placement = pos=(292.422,-91.815,0) rot=(0,0,1;0rad)
  Points = (2) [(0,0,0),(0,12.5,0)]
  Start = (292.422,-91.815,0)
  Subdivisions = 0
FEATURE [Part::Part2DObjectPython] Arc272  # Draft 2D object (typed FeaturePython)
  FirstAngle = 90
  LastAngle = 180
  MakeFace = true
  Placement = pos=(279.172,-91.815,0) rot=(0,0,1;1.5708rad)
  Radius = 0.75
FEATURE [Part::Part2DObjectPython] Arc273  # Draft 2D object (typed FeaturePython)
  FirstAngle = 90
  LastAngle = 180
  MakeFace = true
  Placement = pos=(291.672,-91.815,0) rot=(0,0,1;3.14159rad)
  Radius = 0.75
FEATURE [Part::Part2DObjectPython] Arc274  # Draft 2D object (typed FeaturePython)
  FirstAngle = 90
  LastAngle = 180
  MakeFace = true
  Placement = pos=(279.172,-79.315,0) rot=(0,0,1;0rad)
  Radius = 0.75
FEATURE [Part::Part2DObjectPython] Line551  # Draft 2D object (typed FeaturePython)
  ChamferSize = 0
  Closed = false
  End = (279.172,-78.565,0)
  FilletRadius = 0
  Length = 12.5
  MakeFace = true
  Placement = pos=(291.672,-78.565,0) rot=(0,0,1;0rad)
  Points = (2) [(0,0,0),(-12.5,0,0)]
  Start = (291.672,-78.565,0)
  Subdivisions = 0
FEATURE [Part::Part2DObjectPython] Arc275  # Draft 2D object (typed FeaturePython)
  FirstAngle = 90
  LastAngle = 180
  MakeFace = true
  Placement = pos=(291.672,-79.315,0) rot=(0,0,-1;1.5708rad)
  Radius = 0.75
FEATURE [Part::Part2DObjectPython] Line552  # Draft 2D object (typed FeaturePython)
  ChamferSize = 0
  Closed = false
  End = (291.672,-92.565,0)
  FilletRadius = 0
  Length = 12.5
  MakeFace = true
  Placement = pos=(279.172,-92.565,0) rot=(0,0,1;0rad)
  Points = (2) [(0,0,0),(12.5,0,0)]
  Start = (279.172,-92.565,0)
  Subdivisions = 0
FEATURE [App::DocumentObjectGroup] Group073
  Group = -> [Arc274,Arc275,Arc272,Arc273,Line546,Line551,Line545,Line552]
FEATURE [Part::Part2DObjectPython] Arc276  # Draft 2D object (typed FeaturePython)
  FirstAngle = 90
  LastAngle = 180
  MakeFace = true
  Placement = pos=(298.23,-79.315,0) rot=(0,0,1;0rad)
  Radius = 0.75
FEATURE [Part::Part2DObjectPython] Arc277  # Draft 2D object (typed FeaturePython)
  FirstAngle = 90
  LastAngle = 180
  MakeFace = true
  Placement = pos=(310.73,-91.815,0) rot=(0,0,1;3.14159rad)
  Radius = 0.75
FEATURE [Part::Part2DObjectPython] Line555  # Draft 2D object (typed FeaturePython)
  ChamferSize = 0
  Closed = false
  End = (311.48,-79.315,0)
  FilletRadius = 0
  Length = 12.5
  MakeFace = true
  Placement = pos=(311.48,-91.815,0) rot=(0,0,1;0rad)
  Points = (2) [(0,0,0),(0,12.5,0)]
  Start = (311.48,-91.815,0)
  Subdivisions = 0
FEATURE [Part::Part2DObjectPython] Line556  # Draft 2D object (typed FeaturePython)
  ChamferSize = 0
  Closed = false
  End = (310.73,-92.565,0)
  FilletRadius = 0
  Length = 12.5
  MakeFace = true
  Placement = pos=(298.23,-92.565,0) rot=(0,0,1;0rad)
  Points = (2) [(0,0,0),(12.5,0,0)]
  Start = (298.23,-92.565,0)
  Subdivisions = 0
FEATURE [Part::Part2DObjectPython] Arc278  # Draft 2D object (typed FeaturePython)
  FirstAngle = 90
  LastAngle = 180
  MakeFace = true
  Placement = pos=(298.23,-91.815,0) rot=(0,0,1;1.5708rad)
  Radius = 0.75
FEATURE [Part::Part2DObjectPython] Line557  # Draft 2D object (typed FeaturePython)
  ChamferSize = 0
  Closed = false
  End = (298.23,-78.565,0)
  FilletRadius = 0
  Length = 12.5
  MakeFace = true
  Placement = pos=(310.73,-78.565,0) rot=(0,0,1;0rad)
  Points = (2) [(0,0,0),(-12.5,0,0)]
  Start = (310.73,-78.565,0)
  Subdivisions = 0
FEATURE [Part::Part2DObjectPython] Arc279  # Draft 2D object (typed FeaturePython)
  FirstAngle = 90
  LastAngle = 180
  MakeFace = true
  Placement = pos=(310.73,-79.315,0) rot=(0,0,-1;1.5708rad)
  Radius = 0.75
FEATURE [Part::Part2DObjectPython] Line560  # Draft 2D object (typed FeaturePython)
  ChamferSize = 0
  Closed = false
  End = (297.48,-91.815,0)
  FilletRadius = 0
  Length = 12.5
  MakeFace = true
  Placement = pos=(297.48,-79.315,0) rot=(0,0,1;0rad)
  Points = (2) [(0,0,0),(0,-12.5,0)]
  Start = (297.48,-79.315,0)
  Subdivisions = 0
FEATURE [App::DocumentObjectGroup] Group074
  Group = -> [Arc276,Arc279,Arc278,Arc277,Line555,Line557,Line560,Line556]
FEATURE [Part::Part2DObjectPython] Line575  # Draft 2D object (typed FeaturePython)
  ChamferSize = 0
  Closed = false
  End = (3.725,3.175,0)
  FilletRadius = 0
  Length = 8.48528
  MakeFace = true
  Placement = pos=(-2.275,-2.825,0) rot=(0,0,1;0rad)
  Points = (2) [(0,0,0),(6,6,0)]
  Start = (-2.275,-2.825,0)
  Subdivisions = 0
FEATURE [App::DocumentObjectGroup] Group077
  Group = -> [Line575]
FEATURE [Part::Part2DObjectPython] Line577  # Draft 2D object (typed FeaturePython)
  ChamferSize = 0
  Closed = false
  End = (316.18,-2.825,0)
  FilletRadius = 0
  Length = 8.48528
  MakeFace = true
  Placement = pos=(310.18,3.175,0) rot=(0,0,-1;1.5708rad)
  Points = (2) [(0,0,0),(6,6,0)]
  Start = (310.18,3.175,0)
  Subdivisions = 0
FEATURE [App::DocumentObjectGroup] Group078
  Group = -> [Line577]
FEATURE [Part::Part2DObjectPython] Line581  # Draft 2D object (typed FeaturePython)
  ChamferSize = 0
  Closed = false
  End = (310.18,-98.265,0)
  FilletRadius = 0
  Length = 8.48528
  MakeFace = true
  Placement = pos=(316.18,-92.265,0) rot=(0,0,1;3.14159rad)
  Points = (2) [(0,0,0),(6,6,0)]
  Start = (316.18,-92.265,0)
  Subdivisions = 0
FEATURE [App::DocumentObjectGroup] Group079
  Group = -> [Line581]
FEATURE [Part::Part2DObjectPython] Line584  # Draft 2D object (typed FeaturePython)
  ChamferSize = 0
  Closed = false
  End = (-2.275,-92.265,0)
  FilletRadius = 0
  Length = 8.48528
  MakeFace = true
  Placement = pos=(3.725,-98.265,0) rot=(0,0,1;1.5708rad)
  Points = (2) [(0,0,0),(6,6,0)]
  Start = (3.725,-98.265,0)
  Subdivisions = 0
FEATURE [App::DocumentObjectGroup] Group080
  Group = -> [Line584]
FEATURE [Part::Part2DObjectPython] Line585  # Draft 2D object (typed FeaturePython)
  ChamferSize = 0
  Closed = false
  End = (310.18,3.175,0)
  FilletRadius = 0
  Length = 306.455
  MakeFace = true
  Placement = pos=(3.725,3.175,0) rot=(0,0,1;0rad)
  Points = (2) [(0,0,0),(306.455,8.88178e-16,0)]
  Start = (3.725,3.175,0)
  Subdivisions = 0
FEATURE [Part::Part2DObjectPython] Line586  # Draft 2D object (typed FeaturePython)
  ChamferSize = 0
  Closed = false
  End = (316.18,-92.265,0)
  FilletRadius = 0
  Length = 89.44
  MakeFace = true
  Placement = pos=(316.18,-2.825,0) rot=(0,0,1;0rad)
  Points = (2) [(0,0,0),(0,-89.44,0)]
  Start = (316.18,-2.825,0)
  Subdivisions = 0
FEATURE [Part::Part2DObjectPython] Line587  # Draft 2D object (typed FeaturePython)
  ChamferSize = 0
  Closed = false
  End = (3.725,-98.265,0)
  FilletRadius = 0
  Length = 306.455
  MakeFace = true
  Placement = pos=(310.18,-98.265,0) rot=(0,0,1;0rad)
  Points = (2) [(0,0,0),(-306.455,-1.42109e-14,0)]
  Start = (310.18,-98.265,0)
  Subdivisions = 0
FEATURE [Part::Part2DObjectPython] Arc280  # Draft 2D object (typed FeaturePython)
  FirstAngle = 180
  LastAngle = 270
  MakeFace = true
  Placement = pos=(249.096,-55.2963,0) rot=(0,0,1;0rad)
  Radius = 0.75
FEATURE [Part::Part2DObjectPython] Arc281  # Draft 2D object (typed FeaturePython)
  FirstAngle = 180
  LastAngle = 270
  MakeFace = true
  Placement = pos=(254.596,-55.2963,0) rot=(0,0,1;1.5708rad)
  Radius = 0.75
FEATURE [Part::Part2DObjectPython] Arc282  # Draft 2D object (typed FeaturePython)
  FirstAngle = 180
  LastAngle = 270
  MakeFace = true
  Placement = pos=(249.096,-41.2963,0) rot=(0,0,-1;1.5708rad)
  Radius = 0.75
FEATURE [Part::Part2DObjectPython] Arc283  # Draft 2D object (typed FeaturePython)
  FirstAngle = 180
  LastAngle = 270
  MakeFace = true
  Placement = pos=(254.596,-41.2963,0) rot=(0,0,1;3.14159rad)
  Radius = 0.75
FEATURE [Part::Part2DObjectPython] Line590  # Draft 2D object (typed FeaturePython)
  ChamferSize = 0
  Closed = false
  End = (254.596,-40.5463,0)
  FilletRadius = 0
  Length = 5.5
  MakeFace = true
  Placement = pos=(249.096,-40.5463,0) rot=(0,0,1;0rad)
  Points = (2) [(0,0,0),(5.5,-1.42109e-14,0)]
  Start = (249.096,-40.5463,0)
  Subdivisions = 0
FEATURE [Part::Part2DObjectPython] Line591  # Draft 2D object (typed FeaturePython)
  ChamferSize = 0
  Closed = false
  End = (255.346,-55.2963,0)
  FilletRadius = 0
  Length = 14
  MakeFace = true
  Placement = pos=(255.346,-41.2963,0) rot=(0,0,1;0rad)
  Points = (2) [(0,0,0),(0,-14,0)]
  Start = (255.346,-41.2963,0)
  Subdivisions = 0
FEATURE [Part::Part2DObjectPython] Line592  # Draft 2D object (typed FeaturePython)
  ChamferSize = 0
  Closed = false
  End = (249.096,-56.0463,0)
  FilletRadius = 0
  Length = 5.5
  MakeFace = true
  Placement = pos=(254.596,-56.0463,0) rot=(0,0,1;0rad)
  Points = (2) [(0,0,0),(-5.5,1.42109e-14,0)]
  Start = (254.596,-56.0463,0)
  Subdivisions = 0
FEATURE [Part::Part2DObjectPython] Line593  # Draft 2D object (typed FeaturePython)
  ChamferSize = 0
  Closed = false
  End = (248.346,-41.2963,0)
  FilletRadius = 0
  Length = 14
  MakeFace = true
  Placement = pos=(248.346,-55.2963,0) rot=(0,0,1;0rad)
  Points = (2) [(0,0,0),(0,14,0)]
  Start = (248.346,-55.2963,0)
  Subdivisions = 0
FEATURE [App::DocumentObjectGroup] Group082
  Group = -> [Arc280,Arc281,Arc282,Arc283,Line590,Line591,Line592,Line593]
FEATURE [Part::Part2DObjectPython] Arc284  # Draft 2D object (typed FeaturePython)
  FirstAngle = 180
  LastAngle = 270
  MakeFace = true
  Placement = pos=(272.972,-55.2963,0) rot=(0,0,1;0rad)
  Radius = 0.75
FEATURE [Part::Part2DObjectPython] Line594  # Draft 2D object (typed FeaturePython)
  ChamferSize = 0
  Closed = false
  End = (279.222,-55.2963,0)
  FilletRadius = 0
  Length = 14
  MakeFace = true
  Placement = pos=(279.222,-41.2963,0) rot=(0,0,1;0rad)
  Points = (2) [(0,0,0),(0,-14,0)]
  Start = (279.222,-41.2963,0)
  Subdivisions = 0
FEATURE [Part::Part2DObjectPython] Arc285  # Draft 2D object (typed FeaturePython)
  FirstAngle = 180
  LastAngle = 270
  MakeFace = true
  Placement = pos=(278.472,-55.2963,0) rot=(0,0,1;1.5708rad)
  Radius = 0.75
FEATURE [Part::Part2DObjectPython] Arc286  # Draft 2D object (typed FeaturePython)
  FirstAngle = 180
  LastAngle = 270
  MakeFace = true
  Placement = pos=(272.972,-41.2963,0) rot=(0,0,-1;1.5708rad)
  Radius = 0.75
FEATURE [Part::Part2DObjectPython] Arc287  # Draft 2D object (typed FeaturePython)
  FirstAngle = 180
  LastAngle = 270
  MakeFace = true
  Placement = pos=(278.472,-41.2963,0) rot=(0,0,1;3.14159rad)
  Radius = 0.75
FEATURE [Part::Part2DObjectPython] Line595  # Draft 2D object (typed FeaturePython)
  ChamferSize = 0
  Closed = false
  End = (278.472,-40.5463,0)
  FilletRadius = 0
  Length = 5.5
  MakeFace = true
  Placement = pos=(272.972,-40.5463,0) rot=(0,0,1;0rad)
  Points = (2) [(0,0,0),(5.5,-1.42109e-14,0)]
  Start = (272.972,-40.5463,0)
  Subdivisions = 0
FEATURE [Part::Part2DObjectPython] Line596  # Draft 2D object (typed FeaturePython)
  ChamferSize = 0
  Closed = false
  End = (272.972,-56.0463,0)
  FilletRadius = 0
  Length = 5.5
  MakeFace = true
  Placement = pos=(278.472,-56.0463,0) rot=(0,0,1;0rad)
  Points = (2) [(0,0,0),(-5.5,1.42109e-14,0)]
  Start = (278.472,-56.0463,0)
  Subdivisions = 0
FEATURE [Part::Part2DObjectPython] Line597  # Draft 2D object (typed FeaturePython)
  ChamferSize = 0
  Closed = false
  End = (272.222,-41.2963,0)
  FilletRadius = 0
  Length = 14
  MakeFace = true
  Placement = pos=(272.222,-55.2963,0) rot=(0,0,1;0rad)
  Points = (2) [(0,0,0),(0,14,0)]
  Start = (272.222,-55.2963,0)
  Subdivisions = 0
FEATURE [App::DocumentObjectGroup] Group083
  Group = -> [Arc284,Arc285,Arc286,Arc287,Line595,Line594,Line596,Line597]
FEATURE [App::DocumentObjectGroup] Group045
  Group = -> [Arc171,Arc168,Arc170,Arc169,Line340,Line339,Line338,Line337,Group082,Group083]
FEATURE [Part::Part2DObjectPython] Arc288  # Draft 2D object (typed FeaturePython)
  FirstAngle = 180
  LastAngle = 270
  MakeFace = true
  Placement = pos=(6.7191,-74.3056,0) rot=(0,0,1;0rad)
  Radius = 0.75
FEATURE [Part::Part2DObjectPython] Line598  # Draft 2D object (typed FeaturePython)
  ChamferSize = 0
  Closed = false
  End = (12.9691,-74.3056,0)
  FilletRadius = 0
  Length = 14
  MakeFace = true
  Placement = pos=(12.9691,-60.3056,0) rot=(0,0,1;0rad)
  Points = (2) [(0,0,0),(0,-14,0)]
  Start = (12.9691,-60.3056,0)
  Subdivisions = 0
FEATURE [Part::Part2DObjectPython] Arc289  # Draft 2D object (typed FeaturePython)
  FirstAngle = 180
  LastAngle = 270
  MakeFace = true
  Placement = pos=(12.2191,-74.3056,0) rot=(0,0,1;1.5708rad)
  Radius = 0.75
FEATURE [Part::Part2DObjectPython] Arc290  # Draft 2D object (typed FeaturePython)
  FirstAngle = 180
  LastAngle = 270
  MakeFace = true
  Placement = pos=(6.7191,-60.3056,0) rot=(0,0,-1;1.5708rad)
  Radius = 0.75
FEATURE [Part::Part2DObjectPython] Arc291  # Draft 2D object (typed FeaturePython)
  FirstAngle = 180
  LastAngle = 270
  MakeFace = true
  Placement = pos=(12.2191,-60.3056,0) rot=(0,0,1;3.14159rad)
  Radius = 0.75
FEATURE [Part::Part2DObjectPython] Line599  # Draft 2D object (typed FeaturePython)
  ChamferSize = 0
  Closed = false
  End = (12.2191,-59.5556,0)
  FilletRadius = 0
  Length = 5.5
  MakeFace = true
  Placement = pos=(6.7191,-59.5556,0) rot=(0,0,1;0rad)
  Points = (2) [(0,0,0),(5.5,-1.42109e-14,0)]
  Start = (6.7191,-59.5556,0)
  Subdivisions = 0
FEATURE [Part::Part2DObjectPython] Arc292  # Draft 2D object (typed FeaturePython)
  FirstAngle = 180
  LastAngle = 270
  MakeFace = true
  Placement = pos=(30.5951,-74.3056,0) rot=(0,0,1;0rad)
  Radius = 0.75
FEATURE [Part::Part2DObjectPython] Arc293  # Draft 2D object (typed FeaturePython)
  FirstAngle = 180
  LastAngle = 270
  MakeFace = true
  Placement = pos=(36.0951,-60.3056,0) rot=(0,0,1;3.14159rad)
  Radius = 0.75
FEATURE [Part::Part2DObjectPython] Line600  # Draft 2D object (typed FeaturePython)
  ChamferSize = 0
  Closed = false
  End = (30.5951,-75.0556,0)
  FilletRadius = 0
  Length = 5.5
  MakeFace = true
  Placement = pos=(36.0951,-75.0556,0) rot=(0,0,1;0rad)
  Points = (2) [(0,0,0),(-5.5,1.42109e-14,0)]
  Start = (36.0951,-75.0556,0)
  Subdivisions = 0
FEATURE [Part::Part2DObjectPython] Line601  # Draft 2D object (typed FeaturePython)
  ChamferSize = 0
  Closed = false
  End = (6.7191,-75.0556,0)
  FilletRadius = 0
  Length = 5.5
  MakeFace = true
  Placement = pos=(12.2191,-75.0556,0) rot=(0,0,1;0rad)
  Points = (2) [(0,0,0),(-5.5,1.42109e-14,0)]
  Start = (12.2191,-75.0556,0)
  Subdivisions = 0
FEATURE [Part::Part2DObjectPython] Line602  # Draft 2D object (typed FeaturePython)
  ChamferSize = 0
  Closed = false
  End = (5.9691,-60.3056,0)
  FilletRadius = 0
  Length = 14
  MakeFace = true
  Placement = pos=(5.9691,-74.3056,0) rot=(0,0,1;0rad)
  Points = (2) [(0,0,0),(0,14,0)]
  Start = (5.9691,-74.3056,0)
  Subdivisions = 0
FEATURE [Part::Part2DObjectPython] Arc294  # Draft 2D object (typed FeaturePython)
  FirstAngle = 180
  LastAngle = 270
  MakeFace = true
  Placement = pos=(30.5951,-60.3056,0) rot=(0,0,-1;1.5708rad)
  Radius = 0.75
FEATURE [Part::Part2DObjectPython] Arc295  # Draft 2D object (typed FeaturePython)
  FirstAngle = 180
  LastAngle = 270
  MakeFace = true
  Placement = pos=(36.0951,-74.3056,0) rot=(0,0,1;1.5708rad)
  Radius = 0.75
FEATURE [Part::Part2DObjectPython] Line603  # Draft 2D object (typed FeaturePython)
  ChamferSize = 0
  Closed = false
  End = (29.8451,-60.3056,0)
  FilletRadius = 0
  Length = 14
  MakeFace = true
  Placement = pos=(29.8451,-74.3056,0) rot=(0,0,1;0rad)
  Points = (2) [(0,0,0),(0,14,0)]
  Start = (29.8451,-74.3056,0)
  Subdivisions = 0
FEATURE [Part::Part2DObjectPython] Line604  # Draft 2D object (typed FeaturePython)
  ChamferSize = 0
  Closed = false
  End = (36.0951,-59.5556,0)
  FilletRadius = 0
  Length = 5.5
  MakeFace = true
  Placement = pos=(30.5951,-59.5556,0) rot=(0,0,1;0rad)
  Points = (2) [(0,0,0),(5.5,-1.42109e-14,0)]
  Start = (30.5951,-59.5556,0)
  Subdivisions = 0
FEATURE [Part::Part2DObjectPython] Line605  # Draft 2D object (typed FeaturePython)
  ChamferSize = 0
  Closed = false
  End = (36.8451,-74.3056,0)
  FilletRadius = 0
  Length = 14
  MakeFace = true
  Placement = pos=(36.8451,-60.3056,0) rot=(0,0,1;0rad)
  Points = (2) [(0,0,0),(0,-14,0)]
  Start = (36.8451,-60.3056,0)
  Subdivisions = 0
FEATURE [App::DocumentObjectGroup] Group084
  Group = -> [Arc288,Arc289,Arc290,Arc291,Line599,Line598,Line601,Line602]
FEATURE [App::DocumentObjectGroup] Group085
  Group = -> [Arc292,Arc295,Arc294,Arc293,Line604,Line605,Line600,Line603]
FEATURE [App::DocumentObjectGroup] Group049
  Group = -> [Arc180,Arc181,Arc183,Arc182,Line361,Line363,Line365,Line367,Group085,Group084]
FEATURE [App::DocumentObjectGroup] Group075  label="ANSI"
  Group = -> [Group045,Group049,Group030]
FEATURE [Part::Part2DObjectPython] Arc296  # Draft 2D object (typed FeaturePython)
  FirstAngle = 180
  LastAngle = 270
  MakeFace = true
  Placement = pos=(265.538,-23.3536,0) rot=(0,0,-1;1.5708rad)
  Radius = 0.75
FEATURE [Part::Part2DObjectPython] Line606  # Draft 2D object (typed FeaturePython)
  ChamferSize = 0
  Closed = false
  End = (265.538,-29.6036,0)
  FilletRadius = 0
  Length = 14
  MakeFace = true
  Placement = pos=(279.538,-29.6036,0) rot=(0,0,-1;1.5708rad)
  Points = (2) [(0,0,0),(0,-14,0)]
  Start = (279.538,-29.6036,0)
  Subdivisions = 0
FEATURE [Part::Part2DObjectPython] Arc297  # Draft 2D object (typed FeaturePython)
  FirstAngle = 180
  LastAngle = 270
  MakeFace = true
  Placement = pos=(265.538,-28.8536,0) rot=(0,0,1;0rad)
  Radius = 0.75
FEATURE [Part::Part2DObjectPython] Arc298  # Draft 2D object (typed FeaturePython)
  FirstAngle = 180
  LastAngle = 270
  MakeFace = true
  Placement = pos=(279.538,-23.3536,0) rot=(0,0,1;3.14159rad)
  Radius = 0.75
FEATURE [Part::Part2DObjectPython] Arc299  # Draft 2D object (typed FeaturePython)
  FirstAngle = 180
  LastAngle = 270
  MakeFace = true
  Placement = pos=(279.538,-28.8536,0) rot=(0,0,1;1.5708rad)
  Radius = 0.75
FEATURE [Part::Part2DObjectPython] Line607  # Draft 2D object (typed FeaturePython)
  ChamferSize = 0
  Closed = false
  End = (280.288,-28.8536,0)
  FilletRadius = 0
  Length = 5.5
  MakeFace = true
  Placement = pos=(280.288,-23.3536,0) rot=(0,0,-1;1.5708rad)
  Points = (2) [(0,0,0),(5.5,0,0)]
  Start = (280.288,-23.3536,0)
  Subdivisions = 0
FEATURE [Part::Part2DObjectPython] Arc300  # Draft 2D object (typed FeaturePython)
  FirstAngle = 180
  LastAngle = 270
  MakeFace = true
  Placement = pos=(265.538,-47.2296,0) rot=(0,0,-1;1.5708rad)
  Radius = 0.75
FEATURE [Part::Part2DObjectPython] Arc301  # Draft 2D object (typed FeaturePython)
  FirstAngle = 180
  LastAngle = 270
  MakeFace = true
  Placement = pos=(279.538,-52.7296,0) rot=(0,0,1;1.5708rad)
  Radius = 0.75
FEATURE [Part::Part2DObjectPython] Line608  # Draft 2D object (typed FeaturePython)
  ChamferSize = 0
  Closed = false
  End = (264.788,-47.2296,0)
  FilletRadius = 0
  Length = 5.5
  MakeFace = true
  Placement = pos=(264.788,-52.7296,0) rot=(0,0,-1;1.5708rad)
  Points = (2) [(0,0,0),(-5.5,0,0)]
  Start = (264.788,-52.7296,0)
  Subdivisions = 0
FEATURE [Part::Part2DObjectPython] Line609  # Draft 2D object (typed FeaturePython)
  ChamferSize = 0
  Closed = false
  End = (264.788,-23.3536,0)
  FilletRadius = 0
  Length = 5.5
  MakeFace = true
  Placement = pos=(264.788,-28.8536,0) rot=(0,0,-1;1.5708rad)
  Points = (2) [(0,0,0),(-5.5,0,0)]
  Start = (264.788,-28.8536,0)
  Subdivisions = 0
FEATURE [Part::Part2DObjectPython] Line610  # Draft 2D object (typed FeaturePython)
  ChamferSize = 0
  Closed = false
  End = (279.538,-22.6036,0)
  FilletRadius = 0
  Length = 14
  MakeFace = true
  Placement = pos=(265.538,-22.6036,0) rot=(0,0,-1;1.5708rad)
  Points = (2) [(0,0,0),(0,14,0)]
  Start = (265.538,-22.6036,0)
  Subdivisions = 0
FEATURE [Part::Part2DObjectPython] Arc302  # Draft 2D object (typed FeaturePython)
  FirstAngle = 180
  LastAngle = 270
  MakeFace = true
  Placement = pos=(279.538,-47.2296,0) rot=(0,0,1;3.14159rad)
  Radius = 0.75
FEATURE [Part::Part2DObjectPython] Arc303  # Draft 2D object (typed FeaturePython)
  FirstAngle = 180
  LastAngle = 270
  MakeFace = true
  Placement = pos=(265.538,-52.7296,0) rot=(0,0,1;0rad)
  Radius = 0.75
FEATURE [Part::Part2DObjectPython] Line611  # Draft 2D object (typed FeaturePython)
  ChamferSize = 0
  Closed = false
  End = (279.538,-46.4796,0)
  FilletRadius = 0
  Length = 14
  MakeFace = true
  Placement = pos=(265.538,-46.4796,0) rot=(0,0,-1;1.5708rad)
  Points = (2) [(0,0,0),(0,14,0)]
  Start = (265.538,-46.4796,0)
  Subdivisions = 0
FEATURE [Part::Part2DObjectPython] Line612  # Draft 2D object (typed FeaturePython)
  ChamferSize = 0
  Closed = false
  End = (280.288,-52.7296,0)
  FilletRadius = 0
  Length = 5.5
  MakeFace = true
  Placement = pos=(280.288,-47.2296,0) rot=(0,0,-1;1.5708rad)
  Points = (2) [(0,0,0),(5.5,0,0)]
  Start = (280.288,-47.2296,0)
  Subdivisions = 0
FEATURE [Part::Part2DObjectPython] Line613  # Draft 2D object (typed FeaturePython)
  ChamferSize = 0
  Closed = false
  End = (265.538,-53.4796,0)
  FilletRadius = 0
  Length = 14
  MakeFace = true
  Placement = pos=(279.538,-53.4796,0) rot=(0,0,-1;1.5708rad)
  Points = (2) [(0,0,0),(0,-14,0)]
  Start = (279.538,-53.4796,0)
  Subdivisions = 0
FEATURE [App::DocumentObjectGroup] Group086
  Group = -> [Arc296,Arc297,Arc298,Arc299,Line607,Line606,Line609,Line610]
FEATURE [App::DocumentObjectGroup] Group087
  Group = -> [Arc300,Arc303,Arc302,Arc301,Line612,Line613,Line608,Line611]
FEATURE [App::DocumentObjectGroup] Group047
  Group = -> [Arc177,Arc176,Arc179,Arc178,Line360,Line355,Line359,Line356,Group086,Group087]
FEATURE [App::DocumentObjectGroup] Group076  label="ISO"
  Group = -> [Group051,Group050,Group047,Group046]
FEATURE [Part::Part2DObjectPython] Line615  # Draft 2D object (typed FeaturePython)
  ChamferSize = 0
  Closed = false
  End = (73.173,-92.565,0)
  FilletRadius = 0
  Length = 5.5
  MakeFace = true
  Placement = pos=(78.673,-92.565,0) rot=(0,0,1;0rad)
  Points = (2) [(0,0,0),(-5.5,1.42109e-14,0)]
  Start = (78.673,-92.565,0)
  Subdivisions = 0
FEATURE [Part::Part2DObjectPython] Arc304  # Draft 2D object (typed FeaturePython)
  FirstAngle = 180
  LastAngle = 270
  MakeFace = true
  Placement = pos=(173.249,-77.815,0) rot=(0,0,-1;1.5708rad)
  Radius = 0.75
FEATURE [Part::Part2DObjectPython] Line616  # Draft 2D object (typed FeaturePython)
  ChamferSize = 0
  Closed = false
  End = (72.423,-77.815,0)
  FilletRadius = 0
  Length = 14
  MakeFace = true
  Placement = pos=(72.423,-91.815,0) rot=(0,0,1;0rad)
  Points = (2) [(0,0,0),(0,14,0)]
  Start = (72.423,-91.815,0)
  Subdivisions = 0
FEATURE [Part::Part2DObjectPython] Arc305  # Draft 2D object (typed FeaturePython)
  FirstAngle = 180
  LastAngle = 270
  MakeFace = true
  Placement = pos=(178.749,-91.815,0) rot=(0,0,1;1.5708rad)
  Radius = 0.75
FEATURE [Part::Part2DObjectPython] Line617  # Draft 2D object (typed FeaturePython)
  ChamferSize = 0
  Closed = false
  End = (172.499,-77.815,0)
  FilletRadius = 0
  Length = 14
  MakeFace = true
  Placement = pos=(172.499,-91.815,0) rot=(0,0,1;0rad)
  Points = (2) [(0,0,0),(0,14,0)]
  Start = (172.499,-91.815,0)
  Subdivisions = 0
FEATURE [Part::Part2DObjectPython] Arc306  # Draft 2D object (typed FeaturePython)
  FirstAngle = 180
  LastAngle = 270
  MakeFace = true
  Placement = pos=(73.173,-91.815,0) rot=(0,0,1;0rad)
  Radius = 0.75
FEATURE [Part::Part2DObjectPython] Line618  # Draft 2D object (typed FeaturePython)
  ChamferSize = 0
  Closed = false
  End = (79.423,-91.815,0)
  FilletRadius = 0
  Length = 14
  MakeFace = true
  Placement = pos=(79.423,-77.815,0) rot=(0,0,1;0rad)
  Points = (2) [(0,0,0),(0,-14,0)]
  Start = (79.423,-77.815,0)
  Subdivisions = 0
FEATURE [Part::Part2DObjectPython] Arc307  # Draft 2D object (typed FeaturePython)
  FirstAngle = 180
  LastAngle = 270
  MakeFace = true
  Placement = pos=(78.673,-91.815,0) rot=(0,0,1;1.5708rad)
  Radius = 0.75
FEATURE [Part::Part2DObjectPython] Arc308  # Draft 2D object (typed FeaturePython)
  FirstAngle = 180
  LastAngle = 270
  MakeFace = true
  Placement = pos=(78.673,-77.815,0) rot=(0,0,1;3.14159rad)
  Radius = 0.75
FEATURE [Part::Part2DObjectPython] Line619  # Draft 2D object (typed FeaturePython)
  ChamferSize = 0
  Closed = false
  End = (78.673,-77.065,0)
  FilletRadius = 0
  Length = 5.5
  MakeFace = true
  Placement = pos=(73.173,-77.065,0) rot=(0,0,1;0rad)
  Points = (2) [(0,0,0),(5.5,-1.42109e-14,0)]
  Start = (73.173,-77.065,0)
  Subdivisions = 0
FEATURE [Part::Part2DObjectPython] Arc309  # Draft 2D object (typed FeaturePython)
  FirstAngle = 180
  LastAngle = 270
  MakeFace = true
  Placement = pos=(173.249,-91.815,0) rot=(0,0,1;0rad)
  Radius = 0.75
FEATURE [Part::Part2DObjectPython] Arc310  # Draft 2D object (typed FeaturePython)
  FirstAngle = 180
  LastAngle = 270
  MakeFace = true
  Placement = pos=(73.173,-77.815,0) rot=(0,0,-1;1.5708rad)
  Radius = 0.75
FEATURE [App::DocumentObjectGroup] Group089
  Group = -> [Arc306,Arc307,Arc310,Arc308,Line619,Line618,Line615,Line616]
FEATURE [Part::Part2DObjectPython] Arc311  # Draft 2D object (typed FeaturePython)
  FirstAngle = 180
  LastAngle = 270
  MakeFace = true
  Placement = pos=(178.749,-77.815,0) rot=(0,0,1;3.14159rad)
  Radius = 0.75
FEATURE [Part::Part2DObjectPython] Line620  # Draft 2D object (typed FeaturePython)
  ChamferSize = 0
  Closed = false
  End = (173.249,-92.565,0)
  FilletRadius = 0
  Length = 5.5
  MakeFace = true
  Placement = pos=(178.749,-92.565,0) rot=(0,0,1;0rad)
  Points = (2) [(0,0,0),(-5.5,1.42109e-14,0)]
  Start = (178.749,-92.565,0)
  Subdivisions = 0
FEATURE [Part::Part2DObjectPython] Line621  # Draft 2D object (typed FeaturePython)
  ChamferSize = 0
  Closed = false
  End = (179.499,-91.815,0)
  FilletRadius = 0
  Length = 14
  MakeFace = true
  Placement = pos=(179.499,-77.815,0) rot=(0,0,1;0rad)
  Points = (2) [(0,0,0),(0,-14,0)]
  Start = (179.499,-77.815,0)
  Subdivisions = 0
FEATURE [Part::Part2DObjectPython] Line622  # Draft 2D object (typed FeaturePython)
  ChamferSize = 0
  Closed = false
  End = (178.749,-77.065,0)
  FilletRadius = 0
  Length = 5.5
  MakeFace = true
  Placement = pos=(173.249,-77.065,0) rot=(0,0,1;0rad)
  Points = (2) [(0,0,0),(5.5,-1.42109e-14,0)]
  Start = (173.249,-77.065,0)
  Subdivisions = 0
FEATURE [App::DocumentObjectGroup] Group088
  Group = -> [Arc309,Arc305,Arc304,Arc311,Line622,Line621,Line620,Line617]
FEATURE [App::DocumentObjectGroup] Group068
  Group = -> [Arc253,Arc252,Arc254,Arc255,Line508,Line512,Line510,Line511,Group089,Group088]
FEATURE [App::DocumentObjectGroup] Group064  label="Row 5"
  Group = -> [Group065,Group066,Group067,Group068,Group069,Group070,Group071,Group072,Group073,Group074]
FEATURE [Part::Part2DObjectPython] Line623  # Draft 2D object (typed FeaturePython)
  ChamferSize = 0
  Closed = false
  End = (251.473,-18.025,0)
  FilletRadius = 0
  Length = 5.5
  MakeFace = true
  Placement = pos=(256.973,-18.025,0) rot=(0,0,1;0rad)
  Points = (2) [(0,0,0),(-5.5,1.42109e-14,0)]
  Start = (256.973,-18.025,0)
  Subdivisions = 0
FEATURE [Part::Part2DObjectPython] Arc312  # Draft 2D object (typed FeaturePython)
  FirstAngle = 180
  LastAngle = 270
  MakeFace = true
  Placement = pos=(275.349,-3.275,0) rot=(0,0,-1;1.5708rad)
  Radius = 0.75
FEATURE [Part::Part2DObjectPython] Line624  # Draft 2D object (typed FeaturePython)
  ChamferSize = 0
  Closed = false
  End = (250.723,-3.275,0)
  FilletRadius = 0
  Length = 14
  MakeFace = true
  Placement = pos=(250.723,-17.275,0) rot=(0,0,1;0rad)
  Points = (2) [(0,0,0),(0,14,0)]
  Start = (250.723,-17.275,0)
  Subdivisions = 0
FEATURE [Part::Part2DObjectPython] Arc313  # Draft 2D object (typed FeaturePython)
  FirstAngle = 180
  LastAngle = 270
  MakeFace = true
  Placement = pos=(280.849,-17.275,0) rot=(0,0,1;1.5708rad)
  Radius = 0.75
FEATURE [Part::Part2DObjectPython] Line625  # Draft 2D object (typed FeaturePython)
  ChamferSize = 0
  Closed = false
  End = (274.599,-3.275,0)
  FilletRadius = 0
  Length = 14
  MakeFace = true
  Placement = pos=(274.599,-17.275,0) rot=(0,0,1;0rad)
  Points = (2) [(0,0,0),(0,14,0)]
  Start = (274.599,-17.275,0)
  Subdivisions = 0
FEATURE [Part::Part2DObjectPython] Arc314  # Draft 2D object (typed FeaturePython)
  FirstAngle = 180
  LastAngle = 270
  MakeFace = true
  Placement = pos=(251.473,-17.275,0) rot=(0,0,1;0rad)
  Radius = 0.75
FEATURE [Part::Part2DObjectPython] Line626  # Draft 2D object (typed FeaturePython)
  ChamferSize = 0
  Closed = false
  End = (257.723,-17.275,0)
  FilletRadius = 0
  Length = 14
  MakeFace = true
  Placement = pos=(257.723,-3.275,0) rot=(0,0,1;0rad)
  Points = (2) [(0,0,0),(0,-14,0)]
  Start = (257.723,-3.275,0)
  Subdivisions = 0
FEATURE [Part::Part2DObjectPython] Arc315  # Draft 2D object (typed FeaturePython)
  FirstAngle = 180
  LastAngle = 270
  MakeFace = true
  Placement = pos=(256.973,-17.275,0) rot=(0,0,1;1.5708rad)
  Radius = 0.75
FEATURE [Part::Part2DObjectPython] Arc316  # Draft 2D object (typed FeaturePython)
  FirstAngle = 180
  LastAngle = 270
  MakeFace = true
  Placement = pos=(256.973,-3.275,0) rot=(0,0,1;3.14159rad)
  Radius = 0.75
FEATURE [Part::Part2DObjectPython] Line627  # Draft 2D object (typed FeaturePython)
  ChamferSize = 0
  Closed = false
  End = (256.973,-2.525,0)
  FilletRadius = 0
  Length = 5.5
  MakeFace = true
  Placement = pos=(251.473,-2.525,0) rot=(0,0,1;0rad)
  Points = (2) [(0,0,0),(5.5,-1.42109e-14,0)]
  Start = (251.473,-2.525,0)
  Subdivisions = 0
FEATURE [Part::Part2DObjectPython] Arc317  # Draft 2D object (typed FeaturePython)
  FirstAngle = 180
  LastAngle = 270
  MakeFace = true
  Placement = pos=(275.349,-17.275,0) rot=(0,0,1;0rad)
  Radius = 0.75
FEATURE [Part::Part2DObjectPython] Arc318  # Draft 2D object (typed FeaturePython)
  FirstAngle = 180
  LastAngle = 270
  MakeFace = true
  Placement = pos=(251.473,-3.275,0) rot=(0,0,-1;1.5708rad)
  Radius = 0.75
FEATURE [App::DocumentObjectGroup] Group091
  Group = -> [Arc314,Arc315,Arc318,Arc316,Line627,Line626,Line623,Line624]
FEATURE [Part::Part2DObjectPython] Arc319  # Draft 2D object (typed FeaturePython)
  FirstAngle = 180
  LastAngle = 270
  MakeFace = true
  Placement = pos=(280.849,-3.275,0) rot=(0,0,1;3.14159rad)
  Radius = 0.75
FEATURE [Part::Part2DObjectPython] Line628  # Draft 2D object (typed FeaturePython)
  ChamferSize = 0
  Closed = false
  End = (275.349,-18.025,0)
  FilletRadius = 0
  Length = 5.5
  MakeFace = true
  Placement = pos=(280.849,-18.025,0) rot=(0,0,1;0rad)
  Points = (2) [(0,0,0),(-5.5,1.42109e-14,0)]
  Start = (280.849,-18.025,0)
  Subdivisions = 0
FEATURE [Part::Part2DObjectPython] Line629  # Draft 2D object (typed FeaturePython)
  ChamferSize = 0
  Closed = false
  End = (281.599,-17.275,0)
  FilletRadius = 0
  Length = 14
  MakeFace = true
  Placement = pos=(281.599,-3.275,0) rot=(0,0,1;0rad)
  Points = (2) [(0,0,0),(0,-14,0)]
  Start = (281.599,-3.275,0)
  Subdivisions = 0
FEATURE [Part::Part2DObjectPython] Line630  # Draft 2D object (typed FeaturePython)
  ChamferSize = 0
  Closed = false
  End = (280.849,-2.525,0)
  FilletRadius = 0
  Length = 5.5
  MakeFace = true
  Placement = pos=(275.349,-2.525,0) rot=(0,0,1;0rad)
  Points = (2) [(0,0,0),(5.5,-1.42109e-14,0)]
  Start = (275.349,-2.525,0)
  Subdivisions = 0
FEATURE [App::DocumentObjectGroup] Group090
  Group = -> [Arc317,Arc313,Arc312,Arc319,Line630,Line629,Line628,Line625]
FEATURE [App::DocumentObjectGroup] Group013
  Group = -> [Arc054,Arc052,Arc055,Arc053,Line105,Line109,Line107,Line111,Group091,Group090]
FEATURE [App::DocumentObjectGroup] Group015  label="Row 1"
  Group = -> [Group001,Group002,Group003,Group004,Group005,Group006,Group007,Group008,Group009,Group010,Group011,Group012,Group013,Group014,Group]
FEATURE [Part::Part2DObjectPython] Line631  # Draft 2D object (typed FeaturePython)
  ChamferSize = 0
  Closed = false
  End = (239.591,-75.0556,0)
  FilletRadius = 0
  Length = 5.5
  MakeFace = true
  Placement = pos=(245.091,-75.0556,0) rot=(0,0,1;0rad)
  Points = (2) [(0,0,0),(-5.5,1.42109e-14,0)]
  Start = (245.091,-75.0556,0)
  Subdivisions = 0
FEATURE [Part::Part2DObjectPython] Arc320  # Draft 2D object (typed FeaturePython)
  FirstAngle = 180
  LastAngle = 270
  MakeFace = true
  Placement = pos=(263.467,-60.3056,0) rot=(0,0,-1;1.5708rad)
  Radius = 0.75
FEATURE [Part::Part2DObjectPython] Line632  # Draft 2D object (typed FeaturePython)
  ChamferSize = 0
  Closed = false
  End = (238.841,-60.3056,0)
  FilletRadius = 0
  Length = 14
  MakeFace = true
  Placement = pos=(238.841,-74.3056,0) rot=(0,0,1;0rad)
  Points = (2) [(0,0,0),(0,14,0)]
  Start = (238.841,-74.3056,0)
  Subdivisions = 0
FEATURE [Part::Part2DObjectPython] Arc321  # Draft 2D object (typed FeaturePython)
  FirstAngle = 180
  LastAngle = 270
  MakeFace = true
  Placement = pos=(268.967,-74.3056,0) rot=(0,0,1;1.5708rad)
  Radius = 0.75
FEATURE [Part::Part2DObjectPython] Line633  # Draft 2D object (typed FeaturePython)
  ChamferSize = 0
  Closed = false
  End = (262.717,-60.3056,0)
  FilletRadius = 0
  Length = 14
  MakeFace = true
  Placement = pos=(262.717,-74.3056,0) rot=(0,0,1;0rad)
  Points = (2) [(0,0,0),(0,14,0)]
  Start = (262.717,-74.3056,0)
  Subdivisions = 0
FEATURE [Part::Part2DObjectPython] Arc322  # Draft 2D object (typed FeaturePython)
  FirstAngle = 180
  LastAngle = 270
  MakeFace = true
  Placement = pos=(239.591,-74.3056,0) rot=(0,0,1;0rad)
  Radius = 0.75
FEATURE [Part::Part2DObjectPython] Line634  # Draft 2D object (typed FeaturePython)
  ChamferSize = 0
  Closed = false
  End = (245.841,-74.3056,0)
  FilletRadius = 0
  Length = 14
  MakeFace = true
  Placement = pos=(245.841,-60.3056,0) rot=(0,0,1;0rad)
  Points = (2) [(0,0,0),(0,-14,0)]
  Start = (245.841,-60.3056,0)
  Subdivisions = 0
FEATURE [Part::Part2DObjectPython] Arc323  # Draft 2D object (typed FeaturePython)
  FirstAngle = 180
  LastAngle = 270
  MakeFace = true
  Placement = pos=(245.091,-74.3056,0) rot=(0,0,1;1.5708rad)
  Radius = 0.75
FEATURE [Part::Part2DObjectPython] Arc324  # Draft 2D object (typed FeaturePython)
  FirstAngle = 180
  LastAngle = 270
  MakeFace = true
  Placement = pos=(245.091,-60.3056,0) rot=(0,0,1;3.14159rad)
  Radius = 0.75
FEATURE [Part::Part2DObjectPython] Line635  # Draft 2D object (typed FeaturePython)
  ChamferSize = 0
  Closed = false
  End = (245.091,-59.5556,0)
  FilletRadius = 0
  Length = 5.5
  MakeFace = true
  Placement = pos=(239.591,-59.5556,0) rot=(0,0,1;0rad)
  Points = (2) [(0,0,0),(5.5,-1.42109e-14,0)]
  Start = (239.591,-59.5556,0)
  Subdivisions = 0
FEATURE [Part::Part2DObjectPython] Arc325  # Draft 2D object (typed FeaturePython)
  FirstAngle = 180
  LastAngle = 270
  MakeFace = true
  Placement = pos=(263.467,-74.3056,0) rot=(0,0,1;0rad)
  Radius = 0.75
FEATURE [Part::Part2DObjectPython] Arc326  # Draft 2D object (typed FeaturePython)
  FirstAngle = 180
  LastAngle = 270
  MakeFace = true
  Placement = pos=(239.591,-60.3056,0) rot=(0,0,-1;1.5708rad)
  Radius = 0.75
FEATURE [App::DocumentObjectGroup] Group093
  Group = -> [Arc322,Arc323,Arc326,Arc324,Line635,Line634,Line631,Line632]
FEATURE [Part::Part2DObjectPython] Arc327  # Draft 2D object (typed FeaturePython)
  FirstAngle = 180
  LastAngle = 270
  MakeFace = true
  Placement = pos=(268.967,-60.3056,0) rot=(0,0,1;3.14159rad)
  Radius = 0.75
FEATURE [Part::Part2DObjectPython] Line636  # Draft 2D object (typed FeaturePython)
  ChamferSize = 0
  Closed = false
  End = (263.467,-75.0556,0)
  FilletRadius = 0
  Length = 5.5
  MakeFace = true
  Placement = pos=(268.967,-75.0556,0) rot=(0,0,1;0rad)
  Points = (2) [(0,0,0),(-5.5,1.42109e-14,0)]
  Start = (268.967,-75.0556,0)
  Subdivisions = 0
FEATURE [Part::Part2DObjectPython] Line637  # Draft 2D object (typed FeaturePython)
  ChamferSize = 0
  Closed = false
  End = (269.717,-74.3056,0)
  FilletRadius = 0
  Length = 14
  MakeFace = true
  Placement = pos=(269.717,-60.3056,0) rot=(0,0,1;0rad)
  Points = (2) [(0,0,0),(0,-14,0)]
  Start = (269.717,-60.3056,0)
  Subdivisions = 0
FEATURE [Part::Part2DObjectPython] Line638  # Draft 2D object (typed FeaturePython)
  ChamferSize = 0
  Closed = false
  End = (268.967,-59.5556,0)
  FilletRadius = 0
  Length = 5.5
  MakeFace = true
  Placement = pos=(263.467,-59.5556,0) rot=(0,0,1;0rad)
  Points = (2) [(0,0,0),(5.5,-1.42109e-14,0)]
  Start = (263.467,-59.5556,0)
  Subdivisions = 0
FEATURE [App::DocumentObjectGroup] Group092
  Group = -> [Arc325,Arc321,Arc320,Arc327,Line638,Line637,Line636,Line633]
FEATURE [App::DocumentObjectGroup] Group062
  Group = -> [Arc235,Arc234,Arc233,Arc232,Line472,Line469,Line468,Line466,Group093,Group092]
FEATURE [App::DocumentObjectGroup] Group048  label="Row 4"
  Group = -> [Group052,Group053,Group054,Group055,Group056,Group057,Group058,Group059,Group060,Group061,Group062,Group063]
FEATURE [Part::Part2DObjectPython] Circle  # Draft 2D object (typed FeaturePython)
  FirstAngle = 0
  LastAngle = 0
  MakeFace = false
  Placement = pos=(290.68,-45.415,0) rot=(0,0,1;0rad)
  Radius = 2.65
FEATURE [Part::Part2DObjectPython] Arc328  # Draft 2D object (typed FeaturePython)
  FirstAngle = -90
  LastAngle = 90
  MakeFace = true
  Placement = pos=(-1.4,-47.5463,0) rot=(0,0,1;0rad)
  Radius = 0.875
FEATURE [Part::Part2DObjectPython] Arc329  # Draft 2D object (typed FeaturePython)
  FirstAngle = -180
  LastAngle = -90
  MakeFace = true
  Placement = pos=(-2.025,-46.4213,0) rot=(0,0,1;0rad)
  Radius = 0.25
FEATURE [Part::Part2DObjectPython] Arc330  # Draft 2D object (typed FeaturePython)
  FirstAngle = 90
  LastAngle = 180
  MakeFace = true
  Placement = pos=(-2.025,-48.6713,0) rot=(0,0,1;0rad)
  Radius = 0.25
FEATURE [Part::Part2DObjectPython] Line  # Draft 2D object (typed FeaturePython)
  ChamferSize = 0
  Closed = false
  End = (-2.025,-46.6713,0)
  FilletRadius = 0
  Length = 0.625
  MakeFace = true
  Placement = pos=(-1.4,-46.6713,0) rot=(0,0,1;0rad)
  Points = (2) [(0,0,0),(-0.625,7.10543e-15,0)]
  Start = (-1.4,-46.6713,0)
  Subdivisions = 0
FEATURE [Part::Part2DObjectPython] Line641  # Draft 2D object (typed FeaturePython)
  ChamferSize = 0
  Closed = false
  End = (-1.4,-48.4213,0)
  FilletRadius = 0
  Length = 0.625
  MakeFace = true
  Placement = pos=(-2.025,-48.4213,0) rot=(0,0,1;0rad)
  Points = (2) [(0,0,0),(0.625,0,0)]
  Start = (-2.025,-48.4213,0)
  Subdivisions = 0
FEATURE [Part::Part2DObjectPython] Line642  # Draft 2D object (typed FeaturePython)
  ChamferSize = 0
  Closed = false
  End = (-2.275,-2.825,0)
  FilletRadius = 0
  Length = 43.5963
  MakeFace = true
  Placement = pos=(-2.275,-46.4213,0) rot=(0,0,1;0rad)
  Points = (2) [(0,0,0),(-1.15463e-14,43.5963,0)]
  Start = (-2.275,-46.4213,0)
  Subdivisions = 0
FEATURE [Part::Part2DObjectPython] Line643  # Draft 2D object (typed FeaturePython)
  ChamferSize = 0
  Closed = false
  End = (-2.275,-48.6713,0)
  FilletRadius = 0
  Length = 43.5937
  MakeFace = true
  Placement = pos=(-2.275,-92.265,0) rot=(0,0,1;0rad)
  Points = (2) [(0,0,0),(-1.15463e-14,43.5937,0)]
  Start = (-2.275,-92.265,0)
  Subdivisions = 0
FEATURE [App::DocumentObjectGroup] Group081  label="Border"
  Group = -> [Group077,Group078,Group079,Group080,Line585,Line586,Line587,Circle,Arc328,Arc329,Arc330,Line,Line641,Line642,Line643]
